FCSTD DOCUMENT  (FreeCAD 0.20R29177 +426 (Git))
Label: Input Cover
License: All rights reserved
LicenseURL: http://en.wikipedia.org/wiki/All_rights_reserved
objects: Sketcher::SketchObject×5, PartDesign::Body×1
note: 6 computed .brp shape members not serialized (recipe doc carries the construction recipe); baked Part::Feature solids carry a one-line shape summary decoded from their .brp

FEATURE [Sketcher::SketchObject] Sketch009  label="Sketch_FrameMain"
  AttachmentOffset = pos=(0,0,12.53) rot=(0,0,1;0rad)
  FullyConstrained = true
  MapMode = 5
  Placement = pos=(0,0,12.53) rot=(0,0,1;0rad)
  Support = -> [XY_Plane]
  expr: .AttachmentOffset.Base.z = 15.88 - 3.35
  sketch-geometry (262):
    g0: LineSegment StartX=0 StartY=0 StartZ=0 EndX=296.63 EndY=0 EndZ=0
    g1: LineSegment StartX=296.63 StartY=0 StartZ=0 EndX=296.63 EndY=221.98 EndZ=0
    g2: LineSegment StartX=289.63 StartY=228.98 StartZ=0 EndX=278.38 EndY=228.98 EndZ=0
    g3: LineSegment StartX=0 StartY=221.98 StartZ=0 EndX=0 EndY=0 EndZ=0
    g4: GeomPoint X=296.63 Y=228.98 Z=0
    g5: ArcOfCircle CenterX=289.63 CenterY=221.98 CenterZ=0 NormalX=0 NormalY=0 NormalZ=1 AngleXU=0 Radius=7 StartAngle=-9e-16 EndAngle=1.5708
    g6: GeomPoint X=296.63 Y=228.98 Z=0
    g7: ArcOfCircle CenterX=7 CenterY=221.98 CenterZ=0 NormalX=0 NormalY=0 NormalZ=1 AngleXU=0 Radius=7 StartAngle=1.5708 EndAngle=3.14159
    g8: GeomPoint X=0 Y=228.98 Z=0
    g9: LineSegment StartX=278.38 StartY=228.98 StartZ=0 EndX=278.38 EndY=216.23 EndZ=0
    g10: LineSegment StartX=18.25 StartY=228.98 StartZ=0 EndX=18.25 EndY=216.23 EndZ=0
    g11: LineSegment StartX=18.25 StartY=216.23 StartZ=0 EndX=278.38 EndY=216.23 EndZ=0
    g12: LineSegment StartX=18.25 StartY=228.98 StartZ=0 EndX=7 EndY=228.98 EndZ=0
    g13: LineSegment StartX=291.63 StartY=201.48 StartZ=0 EndX=291.63 EndY=93 EndZ=0
    g14: LineSegment StartX=0 StartY=114.49 StartZ=0 EndX=148.315 EndY=114.49 EndZ=0
    g15: LineSegment StartX=148.315 StartY=114.49 StartZ=0 EndX=296.63 EndY=114.49 EndZ=0
    g16: LineSegment StartX=18.25 StartY=228.98 StartZ=0 EndX=278.38 EndY=228.98 EndZ=0
    g17: LineSegment StartX=148.315 StartY=114.49 StartZ=0 EndX=148.315 EndY=228.98 EndZ=0
    g18: LineSegment StartX=148.315 StartY=114.49 StartZ=0 EndX=148.315 EndY=0 EndZ=0
    g19: LineSegment StartX=288.63 StartY=204.48 StartZ=0 EndX=8 EndY=204.48 EndZ=0
    g20: LineSegment StartX=288.63 StartY=90 StartZ=0 EndX=8 EndY=90 EndZ=0
    g21: LineSegment StartX=5 StartY=201.48 StartZ=0 EndX=5 EndY=93 EndZ=0
    g22: ArcOfCircle CenterX=8 CenterY=201.48 CenterZ=0 NormalX=0 NormalY=0 NormalZ=1 AngleXU=0 Radius=3 StartAngle=1.5708 EndAngle=3.14159
    g23: GeomPoint X=5 Y=204.48 Z=0
    g24: ArcOfCircle CenterX=8 CenterY=93 CenterZ=0 NormalX=0 NormalY=0 NormalZ=1 AngleXU=0 Radius=3 StartAngle=3.14159 EndAngle=4.71239
    g25: GeomPoint X=5 Y=90 Z=0
    g26: GeomPoint X=9.5 Y=94.5 Z=0
    g27: ArcOfCircle CenterX=288.63 CenterY=93 CenterZ=0 NormalX=0 NormalY=0 NormalZ=1 AngleXU=0 Radius=3 StartAngle=4.71239 EndAngle=6.28319
    g28: GeomPoint X=291.63 Y=90 Z=0
    g29: GeomPoint X=9.5 Y=199.98 Z=0
    g30: ArcOfCircle CenterX=288.63 CenterY=201.48 CenterZ=0 NormalX=0 NormalY=0 NormalZ=1 AngleXU=0 Radius=3 StartAngle=0 EndAngle=1.5708
    g31: GeomPoint X=291.63 Y=204.48 Z=0
    g32: GeomPoint X=287.13 Y=199.98 Z=0
    g33: ArcOfCircle CenterX=285.88 CenterY=198.73 CenterZ=0 NormalX=0 NormalY=0 NormalZ=1 AngleXU=0 Radius=1.25 StartAngle=2.5e-15 EndAngle=1.5708
    g34: LineSegment StartX=287.13 StartY=198.73 StartZ=0 EndX=287.13 EndY=191.543 EndZ=0
    g35: ArcOfCircle CenterX=285.88 CenterY=191.543 CenterZ=0 NormalX=0 NormalY=0 NormalZ=1 AngleXU=0 Radius=1.25 StartAngle=4.71239 EndAngle=6.28319
    g36: LineSegment StartX=285.88 StartY=190.293 StartZ=0 EndX=265.88 EndY=190.293 EndZ=0
    g37: ArcOfCircle CenterX=265.88 CenterY=191.543 CenterZ=0 NormalX=0 NormalY=0 NormalZ=1 AngleXU=0 Radius=1.25 StartAngle=3.14159 EndAngle=4.71239
    g38: LineSegment StartX=264.63 StartY=191.543 StartZ=0 EndX=264.63 EndY=198.73 EndZ=0
    g39: ArcOfCircle CenterX=265.88 CenterY=198.73 CenterZ=0 NormalX=0 NormalY=0 NormalZ=1 AngleXU=0 Radius=1.25 StartAngle=1.5708 EndAngle=3.14159
    g40: LineSegment StartX=265.88 StartY=199.98 StartZ=0 EndX=285.88 EndY=199.98 EndZ=0
    g41: GeomPoint X=287.13 Y=199.98 Z=0
    g42: GeomPoint X=264.63 Y=190.293 Z=0
    g43: ArcOfCircle CenterX=259.793 CenterY=198.73 CenterZ=0 NormalX=0 NormalY=0 NormalZ=1 AngleXU=0 Radius=1.25 StartAngle=-3.6e-15 EndAngle=1.5708
    g44: LineSegment StartX=261.043 StartY=198.73 StartZ=0 EndX=261.043 EndY=191.543 EndZ=0
    g45: ArcOfCircle CenterX=259.793 CenterY=191.543 CenterZ=0 NormalX=0 NormalY=0 NormalZ=1 AngleXU=0 Radius=1.25 StartAngle=4.71239 EndAngle=6.28319
    g46: LineSegment StartX=259.793 StartY=190.293 StartZ=0 EndX=246.793 EndY=190.293 EndZ=0
    g47: ArcOfCircle CenterX=246.793 CenterY=191.543 CenterZ=0 NormalX=0 NormalY=0 NormalZ=1 AngleXU=0 Radius=1.25 StartAngle=3.14159 EndAngle=4.71239
    g48: LineSegment StartX=245.543 StartY=191.543 StartZ=0 EndX=245.543 EndY=198.73 EndZ=0
    g49: ArcOfCircle CenterX=246.793 CenterY=198.73 CenterZ=0 NormalX=0 NormalY=0 NormalZ=1 AngleXU=0 Radius=1.25 StartAngle=1.5708 EndAngle=3.14159
    g50: LineSegment StartX=246.793 StartY=199.98 StartZ=0 EndX=259.793 EndY=199.98 EndZ=0
    g51: GeomPoint X=261.043 Y=199.98 Z=0
    g52: GeomPoint X=245.543 Y=190.293 Z=0
    g53: ArcOfCircle CenterX=240.706 CenterY=198.73 CenterZ=0 NormalX=0 NormalY=0 NormalZ=1 AngleXU=0 Radius=1.25 StartAngle=0 EndAngle=1.5708
    g54: LineSegment StartX=241.956 StartY=198.73 StartZ=0 EndX=241.956 EndY=191.543 EndZ=0
    g55: ArcOfCircle CenterX=240.706 CenterY=191.543 CenterZ=0 NormalX=0 NormalY=0 NormalZ=1 AngleXU=0 Radius=1.25 StartAngle=4.71239 EndAngle=6.28319
    g56: LineSegment StartX=240.706 StartY=190.293 StartZ=0 EndX=227.706 EndY=190.293 EndZ=0
    g57: ArcOfCircle CenterX=227.706 CenterY=191.543 CenterZ=0 NormalX=0 NormalY=0 NormalZ=1 AngleXU=0 Radius=1.25 StartAngle=3.14159 EndAngle=4.71239
    g58: LineSegment StartX=226.456 StartY=191.543 StartZ=0 EndX=226.456 EndY=198.73 EndZ=0
    g59: ArcOfCircle CenterX=227.706 CenterY=198.73 CenterZ=0 NormalX=0 NormalY=0 NormalZ=1 AngleXU=0 Radius=1.25 StartAngle=1.5708 EndAngle=3.14159
    g60: LineSegment StartX=227.706 StartY=199.98 StartZ=0 EndX=240.706 EndY=199.98 EndZ=0
    g61: GeomPoint X=241.956 Y=199.98 Z=0
    g62: GeomPoint X=226.456 Y=190.293 Z=0
    g63: ArcOfCircle CenterX=221.619 CenterY=198.73 CenterZ=0 NormalX=0 NormalY=0 NormalZ=1 AngleXU=0 Radius=1.25 StartAngle=8.5e-15 EndAngle=1.5708
    g64: LineSegment StartX=222.869 StartY=198.73 StartZ=0 EndX=222.869 EndY=191.543 EndZ=0
    g65: ArcOfCircle CenterX=221.619 CenterY=191.543 CenterZ=0 NormalX=0 NormalY=0 NormalZ=1 AngleXU=0 Radius=1.25 StartAngle=4.71239 EndAngle=6.28319
    g66: LineSegment StartX=221.619 StartY=190.293 StartZ=0 EndX=208.619 EndY=190.293 EndZ=0
    g67: ArcOfCircle CenterX=208.619 CenterY=191.543 CenterZ=0 NormalX=0 NormalY=0 NormalZ=1 AngleXU=0 Radius=1.25 StartAngle=3.14159 EndAngle=4.71239
    g68: LineSegment StartX=207.369 StartY=191.543 StartZ=0 EndX=207.369 EndY=198.73 EndZ=0
    g69: ArcOfCircle CenterX=208.619 CenterY=198.73 CenterZ=0 NormalX=0 NormalY=0 NormalZ=1 AngleXU=0 Radius=1.25 StartAngle=1.5708 EndAngle=3.14159
    g70: LineSegment StartX=208.619 StartY=199.98 StartZ=0 EndX=221.619 EndY=199.98 EndZ=0
    g71: GeomPoint X=222.869 Y=199.98 Z=0
    g72: GeomPoint X=207.369 Y=190.293 Z=0
    g73: ArcOfCircle CenterX=202.532 CenterY=198.73 CenterZ=0 NormalX=0 NormalY=0 NormalZ=1 AngleXU=0 Radius=1.25 StartAngle=2e-15 EndAngle=1.5708
    g74: LineSegment StartX=203.782 StartY=198.73 StartZ=0 EndX=203.782 EndY=191.543 EndZ=0
    g75: ArcOfCircle CenterX=202.532 CenterY=191.543 CenterZ=0 NormalX=0 NormalY=0 NormalZ=1 AngleXU=0 Radius=1.25 StartAngle=4.71239 EndAngle=6.28319
    g76: LineSegment StartX=202.532 StartY=190.293 StartZ=0 EndX=189.532 EndY=190.293 EndZ=0
    g77: ArcOfCircle CenterX=189.532 CenterY=191.543 CenterZ=0 NormalX=0 NormalY=0 NormalZ=1 AngleXU=0 Radius=1.25 StartAngle=3.14159 EndAngle=4.71239
    g78: LineSegment StartX=188.282 StartY=191.543 StartZ=0 EndX=188.282 EndY=198.73 EndZ=0
    g79: ArcOfCircle CenterX=189.532 CenterY=198.73 CenterZ=0 NormalX=0 NormalY=0 NormalZ=1 AngleXU=0 Radius=1.25 StartAngle=1.5708 EndAngle=3.14159
    g80: LineSegment StartX=189.532 StartY=199.98 StartZ=0 EndX=202.532 EndY=199.98 EndZ=0
    g81: GeomPoint X=203.782 Y=199.98 Z=0
    g82: GeomPoint X=188.282 Y=190.293 Z=0
    g83: ArcOfCircle CenterX=183.445 CenterY=198.73 CenterZ=0 NormalX=0 NormalY=0 NormalZ=1 AngleXU=0 Radius=1.25 StartAngle=-1.8e-15 EndAngle=1.5708
    g84: LineSegment StartX=184.695 StartY=198.73 StartZ=0 EndX=184.695 EndY=191.543 EndZ=0
    g85: ArcOfCircle CenterX=183.445 CenterY=191.543 CenterZ=0 NormalX=0 NormalY=0 NormalZ=1 AngleXU=0 Radius=1.25 StartAngle=4.71239 EndAngle=6.28319
    g86: LineSegment StartX=183.445 StartY=190.293 StartZ=0 EndX=170.445 EndY=190.293 EndZ=0
    g87: ArcOfCircle CenterX=170.445 CenterY=191.543 CenterZ=0 NormalX=0 NormalY=0 NormalZ=1 AngleXU=0 Radius=1.25 StartAngle=3.14159 EndAngle=4.71239
    g88: LineSegment StartX=169.195 StartY=191.543 StartZ=0 EndX=169.195 EndY=198.73 EndZ=0
    g89: ArcOfCircle CenterX=170.445 CenterY=198.73 CenterZ=0 NormalX=0 NormalY=0 NormalZ=1 AngleXU=0 Radius=1.25 StartAngle=1.5708 EndAngle=3.14159
    g90: LineSegment StartX=170.445 StartY=199.98 StartZ=0 EndX=183.445 EndY=199.98 EndZ=0
    g91: GeomPoint X=184.695 Y=199.98 Z=0
    g92: GeomPoint X=169.195 Y=190.293 Z=0
    g93: ArcOfCircle CenterX=164.358 CenterY=198.73 CenterZ=0 NormalX=0 NormalY=0 NormalZ=1 AngleXU=0 Radius=1.25 StartAngle=-5.3e-15 EndAngle=1.5708
    g94: LineSegment StartX=165.608 StartY=198.73 StartZ=0 EndX=165.608 EndY=191.543 EndZ=0
    g95: ArcOfCircle CenterX=164.358 CenterY=191.543 CenterZ=0 NormalX=0 NormalY=0 NormalZ=1 AngleXU=0 Radius=1.25 StartAngle=4.71239 EndAngle=6.28319
    g96: LineSegment StartX=164.358 StartY=190.293 StartZ=0 EndX=151.358 EndY=190.293 EndZ=0
    g97: ArcOfCircle CenterX=151.358 CenterY=191.543 CenterZ=0 NormalX=0 NormalY=0 NormalZ=1 AngleXU=0 Radius=1.25 StartAngle=3.14159 EndAngle=4.71239
    g98: LineSegment StartX=150.108 StartY=191.543 StartZ=0 EndX=150.108 EndY=198.73 EndZ=0
    g99: ArcOfCircle CenterX=151.358 CenterY=198.73 CenterZ=0 NormalX=0 NormalY=0 NormalZ=1 AngleXU=0 Radius=1.25 StartAngle=1.5708 EndAngle=3.14159
    g100: LineSegment StartX=151.358 StartY=199.98 StartZ=0 EndX=164.358 EndY=199.98 EndZ=0
    g101: GeomPoint X=165.608 Y=199.98 Z=0
    g102: GeomPoint X=150.108 Y=190.293 Z=0
    g103: ArcOfCircle CenterX=145.272 CenterY=198.73 CenterZ=0 NormalX=0 NormalY=0 NormalZ=1 AngleXU=0 Radius=1.25 StartAngle=2e-15 EndAngle=1.5708
    g104: LineSegment StartX=146.522 StartY=198.73 StartZ=0 EndX=146.522 EndY=191.543 EndZ=0
    g105: ArcOfCircle CenterX=145.272 CenterY=191.543 CenterZ=0 NormalX=0 NormalY=0 NormalZ=1 AngleXU=0 Radius=1.25 StartAngle=4.71239 EndAngle=6.28319
    g106: LineSegment StartX=145.272 StartY=190.293 StartZ=0 EndX=132.272 EndY=190.293 EndZ=0
    g107: ArcOfCircle CenterX=132.272 CenterY=191.543 CenterZ=0 NormalX=0 NormalY=0 NormalZ=1 AngleXU=0 Radius=1.25 StartAngle=3.14159 EndAngle=4.71239
    g108: LineSegment StartX=131.022 StartY=191.543 StartZ=0 EndX=131.022 EndY=198.73 EndZ=0
    g109: ArcOfCircle CenterX=132.272 CenterY=198.73 CenterZ=0 NormalX=0 NormalY=0 NormalZ=1 AngleXU=0 Radius=1.25 StartAngle=1.5708 EndAngle=3.14159
    g110: LineSegment StartX=132.272 StartY=199.98 StartZ=0 EndX=145.272 EndY=199.98 EndZ=0
    g111: GeomPoint X=146.522 Y=199.98 Z=0
    g112: GeomPoint X=131.022 Y=190.293 Z=0
    g113: ArcOfCircle CenterX=126.185 CenterY=198.73 CenterZ=0 NormalX=0 NormalY=0 NormalZ=1 AngleXU=0 Radius=1.25 StartAngle=8.6e-15 EndAngle=1.5708
    g114: LineSegment StartX=127.435 StartY=198.73 StartZ=0 EndX=127.435 EndY=191.543 EndZ=0
    g115: ArcOfCircle CenterX=126.185 CenterY=191.543 CenterZ=0 NormalX=0 NormalY=0 NormalZ=1 AngleXU=0 Radius=1.25 StartAngle=4.71239 EndAngle=6.28319
    g116: LineSegment StartX=126.185 StartY=190.293 StartZ=0 EndX=113.185 EndY=190.293 EndZ=0
    g117: ArcOfCircle CenterX=113.185 CenterY=191.543 CenterZ=0 NormalX=0 NormalY=0 NormalZ=1 AngleXU=0 Radius=1.25 StartAngle=3.14159 EndAngle=4.71239
    g118: LineSegment StartX=111.935 StartY=191.543 StartZ=0 EndX=111.935 EndY=198.73 EndZ=0
    g119: ArcOfCircle CenterX=113.185 CenterY=198.73 CenterZ=0 NormalX=0 NormalY=0 NormalZ=1 AngleXU=0 Radius=1.25 StartAngle=1.5708 EndAngle=3.14159
    g120: LineSegment StartX=113.185 StartY=199.98 StartZ=0 EndX=126.185 EndY=199.98 EndZ=0
    g121: GeomPoint X=127.435 Y=199.98 Z=0
    g122: GeomPoint X=111.935 Y=190.293 Z=0
    g123: LineSegment StartX=127.435 StartY=198.73 StartZ=0 EndX=131.022 EndY=198.73 EndZ=0
    g124: LineSegment StartX=146.522 StartY=198.73 StartZ=0 EndX=150.108 EndY=198.73 EndZ=0
    g125: LineSegment StartX=165.608 StartY=198.73 StartZ=0 EndX=169.195 EndY=198.73 EndZ=0
    g126: LineSegment StartX=184.695 StartY=198.73 StartZ=0 EndX=188.282 EndY=198.73 EndZ=0
    g127: LineSegment StartX=203.782 StartY=198.73 StartZ=0 EndX=207.369 EndY=198.73 EndZ=0
    g128: LineSegment StartX=222.869 StartY=198.73 StartZ=0 EndX=226.456 EndY=198.73 EndZ=0
    g129: LineSegment StartX=241.956 StartY=198.73 StartZ=0 EndX=245.543 EndY=198.73 EndZ=0
    g130: LineSegment StartX=261.043 StartY=198.73 StartZ=0 EndX=264.63 EndY=198.73 EndZ=0
    g131: ArcOfCircle CenterX=107.098 CenterY=198.73 CenterZ=0 NormalX=0 NormalY=0 NormalZ=1 AngleXU=0 Radius=1.25 StartAngle=8.7e-15 EndAngle=1.5708
    g132: LineSegment StartX=108.348 StartY=198.73 StartZ=0 EndX=108.348 EndY=191.543 EndZ=0
    g133: ArcOfCircle CenterX=107.098 CenterY=191.543 CenterZ=0 NormalX=0 NormalY=0 NormalZ=1 AngleXU=0 Radius=1.25 StartAngle=4.71239 EndAngle=6.28319
    g134: LineSegment StartX=107.098 StartY=190.293 StartZ=0 EndX=94.0977 EndY=190.293 EndZ=0
    g135: ArcOfCircle CenterX=94.0977 CenterY=191.543 CenterZ=0 NormalX=0 NormalY=0 NormalZ=1 AngleXU=0 Radius=1.25 StartAngle=3.14159 EndAngle=4.71239
    g136: LineSegment StartX=92.8477 StartY=191.543 StartZ=0 EndX=92.8477 EndY=198.73 EndZ=0
    g137: ArcOfCircle CenterX=94.0977 CenterY=198.73 CenterZ=0 NormalX=0 NormalY=0 NormalZ=1 AngleXU=0 Radius=1.25 StartAngle=1.5708 EndAngle=3.14159
    g138: LineSegment StartX=94.0977 StartY=199.98 StartZ=0 EndX=107.098 EndY=199.98 EndZ=0
    g139: GeomPoint X=108.348 Y=199.98 Z=0
    g140: GeomPoint X=92.8477 Y=190.293 Z=0
    g141: ArcOfCircle CenterX=88.0108 CenterY=198.73 CenterZ=0 NormalX=0 NormalY=0 NormalZ=1 AngleXU=0 Radius=1.25 StartAngle=1e-15 EndAngle=1.5708
    g142: LineSegment StartX=89.2608 StartY=198.73 StartZ=0 EndX=89.2608 EndY=191.543 EndZ=0
    g143: ArcOfCircle CenterX=88.0108 CenterY=191.543 CenterZ=0 NormalX=0 NormalY=0 NormalZ=1 AngleXU=0 Radius=1.25 StartAngle=4.71239 EndAngle=6.28319
    g144: LineSegment StartX=88.0108 StartY=190.293 StartZ=0 EndX=75.0108 EndY=190.293 EndZ=0
    g145: ArcOfCircle CenterX=75.0108 CenterY=191.543 CenterZ=0 NormalX=0 NormalY=0 NormalZ=1 AngleXU=0 Radius=1.25 StartAngle=3.14159 EndAngle=4.71239
    g146: LineSegment StartX=73.7608 StartY=191.543 StartZ=0 EndX=73.7608 EndY=198.73 EndZ=0
    g147: ArcOfCircle CenterX=75.0108 CenterY=198.73 CenterZ=0 NormalX=0 NormalY=0 NormalZ=1 AngleXU=0 Radius=1.25 StartAngle=1.5708 EndAngle=3.14159
    g148: LineSegment StartX=75.0108 StartY=199.98 StartZ=0 EndX=88.0108 EndY=199.98 EndZ=0
    g149: GeomPoint X=89.2608 Y=199.98 Z=0
    g150: GeomPoint X=73.7608 Y=190.293 Z=0
    g151: ArcOfCircle CenterX=68.9238 CenterY=198.73 CenterZ=0 NormalX=0 NormalY=0 NormalZ=1 AngleXU=0 Radius=1.25 StartAngle=-5.3e-15 EndAngle=1.5708
    g152: LineSegment StartX=70.1738 StartY=198.73 StartZ=0 EndX=70.1738 EndY=191.543 EndZ=0
    g153: ArcOfCircle CenterX=68.9238 CenterY=191.543 CenterZ=0 NormalX=0 NormalY=0 NormalZ=1 AngleXU=0 Radius=1.25 StartAngle=4.71239 EndAngle=6.28319
    g154: LineSegment StartX=68.9238 StartY=190.293 StartZ=0 EndX=55.9238 EndY=190.293 EndZ=0
    g155: ArcOfCircle CenterX=55.9238 CenterY=191.543 CenterZ=0 NormalX=0 NormalY=0 NormalZ=1 AngleXU=0 Radius=1.25 StartAngle=3.14159 EndAngle=4.71239
    g156: LineSegment StartX=54.6738 StartY=191.543 StartZ=0 EndX=54.6738 EndY=198.73 EndZ=0
    g157: ArcOfCircle CenterX=55.9238 CenterY=198.73 CenterZ=0 NormalX=0 NormalY=0 NormalZ=1 AngleXU=0 Radius=1.25 StartAngle=1.5708 EndAngle=3.14159
    g158: LineSegment StartX=55.9238 StartY=199.98 StartZ=0 EndX=68.9238 EndY=199.98 EndZ=0
    g159: GeomPoint X=70.1738 Y=199.98 Z=0
    g160: LineSegment StartX=70.1738 StartY=198.73 StartZ=0 EndX=73.7608 EndY=198.73 EndZ=0
    g161: LineSegment StartX=89.2608 StartY=198.73 StartZ=0 EndX=92.8477 EndY=198.73 EndZ=0
    g162: ArcOfCircle CenterX=10.75 CenterY=198.73 CenterZ=0 NormalX=0 NormalY=0 NormalZ=1 AngleXU=0 Radius=1.25 StartAngle=1.5708 EndAngle=3.14159
    g163: LineSegment StartX=10.75 StartY=199.98 StartZ=0 EndX=30.75 EndY=199.98 EndZ=0
    g164: ArcOfCircle CenterX=30.75 CenterY=198.73 CenterZ=0 NormalX=0 NormalY=0 NormalZ=1 AngleXU=0 Radius=1.25 StartAngle=5.9e-15 EndAngle=1.5708
    g165: LineSegment StartX=32 StartY=198.73 StartZ=0 EndX=32 EndY=191.543 EndZ=0
    g166: ArcOfCircle CenterX=30.75 CenterY=191.543 CenterZ=0 NormalX=0 NormalY=0 NormalZ=1 AngleXU=0 Radius=1.25 StartAngle=4.71239 EndAngle=6.28319
    g167: LineSegment StartX=30.75 StartY=190.293 StartZ=0 EndX=10.75 EndY=190.293 EndZ=0
    g168: ArcOfCircle CenterX=10.75 CenterY=191.543 CenterZ=0 NormalX=0 NormalY=0 NormalZ=1 AngleXU=0 Radius=1.25 StartAngle=3.14159 EndAngle=4.71239
    g169: LineSegment StartX=9.5 StartY=191.543 StartZ=0 EndX=9.5 EndY=198.73 EndZ=0
    g170: GeomPoint X=9.5 Y=199.98 Z=0
    g171: GeomPoint X=32 Y=190.293 Z=0
    g172: ArcOfCircle CenterX=36.8369 CenterY=198.73 CenterZ=0 NormalX=0 NormalY=0 NormalZ=1 AngleXU=0 Radius=1.25 StartAngle=1.5708 EndAngle=3.14159
    g173: LineSegment StartX=36.8369 StartY=199.98 StartZ=0 EndX=49.8369 EndY=199.98 EndZ=0
    g174: ArcOfCircle CenterX=49.8369 CenterY=198.73 CenterZ=0 NormalX=0 NormalY=0 NormalZ=1 AngleXU=0 Radius=1.25 StartAngle=-5.3e-15 EndAngle=1.5708
    g175: LineSegment StartX=51.0869 StartY=198.73 StartZ=0 EndX=51.0869 EndY=191.543 EndZ=0
    g176: ArcOfCircle CenterX=49.8369 CenterY=191.543 CenterZ=0 NormalX=0 NormalY=0 NormalZ=1 AngleXU=0 Radius=1.25 StartAngle=4.71239 EndAngle=6.28319
    g177: LineSegment StartX=49.8369 StartY=190.293 StartZ=0 EndX=36.8369 EndY=190.293 EndZ=0
    g178: ArcOfCircle CenterX=36.8369 CenterY=191.543 CenterZ=0 NormalX=0 NormalY=0 NormalZ=1 AngleXU=0 Radius=1.25 StartAngle=3.14159 EndAngle=4.71239
    g179: LineSegment StartX=35.5869 StartY=191.543 StartZ=0 EndX=35.5869 EndY=198.73 EndZ=0
    g180: GeomPoint X=35.5869 Y=199.98 Z=0
    g181: GeomPoint X=51.0869 Y=190.293 Z=0
    g182: LineSegment StartX=32 StartY=198.73 StartZ=0 EndX=35.5869 EndY=198.73 EndZ=0
    g183: LineSegment StartX=51.0869 StartY=198.73 StartZ=0 EndX=54.6738 EndY=198.73 EndZ=0
    g184: ArcOfCircle CenterX=285.88 CenterY=185.384 CenterZ=0 NormalX=0 NormalY=0 NormalZ=1 AngleXU=0 Radius=1.25 StartAngle=4e-15 EndAngle=1.5708
    g185: LineSegment StartX=287.13 StartY=185.384 StartZ=0 EndX=287.13 EndY=172.384 EndZ=0
    g186: ArcOfCircle CenterX=285.88 CenterY=172.384 CenterZ=0 NormalX=0 NormalY=0 NormalZ=1 AngleXU=0 Radius=1.25 StartAngle=4.71239 EndAngle=6.28319
    g187: LineSegment StartX=285.88 StartY=171.134 StartZ=0 EndX=258.88 EndY=171.134 EndZ=0
    g188: ArcOfCircle CenterX=258.88 CenterY=172.384 CenterZ=0 NormalX=0 NormalY=0 NormalZ=1 AngleXU=0 Radius=1.25 StartAngle=3.14159 EndAngle=4.71239
    g189: LineSegment StartX=257.63 StartY=172.384 StartZ=0 EndX=257.63 EndY=185.384 EndZ=0
    g190: ArcOfCircle CenterX=258.88 CenterY=185.384 CenterZ=0 NormalX=0 NormalY=0 NormalZ=1 AngleXU=0 Radius=1.25 StartAngle=1.5708 EndAngle=3.14159
    g191: LineSegment StartX=258.88 StartY=186.634 StartZ=0 EndX=285.88 EndY=186.634 EndZ=0
    g192: GeomPoint X=287.13 Y=186.634 Z=0
    g193: GeomPoint X=257.63 Y=171.134 Z=0
    g194: LineSegment StartX=285.88 StartY=190.293 StartZ=0 EndX=285.88 EndY=186.634 EndZ=0
    g195: ArcOfCircle CenterX=285.88 CenterY=166.226 CenterZ=0 NormalX=0 NormalY=0 NormalZ=1 AngleXU=0 Radius=1.25 StartAngle=-8e-15 EndAngle=1.5708
    g196: LineSegment StartX=287.13 StartY=166.226 StartZ=0 EndX=287.13 EndY=153.226 EndZ=0
    g197: ArcOfCircle CenterX=285.88 CenterY=153.226 CenterZ=0 NormalX=0 NormalY=0 NormalZ=1 AngleXU=0 Radius=1.25 StartAngle=4.71239 EndAngle=6.28319
    g198: LineSegment StartX=285.88 StartY=151.976 StartZ=0 EndX=267.88 EndY=151.976 EndZ=0
    g199: ArcOfCircle CenterX=267.88 CenterY=153.226 CenterZ=0 NormalX=0 NormalY=0 NormalZ=1 AngleXU=0 Radius=1.25 StartAngle=3.14159 EndAngle=4.71239
    g200: LineSegment StartX=266.63 StartY=153.226 StartZ=0 EndX=266.63 EndY=166.226 EndZ=0
    g201: ArcOfCircle CenterX=267.88 CenterY=166.226 CenterZ=0 NormalX=0 NormalY=0 NormalZ=1 AngleXU=0 Radius=1.25 StartAngle=1.5708 EndAngle=3.14159
    g202: LineSegment StartX=267.88 StartY=167.476 StartZ=0 EndX=285.88 EndY=167.476 EndZ=0
    g203: GeomPoint X=287.13 Y=167.476 Z=0
    g204: GeomPoint X=266.63 Y=151.976 Z=0
    g205: ArcOfCircle CenterX=285.88 CenterY=147.067 CenterZ=0 NormalX=0 NormalY=0 NormalZ=1 AngleXU=0 Radius=1.25 StartAngle=8.4e-15 EndAngle=1.5708
    g206: LineSegment StartX=287.13 StartY=147.067 StartZ=0 EndX=287.13 EndY=134.067 EndZ=0
    g207: ArcOfCircle CenterX=285.88 CenterY=134.067 CenterZ=0 NormalX=0 NormalY=0 NormalZ=1 AngleXU=0 Radius=1.25 StartAngle=4.71239 EndAngle=6.28319
    g208: LineSegment StartX=285.88 StartY=132.817 StartZ=0 EndX=253.505 EndY=132.817 EndZ=0
    g209: ArcOfCircle CenterX=253.505 CenterY=134.067 CenterZ=0 NormalX=0 NormalY=0 NormalZ=1 AngleXU=0 Radius=1.25 StartAngle=3.14159 EndAngle=4.71239
    g210: LineSegment StartX=252.255 StartY=134.067 StartZ=0 EndX=252.255 EndY=147.067 EndZ=0
    g211: ArcOfCircle CenterX=253.505 CenterY=147.067 CenterZ=0 NormalX=0 NormalY=0 NormalZ=1 AngleXU=0 Radius=1.25 StartAngle=1.5708 EndAngle=3.14159
    g212: LineSegment StartX=253.505 StartY=148.317 StartZ=0 EndX=285.88 EndY=148.317 EndZ=0
    g213: GeomPoint X=287.13 Y=148.317 Z=0
    g214: GeomPoint X=252.255 Y=132.817 Z=0
    g215: ArcOfCircle CenterX=285.88 CenterY=127.909 CenterZ=0 NormalX=0 NormalY=0 NormalZ=1 AngleXU=0 Radius=1.25 StartAngle=2.9e-15 EndAngle=1.5708
    g216: LineSegment StartX=287.13 StartY=127.909 StartZ=0 EndX=287.13 EndY=114.909 EndZ=0
    g217: ArcOfCircle CenterX=285.88 CenterY=114.909 CenterZ=0 NormalX=0 NormalY=0 NormalZ=1 AngleXU=0 Radius=1.25 StartAngle=4.71239 EndAngle=6.28319
    g218: LineSegment StartX=285.88 StartY=113.659 StartZ=0 EndX=244.592 EndY=113.659 EndZ=0
    g219: ArcOfCircle CenterX=244.592 CenterY=114.909 CenterZ=0 NormalX=0 NormalY=0 NormalZ=1 AngleXU=0 Radius=1.25 StartAngle=3.14159 EndAngle=4.71239
    g220: LineSegment StartX=243.342 StartY=114.909 StartZ=0 EndX=243.342 EndY=127.909 EndZ=0
    g221: ArcOfCircle CenterX=244.592 CenterY=127.909 CenterZ=0 NormalX=0 NormalY=0 NormalZ=1 AngleXU=0 Radius=1.25 StartAngle=1.5708 EndAngle=3.14159
    g222: LineSegment StartX=244.592 StartY=129.159 StartZ=0 EndX=285.88 EndY=129.159 EndZ=0
    g223: GeomPoint X=287.13 Y=129.159 Z=0
    g224: GeomPoint X=243.343 Y=113.659 Z=0
    g225: LineSegment StartX=285.88 StartY=171.134 StartZ=0 EndX=285.88 EndY=167.476 EndZ=0
    g226: LineSegment StartX=285.88 StartY=151.976 StartZ=0 EndX=285.88 EndY=148.317 EndZ=0
    g227: LineSegment StartX=285.88 StartY=132.817 StartZ=0 EndX=285.88 EndY=129.159 EndZ=0
    g228: ArcOfCircle CenterX=285.88 CenterY=198.73 CenterZ=0 NormalX=0 NormalY=0 NormalZ=1 AngleXU=0 Radius=1.25 StartAngle=-5.3e-15 EndAngle=1.5708
    g229: LineSegment StartX=287.13 StartY=198.73 StartZ=0 EndX=287.13 EndY=95.75 EndZ=0
    g230: ArcOfCircle CenterX=285.88 CenterY=95.75 CenterZ=0 NormalX=0 NormalY=0 NormalZ=1 AngleXU=0 Radius=1.25 StartAngle=4.71239 EndAngle=6.28319
    g231: LineSegment StartX=285.88 StartY=94.5 StartZ=0 EndX=10.75 EndY=94.5 EndZ=0
    g232: ArcOfCircle CenterX=10.75 CenterY=95.75 CenterZ=0 NormalX=0 NormalY=0 NormalZ=1 AngleXU=0 Radius=1.25 StartAngle=3.14159 EndAngle=4.71239
    g233: LineSegment StartX=9.5 StartY=95.75 StartZ=0 EndX=9.5 EndY=198.73 EndZ=0
    g234: ArcOfCircle CenterX=10.75 CenterY=198.73 CenterZ=0 NormalX=0 NormalY=0 NormalZ=1 AngleXU=0 Radius=1.25 StartAngle=1.5708 EndAngle=3.14159
    g235: LineSegment StartX=10.75 StartY=199.98 StartZ=0 EndX=285.88 EndY=199.98 EndZ=0
    g236: GeomPoint X=287.13 Y=199.98 Z=0
    g237: GeomPoint X=9.5 Y=94.5 Z=0
    g238: LineSegment StartX=287.13 StartY=198.73 StartZ=0 EndX=291.63 EndY=198.73 EndZ=0
    g239: LineSegment StartX=285.88 StartY=199.98 StartZ=0 EndX=285.88 EndY=204.48 EndZ=0
    g240: LineSegment StartX=111.935 StartY=198.73 StartZ=0 EndX=108.348 EndY=198.73 EndZ=0
    g241: LineSegment StartX=285.88 StartY=94.5 StartZ=0 EndX=285.88 EndY=90 EndZ=0
    g242: ArcOfCircle CenterX=285.88 CenterY=108.75 CenterZ=0 NormalX=0 NormalY=0 NormalZ=1 AngleXU=0 Radius=1.25 StartAngle=2.8e-15 EndAngle=1.5708
    g243: LineSegment StartX=287.13 StartY=108.75 StartZ=0 EndX=287.13 EndY=95.75 EndZ=0
    g244: ArcOfCircle CenterX=285.88 CenterY=95.75 CenterZ=0 NormalX=0 NormalY=0 NormalZ=1 AngleXU=0 Radius=1.25 StartAngle=4.71239 EndAngle=6.28319
    g245: LineSegment StartX=285.88 StartY=94.5 StartZ=0 EndX=269.88 EndY=94.5 EndZ=0
    g246: ArcOfCircle CenterX=269.88 CenterY=95.75 CenterZ=0 NormalX=0 NormalY=0 NormalZ=1 AngleXU=0 Radius=1.25 StartAngle=3.14159 EndAngle=4.71239
    g247: LineSegment StartX=268.63 StartY=95.75 StartZ=0 EndX=268.63 EndY=108.75 EndZ=0
    g248: ArcOfCircle CenterX=269.88 CenterY=108.75 CenterZ=0 NormalX=0 NormalY=0 NormalZ=1 AngleXU=0 Radius=1.25 StartAngle=1.5708 EndAngle=3.14159
    g249: LineSegment StartX=269.88 StartY=110 StartZ=0 EndX=285.88 EndY=110 EndZ=0
    g250: GeomPoint X=287.13 Y=110 Z=0
    g251: GeomPoint X=268.63 Y=94.5 Z=0
    g252: LineSegment StartX=285.88 StartY=113.659 StartZ=0 EndX=285.88 EndY=110 EndZ=0
    g253: LineSegment StartX=285.88 StartY=110 StartZ=0 EndX=9.5 EndY=110 EndZ=0
    g254: LineSegment StartX=285.88 StartY=113.659 StartZ=0 EndX=9.5 EndY=113.659 EndZ=0
    g255: LineSegment StartX=285.88 StartY=129.159 StartZ=0 EndX=9.5 EndY=129.159 EndZ=0
    g256: LineSegment StartX=285.88 StartY=132.817 StartZ=0 EndX=9.5 EndY=132.817 EndZ=0
    g257: LineSegment StartX=285.88 StartY=148.317 StartZ=0 EndX=9.5 EndY=148.317 EndZ=0
    g258: LineSegment StartX=285.88 StartY=151.976 StartZ=0 EndX=9.5 EndY=151.976 EndZ=0
    g259: LineSegment StartX=285.88 StartY=167.476 StartZ=0 EndX=9.5 EndY=167.476 EndZ=0
    g260: LineSegment StartX=285.88 StartY=171.134 StartZ=0 EndX=9.5 EndY=171.134 EndZ=0
    g261: LineSegment StartX=285.88 StartY=186.634 StartZ=0 EndX=9.5 EndY=186.634 EndZ=0
  constraints (626):
    c: Coincident(g0,g1)
    c: Coincident(g3,g0)
    c: Horizontal(g0)
    c: Horizontal(g2)
    c: Vertical(g1)
    c: Vertical(g3)
    c: Coincident(g0,g-1)
    c: DistanceX(g0,g0) = 296.63
    c: DistanceY(g1,g6) = 228.98
    c: Coincident(g4,g6)
    c: PointOnObject(g6,g1)
    c: PointOnObject(g6,g2)
    c: Tangent(g1,g5) = -1.5708
    c: Tangent(g2,g5) = -1.5708
    c: PointOnObject(g8,g3)
    c: PointOnObject(g8,g2)
    c: Tangent(g3,g7) = -1.5708
    c: Coincident(g12,g7) = -1.5708
    c: Radius(g7) = 7
    c: Radius(g5) = 7
    c: Vertical(g9)
    c: Vertical(g10)
    c: DistanceX(g8,g10) = 18.25
    c: DistanceX(g9,g4) = 18.25
    c: Distance(g9) = 12.75
    c: Coincident(g11,g10)
    c: Coincident(g11,g9)
    c: Coincident(g2,g9)
    c: Coincident(g12,g10)
    c: Horizontal(g12)
    c: Equal(g3,g1)
    c: Equal(g10,g9)
    c: Equal(g12,g2)
    c: Vertical(g13)
    c: DistanceX(g28,g0) = 5
    c: DistanceY(g0,g28) = 90
    c: DistanceY(g31,g9) = 11.75
    c: PointOnObject(g14,g3)
    c: Horizontal(g14)
    c: Coincident(g14,g15)
    c: PointOnObject(g15,g1)
    c: Horizontal(g15)
    c: Equal(g14,g15)
    c: Coincident(g16,g10)
    c: Coincident(g16,g2)
    c: Coincident(g17,g14)
    c: PointOnObject(g17,g16)
    c: Vertical(g17)
    c: Coincident(g18,g14)
    c: PointOnObject(g18,g0)
    c: Vertical(g18)
    c: Equal(g17,g18)
    c: Horizontal(g20)
    c: Symmetric(g23,g31,g17)
    c: Symmetric(g29,g32,g17)
    c: PointOnObject(g23,g21)
    c: PointOnObject(g23,g19)
    c: Tangent(g21,g22) = -1.5708
    c: Tangent(g19,g22) = -1.5708
    c: PointOnObject(g25,g21)
    c: PointOnObject(g25,g20)
    c: Tangent(g21,g24) = -1.5708
    c: Tangent(g20,g24) = 1.5708
    c: PointOnObject(g28,g20)
    c: PointOnObject(g28,g13)
    c: Tangent(g20,g27) = 1.5708
    c: Tangent(g13,g27) = 1.5708
    c: PointOnObject(g31,g19)
    c: PointOnObject(g31,g13)
    c: Tangent(g19,g30) = -1.5708
    c: Tangent(g13,g30) = 1.5708
    c: Radius(g30) = 3
    c: Radius(g22) = 3
    c: Radius(g24) = 3
    c: Radius(g27) = 3
    c: Vertical(g21)
    c: Tangent(g33,g34) = 1.5708
    c: Tangent(g34,g35) = 1.5708
    c: Tangent(g35,g36) = 1.5708
    c: Tangent(g36,g37) = 1.5708
    c: Tangent(g37,g38) = 1.5708
    c: Tangent(g38,g39) = 1.5708
    c: Tangent(g39,g40) = 1.5708
    c: Tangent(g40,g33) = 1.5708
    c: Horizontal(g36)
    c: Horizontal(g40)
    c: Vertical(g34)
    c: Vertical(g38)
    c: Equal(g33,g35)
    c: Equal(g35,g37)
    c: Equal(g37,g39)
    c: PointOnObject(g41,g34)
    c: PointOnObject(g41,g40)
    c: PointOnObject(g42,g36)
    c: PointOnObject(g42,g38)
    c: Coincident(g41,g32)
    c: DistanceY(g36,g39) = 9.6875
    c: DistanceX(g38,g33) = 22.5
    c: Radius(g33) = 1.25
    c: Tangent(g43,g44) = 1.5708
    c: Tangent(g44,g45) = 1.5708
    c: Tangent(g45,g46) = 1.5708
    c: Tangent(g46,g47) = 1.5708
    c: Tangent(g47,g48) = 1.5708
    c: Tangent(g48,g49) = 1.5708
    c: Tangent(g49,g50) = 1.5708
    c: Tangent(g50,g43) = 1.5708
    c: Horizontal(g46)
    c: Horizontal(g50)
    c: Vertical(g44)
    c: Vertical(g48)
    c: Equal(g43,g45)
    c: Equal(g45,g47)
    c: Equal(g47,g49)
    c: PointOnObject(g51,g44)
    c: PointOnObject(g51,g50)
    c: PointOnObject(g52,g46)
    c: PointOnObject(g52,g48)
    c: Equal(g43,g39)
    c: Equal(g44,g38)
    c: Tangent(g53,g54) = 1.5708
    c: Tangent(g54,g55) = 1.5708
    c: Tangent(g55,g56) = 1.5708
    c: Tangent(g56,g57) = 1.5708
    c: Tangent(g57,g58) = 1.5708
    c: Tangent(g58,g59) = 1.5708
    c: Tangent(g59,g60) = 1.5708
    c: Tangent(g60,g53) = 1.5708
    c: Horizontal(g56)
    c: Horizontal(g60)
    c: Vertical(g54)
    c: Vertical(g58)
    c: Equal(g53,g55)
    c: Equal(g55,g57)
    c: Equal(g57,g59)
    c: PointOnObject(g61,g54)
    c: PointOnObject(g61,g60)
    c: PointOnObject(g62,g56)
    c: PointOnObject(g62,g58)
    c: Tangent(g63,g64) = 1.5708
    c: Tangent(g64,g65) = 1.5708
    c: Tangent(g65,g66) = 1.5708
    c: Tangent(g66,g67) = 1.5708
    c: Tangent(g67,g68) = 1.5708
    c: Tangent(g68,g69) = 1.5708
    c: Tangent(g69,g70) = 1.5708
    c: Tangent(g70,g63) = 1.5708
    c: Horizontal(g66)
    c: Horizontal(g70)
    c: Vertical(g64)
    c: Vertical(g68)
    c: Equal(g63,g65)
    c: Equal(g65,g67)
    c: Equal(g67,g69)
    c: PointOnObject(g71,g64)
    c: PointOnObject(g71,g70)
    c: PointOnObject(g72,g66)
    c: PointOnObject(g72,g68)
    c: Tangent(g73,g74) = 1.5708
    c: Tangent(g74,g75) = 1.5708
    c: Tangent(g75,g76) = 1.5708
    c: Tangent(g76,g77) = 1.5708
    c: Tangent(g77,g78) = 1.5708
    c: Tangent(g78,g79) = 1.5708
    c: Tangent(g79,g80) = 1.5708
    c: Tangent(g80,g73) = 1.5708
    c: Horizontal(g76)
    c: Horizontal(g80)
    c: Vertical(g74)
    c: Vertical(g78)
    c: Equal(g73,g75)
    c: Equal(g75,g77)
    c: Equal(g77,g79)
    c: PointOnObject(g81,g74)
    c: PointOnObject(g81,g80)
    c: PointOnObject(g82,g76)
    c: PointOnObject(g82,g78)
    c: Tangent(g83,g84) = 1.5708
    c: Tangent(g84,g85) = 1.5708
    c: Tangent(g85,g86) = 1.5708
    c: Tangent(g86,g87) = 1.5708
    c: Tangent(g87,g88) = 1.5708
    c: Tangent(g88,g89) = 1.5708
    c: Tangent(g89,g90) = 1.5708
    c: Tangent(g90,g83) = 1.5708
    c: Horizontal(g86)
    c: Horizontal(g90)
    c: Vertical(g84)
    c: Vertical(g88)
    c: Equal(g83,g85)
    c: Equal(g85,g87)
    c: Equal(g87,g89)
    c: PointOnObject(g91,g84)
    c: PointOnObject(g91,g90)
    c: PointOnObject(g92,g86)
    c: PointOnObject(g92,g88)
    c: Tangent(g93,g94) = 1.5708
    c: Tangent(g94,g95) = 1.5708
    c: Tangent(g95,g96) = 1.5708
    c: Tangent(g96,g97) = 1.5708
    c: Tangent(g97,g98) = 1.5708
    c: Tangent(g98,g99) = 1.5708
    c: Tangent(g99,g100) = 1.5708
    c: Tangent(g100,g93) = 1.5708
    c: Horizontal(g96)
    c: Horizontal(g100)
    c: Vertical(g94)
    c: Vertical(g98)
    c: Equal(g93,g95)
    c: Equal(g95,g97)
    c: Equal(g97,g99)
    c: PointOnObject(g101,g94)
    c: PointOnObject(g101,g100)
    c: PointOnObject(g102,g96)
    c: PointOnObject(g102,g98)
    c: Tangent(g103,g104) = 1.5708
    c: Tangent(g104,g105) = 1.5708
    c: Tangent(g105,g106) = 1.5708
    c: Tangent(g106,g107) = 1.5708
    c: Tangent(g107,g108) = 1.5708
    c: Tangent(g108,g109) = 1.5708
    c: Tangent(g109,g110) = 1.5708
    c: Tangent(g110,g103) = 1.5708
    c: Horizontal(g106)
    c: Horizontal(g110)
    c: Vertical(g104)
    c: Vertical(g108)
    c: Equal(g103,g105)
    c: Equal(g105,g107)
    c: Equal(g107,g109)
    c: PointOnObject(g111,g104)
    c: PointOnObject(g111,g110)
    c: PointOnObject(g112,g106)
    c: PointOnObject(g112,g108)
    c: Tangent(g113,g114) = 1.5708
    c: Tangent(g114,g115) = 1.5708
    c: Tangent(g115,g116) = 1.5708
    c: Tangent(g116,g117) = 1.5708
    c: Tangent(g117,g118) = 1.5708
    c: Tangent(g118,g119) = 1.5708
    c: Tangent(g119,g120) = 1.5708
    c: Tangent(g120,g113) = 1.5708
    c: Horizontal(g116)
    c: Horizontal(g120)
    c: Vertical(g114)
    c: Vertical(g118)
    c: Equal(g113,g115)
    c: Equal(g115,g117)
    c: Equal(g117,g119)
    c: PointOnObject(g121,g114)
    c: PointOnObject(g121,g120)
    c: PointOnObject(g122,g116)
    c: PointOnObject(g122,g118)
    c: Equal(g53,g49)
    c: Equal(g54,g48)
    c: Equal(g46,g56)
    c: Equal(g63,g59)
    c: Equal(g58,g64)
    c: Equal(g70,g60)
    c: Equal(g80,g70)
    c: Equal(g73,g69)
    c: Equal(g74,g68)
    c: Equal(g78,g84)
    c: Equal(g83,g79)
    c: Equal(g90,g80)
    c: Equal(g93,g89)
    c: Equal(g99,g103)
    c: Equal(g104,g98)
    c: Equal(g94,g88)
    c: Equal(g110,g100)
    c: Equal(g100,g90)
    c: Equal(g113,g109)
    c: Coincident(g123,g113)
    c: Coincident(g123,g108)
    c: Coincident(g124,g103)
    c: Coincident(g124,g98)
    c: Coincident(g125,g93)
    c: Coincident(g125,g88)
    c: Coincident(g126,g83)
    c: Coincident(g126,g78)
    c: Coincident(g127,g73)
    c: Coincident(g127,g68)
    c: Coincident(g128,g63)
    c: Coincident(g128,g58)
    c: Coincident(g129,g53)
    c: Coincident(g129,g48)
    c: Equal(g129,g128)
    c: Equal(g127,g128)
    c: Equal(g126,g127)
    c: Equal(g125,g126)
    c: Equal(g124,g125)
    c: Equal(g123,g124)
    c: Equal(g114,g108)
    c: Equal(g110,g120)
    c: Coincident(g130,g43)
    c: Coincident(g130,g38)
    c: Tangent(g131,g132) = 1.5708
    c: Tangent(g132,g133) = 1.5708
    c: Tangent(g133,g134) = 1.5708
    c: Tangent(g134,g135) = 1.5708
    c: Tangent(g135,g136) = 1.5708
    c: Tangent(g136,g137) = 1.5708
    c: Tangent(g137,g138) = 1.5708
    c: Tangent(g138,g131) = 1.5708
    c: Horizontal(g134)
    c: Horizontal(g138)
    c: Vertical(g132)
    c: Vertical(g136)
    c: Equal(g131,g133)
    c: Equal(g133,g135)
    c: Equal(g135,g137)
    c: PointOnObject(g139,g132)
    c: PointOnObject(g139,g138)
    c: PointOnObject(g140,g134)
    c: PointOnObject(g140,g136)
    c: Tangent(g141,g142) = 1.5708
    c: Tangent(g142,g143) = 1.5708
    c: Tangent(g143,g144) = 1.5708
    c: Tangent(g144,g145) = 1.5708
    c: Tangent(g145,g146) = 1.5708
    c: Tangent(g146,g147) = 1.5708
    c: Tangent(g147,g148) = 1.5708
    c: Tangent(g148,g141) = 1.5708
    c: Horizontal(g144)
    c: Horizontal(g148)
    c: Vertical(g142)
    c: Vertical(g146)
    c: Equal(g141,g143)
    c: Equal(g143,g145)
    c: Equal(g145,g147)
    c: PointOnObject(g149,g142)
    c: PointOnObject(g149,g148)
    c: PointOnObject(g150,g144)
    c: PointOnObject(g150,g146)
    c: Tangent(g151,g152) = 1.5708
    c: Tangent(g152,g153) = 1.5708
    c: Tangent(g153,g154) = 1.5708
    c: Tangent(g154,g155) = 1.5708
    c: Tangent(g155,g156) = 1.5708
    c: Tangent(g156,g157) = 1.5708
    c: Tangent(g157,g158) = 1.5708
    c: Tangent(g158,g151) = 1.5708
    c: Horizontal(g154)
    c: Horizontal(g158)
    c: Vertical(g152)
    c: Vertical(g156)
    c: Equal(g151,g153)
    c: Equal(g153,g155)
    c: Equal(g155,g157)
    c: PointOnObject(g159,g152)
    c: PointOnObject(g159,g158)
    c: Equal(g152,g146)
    c: Equal(g151,g147)
    c: Equal(g141,g137)
    c: Equal(g136,g142)
    c: Equal(g148,g138)
    c: Equal(g132,g118)
    c: Equal(g119,g131)
    c: Equal(g138,g120)
    c: Coincident(g160,g151)
    c: Coincident(g160,g146)
    c: Coincident(g161,g141)
    c: Coincident(g161,g136)
    c: DistanceX(g48,g43) = 15.5
    c: Equal(g158,g148)
    c: Tangent(g162,g163) = 1.5708
    c: Tangent(g163,g164) = 1.5708
    c: Tangent(g164,g165) = 1.5708
    c: Tangent(g165,g166) = 1.5708
    c: Tangent(g166,g167) = 1.5708
    c: Tangent(g167,g168) = 1.5708
    c: Tangent(g168,g169) = 1.5708
    c: Tangent(g169,g162) = 1.5708
    c: Horizontal(g163)
    c: Horizontal(g167)
    c: Vertical(g165)
    c: Vertical(g169)
    c: Equal(g162,g164)
    c: Equal(g164,g166)
    c: Equal(g166,g168)
    c: PointOnObject(g170,g163)
    c: PointOnObject(g170,g169)
    c: PointOnObject(g171,g165)
    c: PointOnObject(g171,g167)
    c: Coincident(g170,g29)
    c: Tangent(g172,g173) = 1.5708
    c: Tangent(g173,g174) = 1.5708
    c: Tangent(g174,g175) = 1.5708
    c: Tangent(g175,g176) = 1.5708
    c: Tangent(g176,g177) = 1.5708
    c: Tangent(g177,g178) = 1.5708
    c: Tangent(g178,g179) = 1.5708
    c: Tangent(g179,g172) = 1.5708
    c: Horizontal(g173)
    c: Horizontal(g177)
    c: Vertical(g175)
    c: Vertical(g179)
    c: Equal(g172,g174)
    c: Equal(g174,g176)
    c: Equal(g176,g178)
    c: PointOnObject(g180,g173)
    c: PointOnObject(g180,g179)
    c: PointOnObject(g181,g175)
    c: PointOnObject(g181,g177)
    c: Equal(g164,g172)
    c: Equal(g165,g179)
    c: Equal(g175,g156)
    c: Equal(g174,g157)
    c: Coincident(g182,g164)
    c: Coincident(g182,g172)
    c: Coincident(g183,g174)
    c: Coincident(g183,g156)
    c: Equal(g173,g158)
    c: Equal(g163,g40)
    c: Equal(g130,g129)
    c: Tangent(g184,g185) = 1.5708
    c: Tangent(g185,g186) = 1.5708
    c: Tangent(g186,g187) = 1.5708
    c: Tangent(g187,g188) = 1.5708
    c: Tangent(g188,g189) = 1.5708
    c: Tangent(g189,g190) = 1.5708
    c: Tangent(g190,g191) = 1.5708
    c: Tangent(g191,g184) = 1.5708
    c: Horizontal(g187)
    c: Horizontal(g191)
    c: Vertical(g185)
    c: Vertical(g189)
    c: Equal(g184,g186)
    c: Equal(g186,g188)
    c: Equal(g188,g190)
    c: PointOnObject(g192,g185)
    c: PointOnObject(g192,g191)
    c: PointOnObject(g193,g187)
    c: PointOnObject(g193,g189)
    c: Equal(g35,g184)
    c: Coincident(g194,g35)
    c: Coincident(g194,g184)
    c: Vertical(g194)
    c: Equal(g46,g185)
    c: DistanceX(g189,g184) = 29.5
    c: Tangent(g195,g196) = 1.5708
    c: Tangent(g196,g197) = 1.5708
    c: Tangent(g197,g198) = 1.5708
    c: Tangent(g198,g199) = 1.5708
    c: Tangent(g199,g200) = 1.5708
    c: Tangent(g200,g201) = 1.5708
    c: Tangent(g201,g202) = 1.5708
    c: Tangent(g202,g195) = 1.5708
    c: Horizontal(g198)
    c: Horizontal(g202)
    c: Vertical(g196)
    c: Vertical(g200)
    c: Equal(g195,g197)
    c: Equal(g197,g199)
    c: Equal(g199,g201)
    c: PointOnObject(g203,g196)
    c: PointOnObject(g203,g202)
    c: PointOnObject(g204,g198)
    c: PointOnObject(g204,g200)
    c: Tangent(g205,g206) = 1.5708
    c: Tangent(g206,g207) = 1.5708
    c: Tangent(g207,g208) = 1.5708
    c: Tangent(g208,g209) = 1.5708
    c: Tangent(g209,g210) = 1.5708
    c: Tangent(g210,g211) = 1.5708
    c: Tangent(g211,g212) = 1.5708
    c: Tangent(g212,g205) = 1.5708
    c: Horizontal(g208)
    c: Horizontal(g212)
    c: Vertical(g206)
    c: Vertical(g210)
    c: Equal(g205,g207)
    c: Equal(g207,g209)
    c: Equal(g209,g211)
    c: PointOnObject(g213,g206)
    c: PointOnObject(g213,g212)
    c: PointOnObject(g214,g208)
    c: PointOnObject(g214,g210)
    c: Tangent(g215,g216) = 1.5708
    c: Tangent(g216,g217) = 1.5708
    c: Tangent(g217,g218) = 1.5708
    c: Tangent(g218,g219) = 1.5708
    c: Tangent(g219,g220) = 1.5708
    c: Tangent(g220,g221) = 1.5708
    c: Tangent(g221,g222) = 1.5708
    c: Tangent(g222,g215) = 1.5708
    c: Horizontal(g218)
    c: Horizontal(g222)
    c: Vertical(g216)
    c: Vertical(g220)
    c: Equal(g215,g217)
    c: Equal(g217,g219)
    c: Equal(g219,g221)
    c: PointOnObject(g223,g216)
    c: PointOnObject(g223,g222)
    c: PointOnObject(g224,g218)
    c: PointOnObject(g224,g220)
    c: Equal(g215,g207)
    c: Equal(g205,g197)
    c: Equal(g195,g186)
    c: Coincident(g225,g186)
    c: Coincident(g225,g195)
    c: Coincident(g226,g197)
    c: Coincident(g226,g205)
    c: Coincident(g227,g207)
    c: Coincident(g227,g215)
    c: Equal(g227,g226)
    c: Equal(g226,g225)
    c: Equal(g194,g225)
    c: Equal(g196,g206)
    c: Equal(g206,g216)
    c: Equal(g185,g196)
    c: DistanceX(g200,g195) = 20.5
    c: DistanceX(g210,g205) = 34.875
    c: DistanceX(g220,g215) = 43.7875
    c: Tangent(g228,g229) = 1.5708
    c: Tangent(g229,g230) = 1.5708
    c: Tangent(g230,g231) = 1.5708
    c: Tangent(g231,g232) = 1.5708
    c: Tangent(g232,g233) = 1.5708
    c: Tangent(g233,g234) = 1.5708
    c: Tangent(g234,g235) = 1.5708
    c: Tangent(g235,g228) = 1.5708
    c: Horizontal(g231)
    c: Horizontal(g235)
    c: Vertical(g229)
    c: Vertical(g233)
    c: Equal(g228,g230)
    c: Equal(g230,g232)
    c: Equal(g232,g234)
    c: PointOnObject(g236,g229)
    c: PointOnObject(g236,g235)
    c: PointOnObject(g237,g231)
    c: PointOnObject(g237,g233)
    c: Coincident(g236,g32)
    c: Coincident(g237,g26)
    c: Radius(g228) = 1.25
    c: PointOnObject(g43,g235)
    c: PointOnObject(g53,g235)
    c: PointOnObject(g63,g235)
    c: PointOnObject(g73,g235)
    c: PointOnObject(g83,g235)
    c: PointOnObject(g93,g235)
    c: PointOnObject(g103,g235)
    c: PointOnObject(g113,g235)
    c: PointOnObject(g131,g235)
    c: PointOnObject(g141,g235)
    c: PointOnObject(g151,g235)
    c: PointOnObject(g173,g235)
    c: PointOnObject(g168,g233)
    c: Coincident(g238,g33)
    c: PointOnObject(g238,g13)
    c: Horizontal(g238)
    c: Coincident(g239,g33)
    c: PointOnObject(g239,g19)
    c: Vertical(g239)
    c: Equal(g239,g238)
    c: DistanceX(g238,g238) = 4.5
    c: Equal(g182,g183)
    c: Coincident(g240,g118)
    c: Coincident(g240,g131)
    c: Equal(g183,g160)
    c: Equal(g160,g161)
    c: Equal(g161,g240)
    c: Equal(g240,g123)
    c: PointOnObject(g195,g229)
    c: PointOnObject(g205,g229)
    c: PointOnObject(g215,g229)
    c: Coincident(g241,g230)
    c: PointOnObject(g241,g20)
    c: Vertical(g241)
    c: Equal(g241,g238)
    c: Tangent(g242,g243) = 1.5708
    c: Tangent(g243,g244) = 1.5708
    c: Tangent(g244,g245) = 1.5708
    c: Tangent(g245,g246) = 1.5708
    c: Tangent(g246,g247) = 1.5708
    c: Tangent(g247,g248) = 1.5708
    c: Tangent(g248,g249) = 1.5708
    c: Tangent(g249,g242) = 1.5708
    c: Horizontal(g245)
    c: Horizontal(g249)
    c: Vertical(g243)
    c: Vertical(g247)
    c: Equal(g242,g244)
    c: Equal(g244,g246)
    c: Equal(g246,g248)
    c: PointOnObject(g250,g243)
    c: PointOnObject(g250,g249)
    c: PointOnObject(g251,g245)
    c: PointOnObject(g251,g247)
    c: PointOnObject(g250,g229)
    c: PointOnObject(g251,g231)
    c: Equal(g217,g242)
    c: Equal(g216,g243)
    c: Coincident(g252,g217)
    c: Coincident(g252,g242)
    c: Equal(g227,g252)
    c: Coincident(g253,g242)
    c: PointOnObject(g253,g233)
    c: Horizontal(g253)
    c: Coincident(g254,g217)
    c: PointOnObject(g254,g233)
    c: Horizontal(g254)
    c: Coincident(g255,g215)
    c: PointOnObject(g255,g233)
    c: Horizontal(g255)
    c: Coincident(g256,g207)
    c: PointOnObject(g256,g233)
    c: Horizontal(g256)
    c: Coincident(g257,g205)
    c: PointOnObject(g257,g233)
    c: Horizontal(g257)
    c: Coincident(g258,g197)
    c: PointOnObject(g258,g233)
    c: Horizontal(g258)
    c: Coincident(g259,g195)
    c: PointOnObject(g259,g233)
    c: Horizontal(g259)
    c: Coincident(g260,g186)
    c: PointOnObject(g260,g233)
    c: Horizontal(g260)
    c: Coincident(g261,g184)
    c: PointOnObject(g261,g233)
    c: Horizontal(g261)
    c: DistanceX(g246,g243) = 18.5
FEATURE [Sketcher::SketchObject] Sketch
  ExternalGeometry = -> [Sketch009]
  FullyConstrained = true
  MapMode = 2
  Placement = pos=(0,0,12.53) rot=(0,0,1;0rad)
  Support = -> [Sketch009]
  sketch-geometry (291):
    g0: ArcOfCircle CenterX=10.75 CenterY=198.73 CenterZ=0 NormalX=0 NormalY=0 NormalZ=1 AngleXU=0 Radius=1.25 StartAngle=1.5708 EndAngle=3.14159
    g1: LineSegment StartX=10.75 StartY=199.98 StartZ=0 EndX=285.88 EndY=199.98 EndZ=0
    g2: ArcOfCircle CenterX=285.88 CenterY=198.73 CenterZ=0 NormalX=0 NormalY=0 NormalZ=1 AngleXU=0 Radius=1.25 StartAngle=-2.7e-15 EndAngle=1.5708
    g3: LineSegment StartX=287.13 StartY=198.73 StartZ=0 EndX=287.13 EndY=95.75 EndZ=0
    g4: ArcOfCircle CenterX=285.88 CenterY=95.75 CenterZ=0 NormalX=0 NormalY=0 NormalZ=1 AngleXU=0 Radius=1.25 StartAngle=4.71239 EndAngle=6.28319
    g5: LineSegment StartX=285.88 StartY=94.5 StartZ=0 EndX=10.75 EndY=94.5 EndZ=0
    g6: ArcOfCircle CenterX=10.75 CenterY=95.75 CenterZ=0 NormalX=0 NormalY=0 NormalZ=1 AngleXU=0 Radius=1.25 StartAngle=3.14159 EndAngle=4.71239
    g7: LineSegment StartX=9.5 StartY=95.75 StartZ=0 EndX=9.5 EndY=198.73 EndZ=0
    g8: GeomPoint X=9.5 Y=199.98 Z=0
    g9: GeomPoint X=287.13 Y=94.5 Z=0
    g10: LineSegment StartX=258.88 StartY=186.634 StartZ=0 EndX=9.5 EndY=186.634 EndZ=0
    g11: LineSegment StartX=258.88 StartY=171.134 StartZ=0 EndX=9.5 EndY=171.134 EndZ=0
    g12: LineSegment StartX=269.88 StartY=110 StartZ=0 EndX=9.5 EndY=110 EndZ=0
    g13: ArcOfCircle CenterX=252.793 CenterY=185.384 CenterZ=0 NormalX=0 NormalY=0 NormalZ=1 AngleXU=0 Radius=1.25 StartAngle=-8.9e-15 EndAngle=1.5708
    g14: LineSegment StartX=254.043 StartY=185.384 StartZ=0 EndX=254.043 EndY=172.384 EndZ=0
    g15: ArcOfCircle CenterX=252.793 CenterY=172.384 CenterZ=0 NormalX=0 NormalY=0 NormalZ=1 AngleXU=0 Radius=1.25 StartAngle=4.71239 EndAngle=6.28319
    g16: LineSegment StartX=252.793 StartY=171.134 StartZ=0 EndX=239.793 EndY=171.134 EndZ=0
    g17: ArcOfCircle CenterX=239.793 CenterY=172.384 CenterZ=0 NormalX=0 NormalY=0 NormalZ=1 AngleXU=0 Radius=1.25 StartAngle=3.14159 EndAngle=4.71239
    g18: LineSegment StartX=238.543 StartY=172.384 StartZ=0 EndX=238.543 EndY=185.384 EndZ=0
    g19: ArcOfCircle CenterX=239.793 CenterY=185.384 CenterZ=0 NormalX=0 NormalY=0 NormalZ=1 AngleXU=0 Radius=1.25 StartAngle=1.5708 EndAngle=3.14159
    g20: LineSegment StartX=239.793 StartY=186.634 StartZ=0 EndX=252.793 EndY=186.634 EndZ=0
    g21: GeomPoint X=254.043 Y=186.634 Z=0
    g22: GeomPoint X=238.543 Y=171.134 Z=0
    g23: ArcOfCircle CenterX=233.706 CenterY=185.384 CenterZ=0 NormalX=0 NormalY=0 NormalZ=1 AngleXU=0 Radius=1.25 StartAngle=-1.8e-15 EndAngle=1.5708
    g24: LineSegment StartX=234.956 StartY=185.384 StartZ=0 EndX=234.956 EndY=172.384 EndZ=0
    g25: ArcOfCircle CenterX=233.706 CenterY=172.384 CenterZ=0 NormalX=0 NormalY=0 NormalZ=1 AngleXU=0 Radius=1.25 StartAngle=4.71239 EndAngle=6.28319
    g26: LineSegment StartX=233.706 StartY=171.134 StartZ=0 EndX=220.706 EndY=171.134 EndZ=0
    g27: ArcOfCircle CenterX=220.706 CenterY=172.384 CenterZ=0 NormalX=0 NormalY=0 NormalZ=1 AngleXU=0 Radius=1.25 StartAngle=3.14159 EndAngle=4.71239
    g28: LineSegment StartX=219.456 StartY=172.384 StartZ=0 EndX=219.456 EndY=185.384 EndZ=0
    g29: ArcOfCircle CenterX=220.706 CenterY=185.384 CenterZ=0 NormalX=0 NormalY=0 NormalZ=1 AngleXU=0 Radius=1.25 StartAngle=1.5708 EndAngle=3.14159
    g30: LineSegment StartX=220.706 StartY=186.634 StartZ=0 EndX=233.706 EndY=186.634 EndZ=0
    g31: GeomPoint X=234.956 Y=186.634 Z=0
    g32: GeomPoint X=219.456 Y=171.134 Z=0
    g33: ArcOfCircle CenterX=214.619 CenterY=185.384 CenterZ=0 NormalX=0 NormalY=0 NormalZ=1 AngleXU=0 Radius=1.25 StartAngle=-4.4e-15 EndAngle=1.5708
    g34: LineSegment StartX=215.869 StartY=185.384 StartZ=0 EndX=215.869 EndY=172.384 EndZ=0
    g35: ArcOfCircle CenterX=214.619 CenterY=172.384 CenterZ=0 NormalX=0 NormalY=0 NormalZ=1 AngleXU=0 Radius=1.25 StartAngle=4.71239 EndAngle=6.28319
    g36: LineSegment StartX=214.619 StartY=171.134 StartZ=0 EndX=201.619 EndY=171.134 EndZ=0
    g37: ArcOfCircle CenterX=201.619 CenterY=172.384 CenterZ=0 NormalX=0 NormalY=0 NormalZ=1 AngleXU=0 Radius=1.25 StartAngle=3.14159 EndAngle=4.71239
    g38: LineSegment StartX=200.369 StartY=172.384 StartZ=0 EndX=200.369 EndY=185.384 EndZ=0
    g39: ArcOfCircle CenterX=201.619 CenterY=185.384 CenterZ=0 NormalX=0 NormalY=0 NormalZ=1 AngleXU=0 Radius=1.25 StartAngle=1.5708 EndAngle=3.14159
    g40: LineSegment StartX=201.619 StartY=186.634 StartZ=0 EndX=214.619 EndY=186.634 EndZ=0
    g41: GeomPoint X=215.869 Y=186.634 Z=0
    g42: GeomPoint X=200.369 Y=171.134 Z=0
    g43: ArcOfCircle CenterX=195.532 CenterY=185.384 CenterZ=0 NormalX=0 NormalY=0 NormalZ=1 AngleXU=0 Radius=1.25 StartAngle=-8e-15 EndAngle=1.5708
    g44: LineSegment StartX=196.782 StartY=185.384 StartZ=0 EndX=196.782 EndY=172.384 EndZ=0
    g45: ArcOfCircle CenterX=195.532 CenterY=172.384 CenterZ=0 NormalX=0 NormalY=0 NormalZ=1 AngleXU=0 Radius=1.25 StartAngle=4.71239 EndAngle=6.28319
    g46: LineSegment StartX=195.532 StartY=171.134 StartZ=0 EndX=182.532 EndY=171.134 EndZ=0
    g47: ArcOfCircle CenterX=182.532 CenterY=172.384 CenterZ=0 NormalX=0 NormalY=0 NormalZ=1 AngleXU=0 Radius=1.25 StartAngle=3.14159 EndAngle=4.71239
    g48: LineSegment StartX=181.282 StartY=172.384 StartZ=0 EndX=181.282 EndY=185.384 EndZ=0
    g49: ArcOfCircle CenterX=182.532 CenterY=185.384 CenterZ=0 NormalX=0 NormalY=0 NormalZ=1 AngleXU=0 Radius=1.25 StartAngle=1.5708 EndAngle=3.14159
    g50: LineSegment StartX=182.532 StartY=186.634 StartZ=0 EndX=195.532 EndY=186.634 EndZ=0
    g51: GeomPoint X=196.782 Y=186.634 Z=0
    g52: GeomPoint X=181.282 Y=171.134 Z=0
    g53: ArcOfCircle CenterX=176.445 CenterY=185.384 CenterZ=0 NormalX=0 NormalY=0 NormalZ=1 AngleXU=0 Radius=1.25 StartAngle=1.12e-14 EndAngle=1.5708
    g54: LineSegment StartX=177.695 StartY=185.384 StartZ=0 EndX=177.695 EndY=172.384 EndZ=0
    g55: ArcOfCircle CenterX=176.445 CenterY=172.384 CenterZ=0 NormalX=0 NormalY=0 NormalZ=1 AngleXU=0 Radius=1.25 StartAngle=4.71239 EndAngle=6.28319
    g56: LineSegment StartX=176.445 StartY=171.134 StartZ=0 EndX=163.445 EndY=171.134 EndZ=0
    g57: ArcOfCircle CenterX=163.445 CenterY=172.384 CenterZ=0 NormalX=0 NormalY=0 NormalZ=1 AngleXU=0 Radius=1.25 StartAngle=3.14159 EndAngle=4.71239
    g58: LineSegment StartX=162.195 StartY=172.384 StartZ=0 EndX=162.195 EndY=185.384 EndZ=0
    g59: ArcOfCircle CenterX=163.445 CenterY=185.384 CenterZ=0 NormalX=0 NormalY=0 NormalZ=1 AngleXU=0 Radius=1.25 StartAngle=1.5708 EndAngle=3.14159
    g60: LineSegment StartX=163.445 StartY=186.634 StartZ=0 EndX=176.445 EndY=186.634 EndZ=0
    g61: GeomPoint X=177.695 Y=186.634 Z=0
    g62: GeomPoint X=162.195 Y=171.134 Z=0
    g63: ArcOfCircle CenterX=157.358 CenterY=185.384 CenterZ=0 NormalX=0 NormalY=0 NormalZ=1 AngleXU=0 Radius=1.25 StartAngle=4.4e-15 EndAngle=1.5708
    g64: LineSegment StartX=158.608 StartY=185.384 StartZ=0 EndX=158.608 EndY=172.384 EndZ=0
    g65: ArcOfCircle CenterX=157.358 CenterY=172.384 CenterZ=0 NormalX=0 NormalY=0 NormalZ=1 AngleXU=0 Radius=1.25 StartAngle=4.71239 EndAngle=6.28319
    g66: LineSegment StartX=157.358 StartY=171.134 StartZ=0 EndX=144.358 EndY=171.134 EndZ=0
    g67: ArcOfCircle CenterX=144.358 CenterY=172.384 CenterZ=0 NormalX=0 NormalY=0 NormalZ=1 AngleXU=0 Radius=1.25 StartAngle=3.14159 EndAngle=4.71239
    g68: LineSegment StartX=143.108 StartY=172.384 StartZ=0 EndX=143.108 EndY=185.384 EndZ=0
    g69: ArcOfCircle CenterX=144.358 CenterY=185.384 CenterZ=0 NormalX=0 NormalY=0 NormalZ=1 AngleXU=0 Radius=1.25 StartAngle=1.5708 EndAngle=3.14159
    g70: LineSegment StartX=144.358 StartY=186.634 StartZ=0 EndX=157.358 EndY=186.634 EndZ=0
    g71: GeomPoint X=158.608 Y=186.634 Z=0
    g72: GeomPoint X=143.108 Y=171.134 Z=0
    g73: ArcOfCircle CenterX=138.272 CenterY=185.384 CenterZ=0 NormalX=0 NormalY=0 NormalZ=1 AngleXU=0 Radius=1.25 StartAngle=9e-16 EndAngle=1.5708
    g74: LineSegment StartX=139.522 StartY=185.384 StartZ=0 EndX=139.522 EndY=172.384 EndZ=0
    g75: ArcOfCircle CenterX=138.272 CenterY=172.384 CenterZ=0 NormalX=0 NormalY=0 NormalZ=1 AngleXU=0 Radius=1.25 StartAngle=4.71239 EndAngle=6.28319
    g76: LineSegment StartX=138.272 StartY=171.134 StartZ=0 EndX=125.272 EndY=171.134 EndZ=0
    g77: ArcOfCircle CenterX=125.272 CenterY=172.384 CenterZ=0 NormalX=0 NormalY=0 NormalZ=1 AngleXU=0 Radius=1.25 StartAngle=3.14159 EndAngle=4.71239
    g78: LineSegment StartX=124.022 StartY=172.384 StartZ=0 EndX=124.022 EndY=185.384 EndZ=0
    g79: ArcOfCircle CenterX=125.272 CenterY=185.384 CenterZ=0 NormalX=0 NormalY=0 NormalZ=1 AngleXU=0 Radius=1.25 StartAngle=1.5708 EndAngle=3.14159
    g80: LineSegment StartX=125.272 StartY=186.634 StartZ=0 EndX=138.272 EndY=186.634 EndZ=0
    g81: GeomPoint X=139.522 Y=186.634 Z=0
    g82: GeomPoint X=124.022 Y=171.134 Z=0
    g83: ArcOfCircle CenterX=119.185 CenterY=185.384 CenterZ=0 NormalX=0 NormalY=0 NormalZ=1 AngleXU=0 Radius=1.25 StartAngle=1.05e-14 EndAngle=1.5708
    g84: LineSegment StartX=120.435 StartY=185.384 StartZ=0 EndX=120.435 EndY=172.384 EndZ=0
    g85: ArcOfCircle CenterX=119.185 CenterY=172.384 CenterZ=0 NormalX=0 NormalY=0 NormalZ=1 AngleXU=0 Radius=1.25 StartAngle=4.71239 EndAngle=6.28319
    g86: LineSegment StartX=119.185 StartY=171.134 StartZ=0 EndX=106.185 EndY=171.134 EndZ=0
    g87: ArcOfCircle CenterX=106.185 CenterY=172.384 CenterZ=0 NormalX=0 NormalY=0 NormalZ=1 AngleXU=0 Radius=1.25 StartAngle=3.14159 EndAngle=4.71239
    g88: LineSegment StartX=104.935 StartY=172.384 StartZ=0 EndX=104.935 EndY=185.384 EndZ=0
    g89: ArcOfCircle CenterX=106.185 CenterY=185.384 CenterZ=0 NormalX=0 NormalY=0 NormalZ=1 AngleXU=0 Radius=1.25 StartAngle=1.5708 EndAngle=3.14159
    g90: LineSegment StartX=106.185 StartY=186.634 StartZ=0 EndX=119.185 EndY=186.634 EndZ=0
    g91: GeomPoint X=120.435 Y=186.634 Z=0
    g92: GeomPoint X=104.935 Y=171.134 Z=0
    g93: ArcOfCircle CenterX=100.098 CenterY=185.384 CenterZ=0 NormalX=0 NormalY=0 NormalZ=1 AngleXU=0 Radius=1.25 StartAngle=-1.8e-15 EndAngle=1.5708
    g94: LineSegment StartX=101.348 StartY=185.384 StartZ=0 EndX=101.348 EndY=172.384 EndZ=0
    g95: ArcOfCircle CenterX=100.098 CenterY=172.384 CenterZ=0 NormalX=0 NormalY=0 NormalZ=1 AngleXU=0 Radius=1.25 StartAngle=4.71239 EndAngle=6.28319
    g96: LineSegment StartX=100.098 StartY=171.134 StartZ=0 EndX=87.0977 EndY=171.134 EndZ=0
    g97: ArcOfCircle CenterX=87.0977 CenterY=172.384 CenterZ=0 NormalX=0 NormalY=0 NormalZ=1 AngleXU=0 Radius=1.25 StartAngle=3.14159 EndAngle=4.71239
    g98: LineSegment StartX=85.8477 StartY=172.384 StartZ=0 EndX=85.8477 EndY=185.384 EndZ=0
    g99: ArcOfCircle CenterX=87.0977 CenterY=185.384 CenterZ=0 NormalX=0 NormalY=0 NormalZ=1 AngleXU=0 Radius=1.25 StartAngle=1.5708 EndAngle=3.14159
    g100: LineSegment StartX=87.0977 StartY=186.634 StartZ=0 EndX=100.098 EndY=186.634 EndZ=0
    g101: GeomPoint X=101.348 Y=186.634 Z=0
    g102: GeomPoint X=85.8477 Y=171.134 Z=0
    g103: ArcOfCircle CenterX=81.0108 CenterY=185.384 CenterZ=0 NormalX=0 NormalY=0 NormalZ=1 AngleXU=0 Radius=1.25 StartAngle=1.4e-15 EndAngle=1.5708
    g104: LineSegment StartX=82.2608 StartY=185.384 StartZ=0 EndX=82.2608 EndY=172.384 EndZ=0
    g105: ArcOfCircle CenterX=81.0108 CenterY=172.384 CenterZ=0 NormalX=0 NormalY=0 NormalZ=1 AngleXU=0 Radius=1.25 StartAngle=4.71239 EndAngle=6.28319
    g106: LineSegment StartX=81.0108 StartY=171.134 StartZ=0 EndX=68.0108 EndY=171.134 EndZ=0
    g107: ArcOfCircle CenterX=68.0108 CenterY=172.384 CenterZ=0 NormalX=0 NormalY=0 NormalZ=1 AngleXU=0 Radius=1.25 StartAngle=3.14159 EndAngle=4.71239
    g108: LineSegment StartX=66.7608 StartY=172.384 StartZ=0 EndX=66.7608 EndY=185.384 EndZ=0
    g109: ArcOfCircle CenterX=68.0108 CenterY=185.384 CenterZ=0 NormalX=0 NormalY=0 NormalZ=1 AngleXU=0 Radius=1.25 StartAngle=1.5708 EndAngle=3.14159
    g110: LineSegment StartX=68.0108 StartY=186.634 StartZ=0 EndX=81.0108 EndY=186.634 EndZ=0
    g111: GeomPoint X=82.2608 Y=186.634 Z=0
    g112: GeomPoint X=66.7608 Y=171.134 Z=0
    g113: ArcOfCircle CenterX=61.9238 CenterY=185.384 CenterZ=0 NormalX=0 NormalY=0 NormalZ=1 AngleXU=0 Radius=1.25 StartAngle=-4.4e-15 EndAngle=1.5708
    g114: LineSegment StartX=63.1738 StartY=185.384 StartZ=0 EndX=63.1738 EndY=172.384 EndZ=0
    g115: ArcOfCircle CenterX=61.9238 CenterY=172.384 CenterZ=0 NormalX=0 NormalY=0 NormalZ=1 AngleXU=0 Radius=1.25 StartAngle=4.71239 EndAngle=6.28319
    g116: LineSegment StartX=61.9238 StartY=171.134 StartZ=0 EndX=48.9238 EndY=171.134 EndZ=0
    g117: ArcOfCircle CenterX=48.9238 CenterY=172.384 CenterZ=0 NormalX=0 NormalY=0 NormalZ=1 AngleXU=0 Radius=1.25 StartAngle=3.14159 EndAngle=4.71239
    g118: LineSegment StartX=47.6738 StartY=172.384 StartZ=0 EndX=47.6738 EndY=185.384 EndZ=0
    g119: ArcOfCircle CenterX=48.9238 CenterY=185.384 CenterZ=0 NormalX=0 NormalY=0 NormalZ=1 AngleXU=0 Radius=1.25 StartAngle=1.5708 EndAngle=3.14159
    g120: LineSegment StartX=48.9238 StartY=186.634 StartZ=0 EndX=61.9238 EndY=186.634 EndZ=0
    g121: GeomPoint X=63.1738 Y=186.634 Z=0
    g122: GeomPoint X=47.6738 Y=171.134 Z=0
    g123: ArcOfCircle CenterX=42.8369 CenterY=185.384 CenterZ=0 NormalX=0 NormalY=0 NormalZ=1 AngleXU=0 Radius=1.25 StartAngle=2.5e-15 EndAngle=1.5708
    g124: LineSegment StartX=44.0869 StartY=185.384 StartZ=0 EndX=44.0869 EndY=172.384 EndZ=0
    g125: ArcOfCircle CenterX=42.8369 CenterY=172.384 CenterZ=0 NormalX=0 NormalY=0 NormalZ=1 AngleXU=0 Radius=1.25 StartAngle=4.71239 EndAngle=6.28319
    g126: LineSegment StartX=42.8369 StartY=171.134 StartZ=0 EndX=29.8369 EndY=171.134 EndZ=0
    g127: ArcOfCircle CenterX=29.8369 CenterY=172.384 CenterZ=0 NormalX=0 NormalY=0 NormalZ=1 AngleXU=0 Radius=1.25 StartAngle=3.14159 EndAngle=4.71239
    g128: LineSegment StartX=28.5869 StartY=172.384 StartZ=0 EndX=28.5869 EndY=185.384 EndZ=0
    g129: ArcOfCircle CenterX=29.8369 CenterY=185.384 CenterZ=0 NormalX=0 NormalY=0 NormalZ=1 AngleXU=0 Radius=1.25 StartAngle=1.5708 EndAngle=3.14159
    g130: LineSegment StartX=29.8369 StartY=186.634 StartZ=0 EndX=42.8369 EndY=186.634 EndZ=0
    g131: GeomPoint X=44.0869 Y=186.634 Z=0
    g132: GeomPoint X=28.5869 Y=171.134 Z=0
    g133: ArcOfCircle CenterX=23.75 CenterY=185.384 CenterZ=0 NormalX=0 NormalY=0 NormalZ=1 AngleXU=0 Radius=1.25 StartAngle=9e-15 EndAngle=1.5708
    g134: LineSegment StartX=25 StartY=185.384 StartZ=0 EndX=25 EndY=172.384 EndZ=0
    g135: ArcOfCircle CenterX=23.75 CenterY=172.384 CenterZ=0 NormalX=0 NormalY=0 NormalZ=1 AngleXU=0 Radius=1.25 StartAngle=4.71239 EndAngle=6.28319
    g136: LineSegment StartX=23.75 StartY=171.134 StartZ=0 EndX=10.75 EndY=171.134 EndZ=0
    g137: ArcOfCircle CenterX=10.75 CenterY=172.384 CenterZ=0 NormalX=0 NormalY=0 NormalZ=1 AngleXU=0 Radius=1.25 StartAngle=3.14159 EndAngle=4.71239
    g138: LineSegment StartX=9.5 StartY=172.384 StartZ=0 EndX=9.5 EndY=185.384 EndZ=0
    g139: ArcOfCircle CenterX=10.75 CenterY=185.384 CenterZ=0 NormalX=0 NormalY=0 NormalZ=1 AngleXU=0 Radius=1.25 StartAngle=1.5708 EndAngle=3.14159
    g140: LineSegment StartX=10.75 StartY=186.634 StartZ=0 EndX=23.75 EndY=186.634 EndZ=0
    g141: GeomPoint X=25 Y=186.634 Z=0
    g142: GeomPoint X=9.5 Y=171.134 Z=0
    g143: LineSegment StartX=257.63 StartY=185.384 StartZ=0 EndX=254.043 EndY=185.384 EndZ=0
    g144: LineSegment StartX=238.543 StartY=185.384 StartZ=0 EndX=234.956 EndY=185.384 EndZ=0
    g145: LineSegment StartX=219.456 StartY=185.384 StartZ=0 EndX=215.869 EndY=185.384 EndZ=0
    g146: LineSegment StartX=200.369 StartY=185.384 StartZ=0 EndX=196.782 EndY=185.384 EndZ=0
    g147: LineSegment StartX=181.282 StartY=185.384 StartZ=0 EndX=177.695 EndY=185.384 EndZ=0
    g148: LineSegment StartX=162.195 StartY=185.384 StartZ=0 EndX=158.608 EndY=185.384 EndZ=0
    g149: LineSegment StartX=143.108 StartY=185.384 StartZ=0 EndX=139.522 EndY=185.384 EndZ=0
    g150: LineSegment StartX=124.022 StartY=185.384 StartZ=0 EndX=120.435 EndY=185.384 EndZ=0
    g151: LineSegment StartX=104.935 StartY=185.384 StartZ=0 EndX=101.348 EndY=185.384 EndZ=0
    g152: LineSegment StartX=85.8477 StartY=185.384 StartZ=0 EndX=82.2608 EndY=185.384 EndZ=0
    g153: LineSegment StartX=66.7608 StartY=185.384 StartZ=0 EndX=63.1738 EndY=185.384 EndZ=0
    g154: LineSegment StartX=47.6738 StartY=185.384 StartZ=0 EndX=44.0869 EndY=185.384 EndZ=0
    g155: LineSegment StartX=28.5869 StartY=185.384 StartZ=0 EndX=25 EndY=185.384 EndZ=0
    g156: ArcOfCircle CenterX=10.75 CenterY=153.226 CenterZ=0 NormalX=0 NormalY=0 NormalZ=1 AngleXU=0 Radius=1.25 StartAngle=3.14159 EndAngle=4.71239
    g157: LineSegment StartX=9.5 StartY=153.226 StartZ=0 EndX=9.5 EndY=166.226 EndZ=0
    g158: ArcOfCircle CenterX=10.75 CenterY=166.226 CenterZ=0 NormalX=0 NormalY=0 NormalZ=1 AngleXU=0 Radius=1.25 StartAngle=1.5708 EndAngle=3.14159
    g159: LineSegment StartX=10.75 StartY=167.476 StartZ=0 EndX=32.75 EndY=167.476 EndZ=0
    g160: ArcOfCircle CenterX=32.75 CenterY=166.226 CenterZ=0 NormalX=0 NormalY=0 NormalZ=1 AngleXU=0 Radius=1.25 StartAngle=1.11e-14 EndAngle=1.5708
    g161: LineSegment StartX=34 StartY=166.226 StartZ=0 EndX=34 EndY=153.226 EndZ=0
    g162: ArcOfCircle CenterX=32.75 CenterY=153.226 CenterZ=0 NormalX=0 NormalY=0 NormalZ=1 AngleXU=0 Radius=1.25 StartAngle=4.71239 EndAngle=6.28319
    g163: LineSegment StartX=32.75 StartY=151.976 StartZ=0 EndX=10.75 EndY=151.976 EndZ=0
    g164: GeomPoint X=9.5 Y=151.976 Z=0
    g165: GeomPoint X=34 Y=167.476 Z=0
    g166: ArcOfCircle CenterX=10.75 CenterY=134.067 CenterZ=0 NormalX=0 NormalY=0 NormalZ=1 AngleXU=0 Radius=1.25 StartAngle=3.14159 EndAngle=4.71239
    g167: LineSegment StartX=9.5 StartY=134.067 StartZ=0 EndX=9.5 EndY=147.067 EndZ=0
    g168: ArcOfCircle CenterX=10.75 CenterY=147.067 CenterZ=0 NormalX=0 NormalY=0 NormalZ=1 AngleXU=0 Radius=1.25 StartAngle=1.5708 EndAngle=3.14159
    g169: LineSegment StartX=10.75 StartY=148.317 StartZ=0 EndX=37.75 EndY=148.317 EndZ=0
    g170: ArcOfCircle CenterX=37.75 CenterY=147.067 CenterZ=0 NormalX=0 NormalY=0 NormalZ=1 AngleXU=0 Radius=1.25 StartAngle=1.6e-15 EndAngle=1.5708
    g171: LineSegment StartX=39 StartY=147.067 StartZ=0 EndX=39 EndY=134.067 EndZ=0
    g172: ArcOfCircle CenterX=37.75 CenterY=134.067 CenterZ=0 NormalX=0 NormalY=0 NormalZ=1 AngleXU=0 Radius=1.25 StartAngle=4.71239 EndAngle=6.28319
    g173: LineSegment StartX=37.75 StartY=132.817 StartZ=0 EndX=10.75 EndY=132.817 EndZ=0
    g174: GeomPoint X=9.5 Y=132.817 Z=0
    g175: GeomPoint X=39 Y=148.317 Z=0
    g176: ArcOfCircle CenterX=10.75 CenterY=114.909 CenterZ=0 NormalX=0 NormalY=0 NormalZ=1 AngleXU=0 Radius=1.25 StartAngle=3.14159 EndAngle=4.71239
    g177: LineSegment StartX=9.5 StartY=114.909 StartZ=0 EndX=9.5 EndY=127.909 EndZ=0
    g178: ArcOfCircle CenterX=10.75 CenterY=127.909 CenterZ=0 NormalX=0 NormalY=0 NormalZ=1 AngleXU=0 Radius=1.25 StartAngle=1.5708 EndAngle=3.14159
    g179: LineSegment StartX=10.75 StartY=129.159 StartZ=0 EndX=47.75 EndY=129.159 EndZ=0
    g180: ArcOfCircle CenterX=47.75 CenterY=127.909 CenterZ=0 NormalX=0 NormalY=0 NormalZ=1 AngleXU=0 Radius=1.25 StartAngle=-2.7e-15 EndAngle=1.5708
    g181: LineSegment StartX=49 StartY=127.909 StartZ=0 EndX=49 EndY=114.909 EndZ=0
    g182: ArcOfCircle CenterX=47.75 CenterY=114.909 CenterZ=0 NormalX=0 NormalY=0 NormalZ=1 AngleXU=0 Radius=1.25 StartAngle=4.71239 EndAngle=6.28319
    g183: LineSegment StartX=47.75 StartY=113.659 StartZ=0 EndX=10.75 EndY=113.659 EndZ=0
    g184: GeomPoint X=9.5 Y=113.659 Z=0
    g185: GeomPoint X=49 Y=129.159 Z=0
    g186: ArcOfCircle CenterX=10.75 CenterY=108.75 CenterZ=0 NormalX=0 NormalY=0 NormalZ=1 AngleXU=0 Radius=1.25 StartAngle=1.5708 EndAngle=3.14159
    g187: LineSegment StartX=10.75 StartY=110 StartZ=0 EndX=28.75 EndY=110 EndZ=0
    g188: ArcOfCircle CenterX=28.75 CenterY=108.75 CenterZ=0 NormalX=0 NormalY=0 NormalZ=1 AngleXU=0 Radius=1.25 StartAngle=4.4e-15 EndAngle=1.5708
    g189: LineSegment StartX=30 StartY=108.75 StartZ=0 EndX=30 EndY=95.75 EndZ=0
    g190: ArcOfCircle CenterX=28.75 CenterY=95.75 CenterZ=0 NormalX=0 NormalY=0 NormalZ=1 AngleXU=0 Radius=1.25 StartAngle=4.71239 EndAngle=6.28319
    g191: LineSegment StartX=28.75 StartY=94.5 StartZ=0 EndX=10.75 EndY=94.5 EndZ=0
    g192: ArcOfCircle CenterX=10.75 CenterY=95.75 CenterZ=0 NormalX=0 NormalY=0 NormalZ=1 AngleXU=0 Radius=1.25 StartAngle=3.14159 EndAngle=4.71239
    g193: LineSegment StartX=9.5 StartY=95.75 StartZ=0 EndX=9.5 EndY=108.75 EndZ=0
    g194: GeomPoint X=9.5 Y=110 Z=0
    g195: GeomPoint X=30 Y=94.5 Z=0
    g196: ArcOfCircle CenterX=34.8369 CenterY=95.75 CenterZ=0 NormalX=0 NormalY=0 NormalZ=1 AngleXU=0 Radius=1.25 StartAngle=3.14159 EndAngle=4.71239
    g197: LineSegment StartX=33.5869 StartY=95.75 StartZ=0 EndX=33.5869 EndY=108.75 EndZ=0
    g198: ArcOfCircle CenterX=34.8369 CenterY=108.75 CenterZ=0 NormalX=0 NormalY=0 NormalZ=1 AngleXU=0 Radius=1.25 StartAngle=1.5708 EndAngle=3.14159
    g199: LineSegment StartX=34.8369 StartY=110 StartZ=0 EndX=47.8369 EndY=110 EndZ=0
    g200: ArcOfCircle CenterX=47.8369 CenterY=108.75 CenterZ=0 NormalX=0 NormalY=0 NormalZ=1 AngleXU=0 Radius=1.25 StartAngle=-4.4e-15 EndAngle=1.5708
    g201: LineSegment StartX=49.0869 StartY=108.75 StartZ=0 EndX=49.0869 EndY=95.75 EndZ=0
    g202: ArcOfCircle CenterX=47.8369 CenterY=95.75 CenterZ=0 NormalX=0 NormalY=0 NormalZ=1 AngleXU=0 Radius=1.25 StartAngle=4.71239 EndAngle=6.28319
    g203: LineSegment StartX=47.8369 StartY=94.5 StartZ=0 EndX=34.8369 EndY=94.5 EndZ=0
    g204: GeomPoint X=33.5869 Y=94.5 Z=0
    g205: GeomPoint X=49.0869 Y=110 Z=0
    g206: ArcOfCircle CenterX=53.9238 CenterY=95.75 CenterZ=0 NormalX=0 NormalY=0 NormalZ=1 AngleXU=0 Radius=1.25 StartAngle=3.14159 EndAngle=4.71239
    g207: LineSegment StartX=52.6738 StartY=95.75 StartZ=0 EndX=52.6738 EndY=108.75 EndZ=0
    g208: ArcOfCircle CenterX=53.9238 CenterY=108.75 CenterZ=0 NormalX=0 NormalY=0 NormalZ=1 AngleXU=0 Radius=1.25 StartAngle=1.5708 EndAngle=3.14159
    g209: LineSegment StartX=53.9238 StartY=110 StartZ=0 EndX=66.9238 EndY=110 EndZ=0
    g210: ArcOfCircle CenterX=66.9238 CenterY=108.75 CenterZ=0 NormalX=0 NormalY=0 NormalZ=1 AngleXU=0 Radius=1.25 StartAngle=-5.3e-15 EndAngle=1.5708
    g211: LineSegment StartX=68.1738 StartY=108.75 StartZ=0 EndX=68.1738 EndY=95.75 EndZ=0
    g212: ArcOfCircle CenterX=66.9238 CenterY=95.75 CenterZ=0 NormalX=0 NormalY=0 NormalZ=1 AngleXU=0 Radius=1.25 StartAngle=4.71239 EndAngle=6.28319
    g213: LineSegment StartX=66.9238 StartY=94.5 StartZ=0 EndX=53.9238 EndY=94.5 EndZ=0
    g214: GeomPoint X=52.6738 Y=94.5 Z=0
    g215: GeomPoint X=68.1738 Y=110 Z=0
    g216: ArcOfCircle CenterX=73.0108 CenterY=95.75 CenterZ=0 NormalX=0 NormalY=0 NormalZ=1 AngleXU=0 Radius=1.25 StartAngle=3.14159 EndAngle=4.71239
    g217: LineSegment StartX=71.7608 StartY=95.75 StartZ=0 EndX=71.7608 EndY=108.75 EndZ=0
    g218: ArcOfCircle CenterX=73.0108 CenterY=108.75 CenterZ=0 NormalX=0 NormalY=0 NormalZ=1 AngleXU=0 Radius=1.25 StartAngle=1.5708 EndAngle=3.14159
    g219: LineSegment StartX=73.0108 StartY=110 StartZ=0 EndX=86.0108 EndY=110 EndZ=0
    g220: ArcOfCircle CenterX=86.0108 CenterY=108.75 CenterZ=0 NormalX=0 NormalY=0 NormalZ=1 AngleXU=0 Radius=1.25 StartAngle=-4.4e-15 EndAngle=1.5708
    g221: LineSegment StartX=87.2608 StartY=108.75 StartZ=0 EndX=87.2608 EndY=95.75 EndZ=0
    g222: ArcOfCircle CenterX=86.0108 CenterY=95.75 CenterZ=0 NormalX=0 NormalY=0 NormalZ=1 AngleXU=0 Radius=1.25 StartAngle=4.71239 EndAngle=6.28319
    g223: LineSegment StartX=86.0108 StartY=94.5 StartZ=0 EndX=73.0108 EndY=94.5 EndZ=0
    g224: GeomPoint X=71.7608 Y=94.5 Z=0
    g225: GeomPoint X=87.2608 Y=110 Z=0
    g226: ArcOfCircle CenterX=92.0977 CenterY=95.75 CenterZ=0 NormalX=0 NormalY=0 NormalZ=1 AngleXU=0 Radius=1.25 StartAngle=3.14159 EndAngle=4.71239
    g227: LineSegment StartX=90.8477 StartY=95.75 StartZ=0 EndX=90.8477 EndY=108.75 EndZ=0
    g228: ArcOfCircle CenterX=92.0977 CenterY=108.75 CenterZ=0 NormalX=0 NormalY=0 NormalZ=1 AngleXU=0 Radius=1.25 StartAngle=1.5708 EndAngle=3.14159
    g229: LineSegment StartX=92.0977 StartY=110 StartZ=0 EndX=181.445 EndY=110 EndZ=0
    g230: ArcOfCircle CenterX=181.445 CenterY=108.75 CenterZ=0 NormalX=0 NormalY=0 NormalZ=1 AngleXU=0 Radius=1.25 StartAngle=3e-16 EndAngle=1.5708
    g231: LineSegment StartX=182.695 StartY=108.75 StartZ=0 EndX=182.695 EndY=95.75 EndZ=0
    g232: ArcOfCircle CenterX=181.445 CenterY=95.75 CenterZ=0 NormalX=0 NormalY=0 NormalZ=1 AngleXU=0 Radius=1.25 StartAngle=4.71239 EndAngle=6.28319
    g233: LineSegment StartX=181.445 StartY=94.5 StartZ=0 EndX=92.0977 EndY=94.5 EndZ=0
    g234: GeomPoint X=90.8477 Y=94.5 Z=0
    g235: GeomPoint X=182.695 Y=110 Z=0
    g236: ArcOfCircle CenterX=187.532 CenterY=95.75 CenterZ=0 NormalX=0 NormalY=0 NormalZ=1 AngleXU=0 Radius=1.25 StartAngle=3.14159 EndAngle=4.71239
    g237: LineSegment StartX=186.282 StartY=95.75 StartZ=0 EndX=186.282 EndY=108.75 EndZ=0
    g238: ArcOfCircle CenterX=187.532 CenterY=108.75 CenterZ=0 NormalX=0 NormalY=0 NormalZ=1 AngleXU=0 Radius=1.25 StartAngle=1.5708 EndAngle=3.14159
    g239: LineSegment StartX=187.532 StartY=110 StartZ=0 EndX=200.532 EndY=110 EndZ=0
    g240: ArcOfCircle CenterX=200.532 CenterY=108.75 CenterZ=0 NormalX=0 NormalY=0 NormalZ=1 AngleXU=0 Radius=1.25 StartAngle=-9e-16 EndAngle=1.5708
    g241: LineSegment StartX=201.782 StartY=108.75 StartZ=0 EndX=201.782 EndY=95.75 EndZ=0
    g242: ArcOfCircle CenterX=200.532 CenterY=95.75 CenterZ=0 NormalX=0 NormalY=0 NormalZ=1 AngleXU=0 Radius=1.25 StartAngle=4.71239 EndAngle=6.28319
    g243: LineSegment StartX=200.532 StartY=94.5 StartZ=0 EndX=187.532 EndY=94.5 EndZ=0
    g244: GeomPoint X=186.282 Y=94.5 Z=0
    g245: GeomPoint X=201.782 Y=110 Z=0
    g246: ArcOfCircle CenterX=206.619 CenterY=95.75 CenterZ=0 NormalX=0 NormalY=0 NormalZ=1 AngleXU=0 Radius=1.25 StartAngle=3.14159 EndAngle=4.71239
    g247: LineSegment StartX=205.369 StartY=95.75 StartZ=0 EndX=205.369 EndY=108.75 EndZ=0
    g248: ArcOfCircle CenterX=206.619 CenterY=108.75 CenterZ=0 NormalX=0 NormalY=0 NormalZ=1 AngleXU=0 Radius=1.25 StartAngle=1.5708 EndAngle=3.14159
    g249: LineSegment StartX=206.619 StartY=110 StartZ=0 EndX=219.619 EndY=110 EndZ=0
    g250: ArcOfCircle CenterX=219.619 CenterY=108.75 CenterZ=0 NormalX=0 NormalY=0 NormalZ=1 AngleXU=0 Radius=1.25 StartAngle=-5.187e-13 EndAngle=1.5708
    g251: LineSegment StartX=220.869 StartY=108.75 StartZ=0 EndX=220.869 EndY=95.75 EndZ=0
    g252: ArcOfCircle CenterX=219.619 CenterY=95.75 CenterZ=0 NormalX=0 NormalY=0 NormalZ=1 AngleXU=0 Radius=1.25 StartAngle=4.71239 EndAngle=6.28319
    g253: LineSegment StartX=219.619 StartY=94.5 StartZ=0 EndX=206.619 EndY=94.5 EndZ=0
    g254: GeomPoint X=205.369 Y=94.5 Z=0
    g255: GeomPoint X=220.869 Y=110 Z=0
    g256: ArcOfCircle CenterX=225.706 CenterY=108.75 CenterZ=0 NormalX=0 NormalY=0 NormalZ=1 AngleXU=0 Radius=1.25 StartAngle=1.5708 EndAngle=3.14159
    g257: LineSegment StartX=225.706 StartY=110 StartZ=0 EndX=241.706 EndY=110 EndZ=0
    g258: ArcOfCircle CenterX=241.706 CenterY=108.75 CenterZ=0 NormalX=0 NormalY=0 NormalZ=1 AngleXU=0 Radius=1.25 StartAngle=0 EndAngle=1.5708
    g259: LineSegment StartX=242.956 StartY=108.75 StartZ=0 EndX=242.956 EndY=95.75 EndZ=0
    g260: ArcOfCircle CenterX=241.706 CenterY=95.75 CenterZ=0 NormalX=0 NormalY=0 NormalZ=1 AngleXU=0 Radius=1.25 StartAngle=4.71239 EndAngle=6.28319
    g261: LineSegment StartX=241.706 StartY=94.5 StartZ=0 EndX=225.706 EndY=94.5 EndZ=0
    g262: ArcOfCircle CenterX=225.706 CenterY=95.75 CenterZ=0 NormalX=0 NormalY=0 NormalZ=1 AngleXU=0 Radius=1.25 StartAngle=3.14159 EndAngle=4.71239
    g263: LineSegment StartX=224.456 StartY=95.75 StartZ=0 EndX=224.456 EndY=108.75 EndZ=0
    g264: GeomPoint X=224.456 Y=110 Z=0
    g265: GeomPoint X=242.956 Y=94.5 Z=0
    g266: ArcOfCircle CenterX=247.793 CenterY=108.75 CenterZ=0 NormalX=0 NormalY=0 NormalZ=1 AngleXU=0 Radius=1.25 StartAngle=1.5708 EndAngle=3.14159
    g267: LineSegment StartX=247.793 StartY=110 StartZ=0 EndX=263.793 EndY=110 EndZ=0
    g268: ArcOfCircle CenterX=263.793 CenterY=108.75 CenterZ=0 NormalX=0 NormalY=0 NormalZ=1 AngleXU=0 Radius=1.25 StartAngle=-1.8e-15 EndAngle=1.5708
    g269: LineSegment StartX=265.043 StartY=108.75 StartZ=0 EndX=265.043 EndY=95.75 EndZ=0
    g270: ArcOfCircle CenterX=263.793 CenterY=95.75 CenterZ=0 NormalX=0 NormalY=0 NormalZ=1 AngleXU=0 Radius=1.25 StartAngle=4.71239 EndAngle=6.28319
    g271: LineSegment StartX=263.793 StartY=94.5 StartZ=0 EndX=247.793 EndY=94.5 EndZ=0
    g272: ArcOfCircle CenterX=247.793 CenterY=95.75 CenterZ=0 NormalX=0 NormalY=0 NormalZ=1 AngleXU=0 Radius=1.25 StartAngle=3.14159 EndAngle=4.71239
    g273: LineSegment StartX=246.543 StartY=95.75 StartZ=0 EndX=246.543 EndY=108.75 EndZ=0
    g274: GeomPoint X=246.543 Y=110 Z=0
    g275: GeomPoint X=265.043 Y=94.5 Z=0
    g276: LineSegment StartX=30 StartY=108.75 StartZ=0 EndX=33.5869 EndY=108.75 EndZ=0
    g277: LineSegment StartX=49.0869 StartY=108.75 StartZ=0 EndX=52.6738 EndY=108.75 EndZ=0
    g278: LineSegment StartX=71.7608 StartY=108.75 StartZ=0 EndX=68.1738 EndY=108.75 EndZ=0
    g279: LineSegment StartX=87.2608 StartY=108.75 StartZ=0 EndX=90.8477 EndY=108.75 EndZ=0
    g280: LineSegment StartX=268.63 StartY=108.75 StartZ=0 EndX=265.043 EndY=108.75 EndZ=0
    g281: LineSegment StartX=246.543 StartY=108.75 StartZ=0 EndX=242.956 EndY=108.75 EndZ=0
    g282: LineSegment StartX=224.456 StartY=108.75 StartZ=0 EndX=220.869 EndY=108.75 EndZ=0
    g283: LineSegment StartX=205.369 StartY=108.75 StartZ=0 EndX=201.782 EndY=108.75 EndZ=0
    g284: LineSegment StartX=186.282 StartY=108.75 StartZ=0 EndX=182.695 EndY=108.75 EndZ=0
    g285: LineSegment StartX=32.75 StartY=167.476 StartZ=0 EndX=267.88 EndY=167.476 EndZ=0
    g286: LineSegment StartX=267.88 StartY=151.976 StartZ=0 EndX=32.75 EndY=151.976 EndZ=0
    g287: LineSegment StartX=37.75 StartY=148.317 StartZ=0 EndX=253.505 EndY=148.317 EndZ=0
    g288: LineSegment StartX=253.505 StartY=132.817 StartZ=0 EndX=37.75 EndY=132.817 EndZ=0
    g289: LineSegment StartX=47.75 StartY=129.159 StartZ=0 EndX=244.592 EndY=129.159 EndZ=0
    g290: LineSegment StartX=244.592 StartY=113.659 StartZ=0 EndX=47.75 EndY=113.659 EndZ=0
  constraints (685):
    c: Tangent(g0,g1) = 1.5708
    c: Tangent(g1,g2) = 1.5708
    c: Tangent(g2,g3) = 1.5708
    c: Tangent(g3,g4) = 1.5708
    c: Tangent(g4,g5) = 1.5708
    c: Tangent(g5,g6) = 1.5708
    c: Tangent(g6,g7) = 1.5708
    c: Tangent(g7,g0) = 1.5708
    c: Horizontal(g1)
    c: Horizontal(g5)
    c: Vertical(g3)
    c: Vertical(g7)
    c: Equal(g0,g2)
    c: Equal(g2,g4)
    c: Equal(g4,g6)
    c: PointOnObject(g8,g1)
    c: PointOnObject(g8,g7)
    c: PointOnObject(g9,g3)
    c: PointOnObject(g9,g5)
    c: Equal(g4,g-7)
    c: Coincident(g3,g-8)
    c: Coincident(g-3,g0)
    c: Coincident(g10,g-31)
    c: Coincident(g11,g-33)
    c: PointOnObject(g11,g7)
    c: Horizontal(g11)
    c: PointOnObject(g174,g7)
    c: Coincident(g12,g-37)
    c: PointOnObject(g12,g7)
    c: Horizontal(g12)
    c: Tangent(g13,g14) = 1.5708
    c: Tangent(g14,g15) = 1.5708
    c: Tangent(g15,g16) = 1.5708
    c: Tangent(g16,g17) = 1.5708
    c: Tangent(g17,g18) = 1.5708
    c: Tangent(g18,g19) = 1.5708
    c: Tangent(g19,g20) = 1.5708
    c: Tangent(g20,g13) = 1.5708
    c: Horizontal(g16)
    c: Horizontal(g20)
    c: Vertical(g14)
    c: Vertical(g18)
    c: Equal(g13,g15)
    c: Equal(g15,g17)
    c: Equal(g17,g19)
    c: PointOnObject(g21,g14)
    c: PointOnObject(g21,g20)
    c: PointOnObject(g22,g16)
    c: PointOnObject(g22,g18)
    c: PointOnObject(g21,g10)
    c: PointOnObject(g22,g11)
    c: Tangent(g23,g24) = 1.5708
    c: Tangent(g24,g25) = 1.5708
    c: Tangent(g25,g26) = 1.5708
    c: Tangent(g26,g27) = 1.5708
    c: Tangent(g27,g28) = 1.5708
    c: Tangent(g28,g29) = 1.5708
    c: Tangent(g29,g30) = 1.5708
    c: Tangent(g30,g23) = 1.5708
    c: Horizontal(g26)
    c: Horizontal(g30)
    c: Vertical(g24)
    c: Vertical(g28)
    c: Equal(g23,g25)
    c: Equal(g25,g27)
    c: Equal(g27,g29)
    c: PointOnObject(g31,g24)
    c: PointOnObject(g31,g30)
    c: PointOnObject(g32,g26)
    c: PointOnObject(g32,g28)
    c: PointOnObject(g31,g10)
    c: PointOnObject(g32,g11)
    c: Tangent(g33,g34) = 1.5708
    c: Tangent(g34,g35) = 1.5708
    c: Tangent(g35,g36) = 1.5708
    c: Tangent(g36,g37) = 1.5708
    c: Tangent(g37,g38) = 1.5708
    c: Tangent(g38,g39) = 1.5708
    c: Tangent(g39,g40) = 1.5708
    c: Tangent(g40,g33) = 1.5708
    c: Horizontal(g36)
    c: Horizontal(g40)
    c: Vertical(g34)
    c: Vertical(g38)
    c: Equal(g33,g35)
    c: Equal(g35,g37)
    c: Equal(g37,g39)
    c: PointOnObject(g41,g34)
    c: PointOnObject(g41,g40)
    c: PointOnObject(g42,g36)
    c: PointOnObject(g42,g38)
    c: PointOnObject(g41,g10)
    c: PointOnObject(g42,g11)
    c: Tangent(g43,g44) = 1.5708
    c: Tangent(g44,g45) = 1.5708
    c: Tangent(g45,g46) = 1.5708
    c: Tangent(g46,g47) = 1.5708
    c: Tangent(g47,g48) = 1.5708
    c: Tangent(g48,g49) = 1.5708
    c: Tangent(g49,g50) = 1.5708
    c: Tangent(g50,g43) = 1.5708
    c: Horizontal(g46)
    c: Horizontal(g50)
    c: Vertical(g44)
    c: Vertical(g48)
    c: Equal(g43,g45)
    c: Equal(g45,g47)
    c: Equal(g47,g49)
    c: PointOnObject(g51,g44)
    c: PointOnObject(g51,g50)
    c: PointOnObject(g52,g46)
    c: PointOnObject(g52,g48)
    c: PointOnObject(g51,g10)
    c: PointOnObject(g52,g11)
    c: Tangent(g53,g54) = 1.5708
    c: Tangent(g54,g55) = 1.5708
    c: Tangent(g55,g56) = 1.5708
    c: Tangent(g56,g57) = 1.5708
    c: Tangent(g57,g58) = 1.5708
    c: Tangent(g58,g59) = 1.5708
    c: Tangent(g59,g60) = 1.5708
    c: Tangent(g60,g53) = 1.5708
    c: Horizontal(g56)
    c: Horizontal(g60)
    c: Vertical(g54)
    c: Vertical(g58)
    c: Equal(g53,g55)
    c: Equal(g55,g57)
    c: Equal(g57,g59)
    c: PointOnObject(g61,g54)
    c: PointOnObject(g61,g60)
    c: PointOnObject(g62,g56)
    c: PointOnObject(g62,g58)
    c: PointOnObject(g61,g10)
    c: PointOnObject(g62,g11)
    c: Tangent(g63,g64) = 1.5708
    c: Tangent(g64,g65) = 1.5708
    c: Tangent(g65,g66) = 1.5708
    c: Tangent(g66,g67) = 1.5708
    c: Tangent(g67,g68) = 1.5708
    c: Tangent(g68,g69) = 1.5708
    c: Tangent(g69,g70) = 1.5708
    c: Tangent(g70,g63) = 1.5708
    c: Horizontal(g66)
    c: Horizontal(g70)
    c: Vertical(g64)
    c: Vertical(g68)
    c: Equal(g63,g65)
    c: Equal(g65,g67)
    c: Equal(g67,g69)
    c: PointOnObject(g71,g64)
    c: PointOnObject(g71,g70)
    c: PointOnObject(g72,g66)
    c: PointOnObject(g72,g68)
    c: PointOnObject(g71,g10)
    c: PointOnObject(g72,g11)
    c: Tangent(g73,g74) = 1.5708
    c: Tangent(g74,g75) = 1.5708
    c: Tangent(g75,g76) = 1.5708
    c: Tangent(g76,g77) = 1.5708
    c: Tangent(g77,g78) = 1.5708
    c: Tangent(g78,g79) = 1.5708
    c: Tangent(g79,g80) = 1.5708
    c: Tangent(g80,g73) = 1.5708
    c: Horizontal(g76)
    c: Horizontal(g80)
    c: Vertical(g74)
    c: Vertical(g78)
    c: Equal(g73,g75)
    c: Equal(g75,g77)
    c: Equal(g77,g79)
    c: PointOnObject(g81,g74)
    c: PointOnObject(g81,g80)
    c: PointOnObject(g82,g76)
    c: PointOnObject(g82,g78)
    c: PointOnObject(g81,g10)
    c: PointOnObject(g82,g11)
    c: Tangent(g83,g84) = 1.5708
    c: Tangent(g84,g85) = 1.5708
    c: Tangent(g85,g86) = 1.5708
    c: Tangent(g86,g87) = 1.5708
    c: Tangent(g87,g88) = 1.5708
    c: Tangent(g88,g89) = 1.5708
    c: Tangent(g89,g90) = 1.5708
    c: Tangent(g90,g83) = 1.5708
    c: Horizontal(g86)
    c: Horizontal(g90)
    c: Vertical(g84)
    c: Vertical(g88)
    c: Equal(g83,g85)
    c: Equal(g85,g87)
    c: Equal(g87,g89)
    c: PointOnObject(g91,g84)
    c: PointOnObject(g91,g90)
    c: PointOnObject(g92,g86)
    c: PointOnObject(g92,g88)
    c: PointOnObject(g91,g10)
    c: PointOnObject(g92,g11)
    c: Tangent(g93,g94) = 1.5708
    c: Tangent(g94,g95) = 1.5708
    c: Tangent(g95,g96) = 1.5708
    c: Tangent(g96,g97) = 1.5708
    c: Tangent(g97,g98) = 1.5708
    c: Tangent(g98,g99) = 1.5708
    c: Tangent(g99,g100) = 1.5708
    c: Tangent(g100,g93) = 1.5708
    c: Horizontal(g96)
    c: Horizontal(g100)
    c: Vertical(g94)
    c: Vertical(g98)
    c: Equal(g93,g95)
    c: Equal(g95,g97)
    c: Equal(g97,g99)
    c: PointOnObject(g101,g94)
    c: PointOnObject(g101,g100)
    c: PointOnObject(g102,g96)
    c: PointOnObject(g102,g98)
    c: PointOnObject(g101,g10)
    c: PointOnObject(g102,g11)
    c: Tangent(g103,g104) = 1.5708
    c: Tangent(g104,g105) = 1.5708
    c: Tangent(g105,g106) = 1.5708
    c: Tangent(g106,g107) = 1.5708
    c: Tangent(g107,g108) = 1.5708
    c: Tangent(g108,g109) = 1.5708
    c: Tangent(g109,g110) = 1.5708
    c: Tangent(g110,g103) = 1.5708
    c: Horizontal(g106)
    c: Horizontal(g110)
    c: Vertical(g104)
    c: Vertical(g108)
    c: Equal(g103,g105)
    c: Equal(g105,g107)
    c: Equal(g107,g109)
    c: PointOnObject(g111,g104)
    c: PointOnObject(g111,g110)
    c: PointOnObject(g112,g106)
    c: PointOnObject(g112,g108)
    c: PointOnObject(g111,g10)
    c: PointOnObject(g112,g11)
    c: Tangent(g113,g114) = 1.5708
    c: Tangent(g114,g115) = 1.5708
    c: Tangent(g115,g116) = 1.5708
    c: Tangent(g116,g117) = 1.5708
    c: Tangent(g117,g118) = 1.5708
    c: Tangent(g118,g119) = 1.5708
    c: Tangent(g119,g120) = 1.5708
    c: Tangent(g120,g113) = 1.5708
    c: Horizontal(g116)
    c: Horizontal(g120)
    c: Vertical(g114)
    c: Vertical(g118)
    c: Equal(g113,g115)
    c: Equal(g115,g117)
    c: Equal(g117,g119)
    c: PointOnObject(g121,g114)
    c: PointOnObject(g121,g120)
    c: PointOnObject(g122,g116)
    c: PointOnObject(g122,g118)
    c: PointOnObject(g121,g10)
    c: PointOnObject(g122,g11)
    c: Tangent(g123,g124) = 1.5708
    c: Tangent(g124,g125) = 1.5708
    c: Tangent(g125,g126) = 1.5708
    c: Tangent(g126,g127) = 1.5708
    c: Tangent(g127,g128) = 1.5708
    c: Tangent(g128,g129) = 1.5708
    c: Tangent(g129,g130) = 1.5708
    c: Tangent(g130,g123) = 1.5708
    c: Horizontal(g126)
    c: Horizontal(g130)
    c: Vertical(g124)
    c: Vertical(g128)
    c: Equal(g123,g125)
    c: Equal(g125,g127)
    c: Equal(g127,g129)
    c: PointOnObject(g131,g124)
    c: PointOnObject(g131,g130)
    c: PointOnObject(g132,g126)
    c: PointOnObject(g132,g128)
    c: PointOnObject(g131,g10)
    c: PointOnObject(g132,g11)
    c: Tangent(g133,g134) = 1.5708
    c: Tangent(g134,g135) = 1.5708
    c: Tangent(g135,g136) = 1.5708
    c: Tangent(g136,g137) = 1.5708
    c: Tangent(g137,g138) = 1.5708
    c: Tangent(g138,g139) = 1.5708
    c: Tangent(g139,g140) = 1.5708
    c: Tangent(g140,g133) = 1.5708
    c: Horizontal(g136)
    c: Horizontal(g140)
    c: Vertical(g134)
    c: Vertical(g138)
    c: Equal(g133,g135)
    c: Equal(g135,g137)
    c: Equal(g137,g139)
    c: PointOnObject(g141,g134)
    c: PointOnObject(g141,g140)
    c: PointOnObject(g142,g136)
    c: PointOnObject(g142,g138)
    c: PointOnObject(g141,g10)
    c: Coincident(g142,g11)
    c: Equal(g-31,g13)
    c: Equal(g19,g23)
    c: Equal(g29,g33)
    c: Equal(g43,g39)
    c: Equal(g59,g63)
    c: Equal(g69,g73)
    c: Equal(g79,g83)
    c: Equal(g89,g93)
    c: Equal(g99,g103)
    c: Equal(g109,g113)
    c: Equal(g119,g123)
    c: Equal(g129,g133)
    c: Equal(g49,g53)
    c: Coincident(g143,g-32)
    c: Coincident(g143,g13)
    c: Horizontal(g143)
    c: Coincident(g144,g18)
    c: Coincident(g144,g23)
    c: Coincident(g145,g28)
    c: Coincident(g145,g33)
    c: Coincident(g146,g38)
    c: Coincident(g146,g43)
    c: Coincident(g147,g48)
    c: Coincident(g147,g53)
    c: Coincident(g148,g58)
    c: Coincident(g148,g63)
    c: Coincident(g149,g68)
    c: Coincident(g149,g73)
    c: Coincident(g150,g78)
    c: Coincident(g150,g83)
    c: Coincident(g151,g88)
    c: Coincident(g151,g93)
    c: Coincident(g152,g98)
    c: Coincident(g152,g103)
    c: Coincident(g153,g108)
    c: Coincident(g153,g113)
    c: Coincident(g154,g118)
    c: Coincident(g154,g123)
    c: Coincident(g155,g128)
    c: Coincident(g155,g133)
    c: PointOnObject(g10,g7)
    c: PointOnObject(g164,g7)
    c: PointOnObject(g184,g7)
    c: Tangent(g156,g157) = 1.5708
    c: Tangent(g157,g158) = 1.5708
    c: Tangent(g158,g159) = 1.5708
    c: Tangent(g159,g160) = 1.5708
    c: Tangent(g160,g161) = 1.5708
    c: Tangent(g161,g162) = 1.5708
    c: Tangent(g162,g163) = 1.5708
    c: Tangent(g163,g156) = 1.5708
    c: Horizontal(g159)
    c: Horizontal(g163)
    c: Vertical(g157)
    c: Vertical(g161)
    c: Equal(g156,g158)
    c: Equal(g158,g160)
    c: Equal(g160,g162)
    c: PointOnObject(g164,g157)
    c: PointOnObject(g164,g163)
    c: PointOnObject(g165,g159)
    c: PointOnObject(g165,g161)
    c: Tangent(g166,g167) = 1.5708
    c: Tangent(g167,g168) = 1.5708
    c: Tangent(g168,g169) = 1.5708
    c: Tangent(g169,g170) = 1.5708
    c: Tangent(g170,g171) = 1.5708
    c: Tangent(g171,g172) = 1.5708
    c: Tangent(g172,g173) = 1.5708
    c: Tangent(g173,g166) = 1.5708
    c: Horizontal(g169)
    c: Horizontal(g173)
    c: Vertical(g167)
    c: Vertical(g171)
    c: Equal(g166,g168)
    c: Equal(g168,g170)
    c: Equal(g170,g172)
    c: PointOnObject(g174,g167)
    c: PointOnObject(g174,g173)
    c: PointOnObject(g175,g169)
    c: PointOnObject(g175,g171)
    c: DistanceX(g156,g161) = 24.5
    c: Tangent(g176,g177) = 1.5708
    c: Tangent(g177,g178) = 1.5708
    c: Tangent(g178,g179) = 1.5708
    c: Tangent(g179,g180) = 1.5708
    c: Tangent(g180,g181) = 1.5708
    c: Tangent(g181,g182) = 1.5708
    c: Tangent(g182,g183) = 1.5708
    c: Tangent(g183,g176) = 1.5708
    c: Horizontal(g179)
    c: Horizontal(g183)
    c: Vertical(g177)
    c: Vertical(g181)
    c: Equal(g176,g178)
    c: Equal(g178,g180)
    c: Equal(g180,g182)
    c: PointOnObject(g184,g177)
    c: PointOnObject(g184,g183)
    c: PointOnObject(g185,g179)
    c: PointOnObject(g185,g181)
    c: Tangent(g186,g187) = 1.5708
    c: Tangent(g187,g188) = 1.5708
    c: Tangent(g188,g189) = 1.5708
    c: Tangent(g189,g190) = 1.5708
    c: Tangent(g190,g191) = 1.5708
    c: Tangent(g191,g192) = 1.5708
    c: Tangent(g192,g193) = 1.5708
    c: Tangent(g193,g186) = 1.5708
    c: Horizontal(g187)
    c: Horizontal(g191)
    c: Vertical(g189)
    c: Vertical(g193)
    c: Equal(g186,g188)
    c: Equal(g188,g190)
    c: Equal(g190,g192)
    c: PointOnObject(g194,g187)
    c: PointOnObject(g194,g193)
    c: PointOnObject(g195,g189)
    c: PointOnObject(g195,g191)
    c: Coincident(g194,g12)
    c: PointOnObject(g195,g5)
    c: Equal(g135,g160)
    c: Equal(g162,g170)
    c: Equal(g172,g180)
    c: Equal(g182,g188)
    c: Equal(g143,g144)
    c: Equal(g144,g145)
    c: Equal(g145,g146)
    c: Equal(g146,g147)
    c: Equal(g147,g148)
    c: Equal(g148,g149)
    c: Equal(g149,g150)
    c: Equal(g150,g151)
    c: Equal(g151,g152)
    c: Equal(g152,g153)
    c: Equal(g153,g154)
    c: Equal(g154,g155)
    c: Equal(g20,g30)
    c: Equal(g30,g40)
    c: Equal(g40,g50)
    c: Equal(g50,g60)
    c: Equal(g60,g70)
    c: Equal(g70,g80)
    c: Equal(g80,g90)
    c: Equal(g90,g100)
    c: Equal(g100,g110)
    c: Equal(g110,g120)
    c: Equal(g120,g130)
    c: Equal(g130,g140)
    c: Equal(g20,g18)
    c: Equal(g169,g-20)
    c: Equal(g-22,g187)
    c: DistanceX(g176,g181) = 39.5
    c: Tangent(g196,g197) = 1.5708
    c: Tangent(g197,g198) = 1.5708
    c: Tangent(g198,g199) = 1.5708
    c: Tangent(g199,g200) = 1.5708
    c: Tangent(g200,g201) = 1.5708
    c: Tangent(g201,g202) = 1.5708
    c: Tangent(g202,g203) = 1.5708
    c: Tangent(g203,g196) = 1.5708
    c: Horizontal(g199)
    c: Horizontal(g203)
    c: Vertical(g197)
    c: Vertical(g201)
    c: Equal(g196,g198)
    c: Equal(g198,g200)
    c: Equal(g200,g202)
    c: PointOnObject(g204,g197)
    c: PointOnObject(g204,g203)
    c: PointOnObject(g205,g199)
    c: PointOnObject(g205,g201)
    c: PointOnObject(g204,g5)
    c: PointOnObject(g205,g12)
    c: Tangent(g206,g207) = 1.5708
    c: Tangent(g207,g208) = 1.5708
    c: Tangent(g208,g209) = 1.5708
    c: Tangent(g209,g210) = 1.5708
    c: Tangent(g210,g211) = 1.5708
    c: Tangent(g211,g212) = 1.5708
    c: Tangent(g212,g213) = 1.5708
    c: Tangent(g213,g206) = 1.5708
    c: Horizontal(g209)
    c: Horizontal(g213)
    c: Vertical(g207)
    c: Vertical(g211)
    c: Equal(g206,g208)
    c: Equal(g208,g210)
    c: Equal(g210,g212)
    c: PointOnObject(g214,g207)
    c: PointOnObject(g214,g213)
    c: PointOnObject(g215,g209)
    c: PointOnObject(g215,g211)
    c: PointOnObject(g214,g5)
    c: PointOnObject(g215,g12)
    c: Tangent(g216,g217) = 1.5708
    c: Tangent(g217,g218) = 1.5708
    c: Tangent(g218,g219) = 1.5708
    c: Tangent(g219,g220) = 1.5708
    c: Tangent(g220,g221) = 1.5708
    c: Tangent(g221,g222) = 1.5708
    c: Tangent(g222,g223) = 1.5708
    c: Tangent(g223,g216) = 1.5708
    c: Horizontal(g219)
    c: Horizontal(g223)
    c: Vertical(g217)
    c: Vertical(g221)
    c: Equal(g216,g218)
    c: Equal(g218,g220)
    c: Equal(g220,g222)
    c: PointOnObject(g224,g217)
    c: PointOnObject(g224,g223)
    c: PointOnObject(g225,g219)
    c: PointOnObject(g225,g221)
    c: PointOnObject(g224,g5)
    c: PointOnObject(g225,g12)
    c: Tangent(g226,g227) = 1.5708
    c: Tangent(g227,g228) = 1.5708
    c: Tangent(g228,g229) = 1.5708
    c: Tangent(g229,g230) = 1.5708
    c: Tangent(g230,g231) = 1.5708
    c: Tangent(g231,g232) = 1.5708
    c: Tangent(g232,g233) = 1.5708
    c: Tangent(g233,g226) = 1.5708
    c: Horizontal(g229)
    c: Horizontal(g233)
    c: Vertical(g227)
    c: Vertical(g231)
    c: Equal(g226,g228)
    c: Equal(g228,g230)
    c: Equal(g230,g232)
    c: PointOnObject(g234,g227)
    c: PointOnObject(g234,g233)
    c: PointOnObject(g235,g229)
    c: PointOnObject(g235,g231)
    c: PointOnObject(g234,g5)
    c: PointOnObject(g235,g12)
    c: Tangent(g236,g237) = 1.5708
    c: Tangent(g237,g238) = 1.5708
    c: Tangent(g238,g239) = 1.5708
    c: Tangent(g239,g240) = 1.5708
    c: Tangent(g240,g241) = 1.5708
    c: Tangent(g241,g242) = 1.5708
    c: Tangent(g242,g243) = 1.5708
    c: Tangent(g243,g236) = 1.5708
    c: Horizontal(g239)
    c: Horizontal(g243)
    c: Vertical(g237)
    c: Vertical(g241)
    c: Equal(g236,g238)
    c: Equal(g238,g240)
    c: Equal(g240,g242)
    c: PointOnObject(g244,g237)
    c: PointOnObject(g244,g243)
    c: PointOnObject(g245,g239)
    c: PointOnObject(g245,g241)
    c: PointOnObject(g244,g5)
    c: PointOnObject(g245,g12)
    c: Tangent(g246,g247) = 1.5708
    c: Tangent(g247,g248) = 1.5708
    c: Tangent(g248,g249) = 1.5708
    c: Tangent(g249,g250) = 1.5708
    c: Tangent(g250,g251) = 1.5708
    c: Tangent(g251,g252) = 1.5708
    c: Tangent(g252,g253) = 1.5708
    c: Tangent(g253,g246) = 1.5708
    c: Horizontal(g249)
    c: Horizontal(g253)
    c: Vertical(g247)
    c: Vertical(g251)
    c: Equal(g246,g248)
    c: Equal(g248,g250)
    c: Equal(g250,g252)
    c: PointOnObject(g254,g247)
    c: PointOnObject(g254,g253)
    c: PointOnObject(g255,g249)
    c: PointOnObject(g255,g251)
    c: PointOnObject(g254,g5)
    c: PointOnObject(g255,g12)
    c: Tangent(g256,g257) = 1.5708
    c: Tangent(g257,g258) = 1.5708
    c: Tangent(g258,g259) = 1.5708
    c: Tangent(g259,g260) = 1.5708
    c: Tangent(g260,g261) = 1.5708
    c: Tangent(g261,g262) = 1.5708
    c: Tangent(g262,g263) = 1.5708
    c: Tangent(g263,g256) = 1.5708
    c: Horizontal(g257)
    c: Horizontal(g261)
    c: Vertical(g259)
    c: Vertical(g263)
    c: Equal(g256,g258)
    c: Equal(g258,g260)
    c: Equal(g260,g262)
    c: PointOnObject(g264,g257)
    c: PointOnObject(g264,g263)
    c: PointOnObject(g265,g259)
    c: PointOnObject(g265,g261)
    c: PointOnObject(g264,g12)
    c: PointOnObject(g265,g5)
    c: Tangent(g266,g267) = 1.5708
    c: Tangent(g267,g268) = 1.5708
    c: Tangent(g268,g269) = 1.5708
    c: Tangent(g269,g270) = 1.5708
    c: Tangent(g270,g271) = 1.5708
    c: Tangent(g271,g272) = 1.5708
    c: Tangent(g272,g273) = 1.5708
    c: Tangent(g273,g266) = 1.5708
    c: Horizontal(g267)
    c: Horizontal(g271)
    c: Vertical(g269)
    c: Vertical(g273)
    c: Equal(g266,g268)
    c: Equal(g268,g270)
    c: Equal(g270,g272)
    c: PointOnObject(g274,g267)
    c: PointOnObject(g274,g273)
    c: PointOnObject(g275,g269)
    c: PointOnObject(g275,g271)
    c: PointOnObject(g274,g12)
    c: PointOnObject(g275,g5)
    c: Equal(g-36,g268)
    c: Equal(g266,g258)
    c: Equal(g256,g250)
    c: Equal(g248,g240)
    c: Equal(g238,g230)
    c: Equal(g228,g220)
    c: Equal(g218,g210)
    c: Equal(g208,g200)
    c: Coincident(g276,g188)
    c: Coincident(g276,g197)
    c: Equal(g199,g209)
    c: Equal(g209,g219)
    c: Coincident(g277,g200)
    c: Coincident(g277,g207)
    c: Coincident(g278,g217)
    c: Coincident(g278,g210)
    c: Coincident(g279,g220)
    c: Coincident(g279,g227)
    c: Coincident(g280,g-36)
    c: Coincident(g280,g268)
    c: Coincident(g281,g266)
    c: Coincident(g281,g258)
    c: Coincident(g282,g256)
    c: Coincident(g282,g250)
    c: Coincident(g283,g247)
    c: Coincident(g283,g240)
    c: Coincident(g284,g237)
    c: Coincident(g284,g230)
    c: Equal(g239,g249)
    c: Equal(g257,g267)
    c: Equal(g280,g281)
    c: Equal(g281,g282)
    c: Equal(g282,g283)
    c: Equal(g283,g284)
    c: Equal(g279,g278)
    c: Equal(g277,g278)
    c: Equal(g277,g276)
    c: Equal(g219,g239)
    c: Equal(g280,g143)
    c: Equal(g267,g-37)
    c: Equal(g284,g279)
    c: Coincident(g285,g159)
    c: Coincident(g285,g-29)
    c: Horizontal(g285)
    c: Coincident(g286,g-28)
    c: Coincident(g286,g162)
    c: Horizontal(g286)
    c: Coincident(g287,g169)
    c: Coincident(g287,g-27)
    c: Horizontal(g287)
    c: Coincident(g288,g-25)
    c: Coincident(g288,g172)
    c: Horizontal(g288)
    c: Coincident(g289,g179)
    c: Coincident(g289,g-13)
    c: Horizontal(g289)
    c: Coincident(g290,g-10)
    c: Coincident(g290,g182)
    c: Horizontal(g290)
    c: Equal(g249,g251)
FEATURE [Sketcher::SketchObject] Sketch010
  ExternalGeometry = -> [Sketch009,Sketch]
  FullyConstrained = true
  MapMode = 2
  Placement = pos=(0,0,12.53) rot=(0,0,1;0rad)
  Support = -> [Sketch]
  sketch-geometry (113):
    g0: LineSegment StartX=47.75 StartY=129.159 StartZ=0 EndX=244.592 EndY=129.159 EndZ=0
    g1: LineSegment StartX=244.592 StartY=113.659 StartZ=0 EndX=47.75 EndY=113.659 EndZ=0
    g2: ArcOfCircle CenterX=53.8266 CenterY=127.908 CenterZ=0 NormalX=0 NormalY=0 NormalZ=1 AngleXU=0 Radius=1.25 StartAngle=1.5708 EndAngle=3.14159
    g3: LineSegment StartX=53.8266 StartY=129.158 StartZ=0 EndX=66.8266 EndY=129.158 EndZ=0
    g4: ArcOfCircle CenterX=66.8266 CenterY=127.908 CenterZ=0 NormalX=0 NormalY=0 NormalZ=1 AngleXU=0 Radius=1.25 StartAngle=-2.7e-15 EndAngle=1.5708
    g5: LineSegment StartX=68.0766 StartY=127.908 StartZ=0 EndX=68.0766 EndY=114.909 EndZ=0
    g6: ArcOfCircle CenterX=66.8266 CenterY=114.909 CenterZ=0 NormalX=0 NormalY=0 NormalZ=1 AngleXU=0 Radius=1.25 StartAngle=4.71239 EndAngle=6.28319
    g7: LineSegment StartX=66.8266 StartY=113.659 StartZ=0 EndX=53.8266 EndY=113.659 EndZ=0
    g8: ArcOfCircle CenterX=53.8266 CenterY=114.909 CenterZ=0 NormalX=0 NormalY=0 NormalZ=1 AngleXU=0 Radius=1.25 StartAngle=3.14159 EndAngle=4.71239
    g9: LineSegment StartX=52.5766 StartY=114.909 StartZ=0 EndX=52.5766 EndY=127.908 EndZ=0
    g10: GeomPoint X=52.5766 Y=129.158 Z=0
    g11: GeomPoint X=68.0766 Y=113.659 Z=0
    g12: ArcOfCircle CenterX=72.9032 CenterY=127.908 CenterZ=0 NormalX=0 NormalY=0 NormalZ=1 AngleXU=0 Radius=1.25 StartAngle=1.5708 EndAngle=3.14159
    g13: LineSegment StartX=72.9032 StartY=129.158 StartZ=0 EndX=85.9032 EndY=129.158 EndZ=0
    g14: ArcOfCircle CenterX=85.9032 CenterY=127.908 CenterZ=0 NormalX=0 NormalY=0 NormalZ=1 AngleXU=0 Radius=1.25 StartAngle=-5.3e-15 EndAngle=1.5708
    g15: LineSegment StartX=87.1532 StartY=127.908 StartZ=0 EndX=87.1532 EndY=114.909 EndZ=0
    g16: ArcOfCircle CenterX=85.9032 CenterY=114.909 CenterZ=0 NormalX=0 NormalY=0 NormalZ=1 AngleXU=0 Radius=1.25 StartAngle=4.71239 EndAngle=6.28319
    g17: LineSegment StartX=85.9032 StartY=113.659 StartZ=0 EndX=72.9032 EndY=113.659 EndZ=0
    g18: ArcOfCircle CenterX=72.9032 CenterY=114.909 CenterZ=0 NormalX=0 NormalY=0 NormalZ=1 AngleXU=0 Radius=1.25 StartAngle=3.14159 EndAngle=4.71239
    g19: LineSegment StartX=71.6532 StartY=114.909 StartZ=0 EndX=71.6532 EndY=127.908 EndZ=0
    g20: GeomPoint X=71.6532 Y=129.158 Z=0
    g21: GeomPoint X=87.1532 Y=113.659 Z=0
    g22: ArcOfCircle CenterX=91.9798 CenterY=127.908 CenterZ=0 NormalX=0 NormalY=0 NormalZ=1 AngleXU=0 Radius=1.25 StartAngle=1.5708 EndAngle=3.14159
    g23: LineSegment StartX=91.9798 StartY=129.158 StartZ=0 EndX=104.98 EndY=129.158 EndZ=0
    g24: ArcOfCircle CenterX=104.98 CenterY=127.908 CenterZ=0 NormalX=0 NormalY=0 NormalZ=1 AngleXU=0 Radius=1.25 StartAngle=1.2e-15 EndAngle=1.5708
    g25: LineSegment StartX=106.23 StartY=127.908 StartZ=0 EndX=106.23 EndY=114.909 EndZ=0
    g26: ArcOfCircle CenterX=104.98 CenterY=114.909 CenterZ=0 NormalX=0 NormalY=0 NormalZ=1 AngleXU=0 Radius=1.25 StartAngle=4.71239 EndAngle=6.28319
    g27: LineSegment StartX=104.98 StartY=113.659 StartZ=0 EndX=91.9798 EndY=113.659 EndZ=0
    g28: ArcOfCircle CenterX=91.9798 CenterY=114.909 CenterZ=0 NormalX=0 NormalY=0 NormalZ=1 AngleXU=0 Radius=1.25 StartAngle=3.14159 EndAngle=4.71239
    g29: LineSegment StartX=90.7298 StartY=114.909 StartZ=0 EndX=90.7298 EndY=127.908 EndZ=0
    g30: GeomPoint X=90.7298 Y=129.158 Z=0
    g31: GeomPoint X=106.23 Y=113.659 Z=0
    g32: ArcOfCircle CenterX=111.056 CenterY=127.908 CenterZ=0 NormalX=0 NormalY=0 NormalZ=1 AngleXU=0 Radius=1.25 StartAngle=1.5708 EndAngle=3.14159
    g33: LineSegment StartX=111.056 StartY=129.158 StartZ=0 EndX=124.056 EndY=129.158 EndZ=0
    g34: ArcOfCircle CenterX=124.056 CenterY=127.908 CenterZ=0 NormalX=0 NormalY=0 NormalZ=1 AngleXU=0 Radius=1.25 StartAngle=4e-16 EndAngle=1.5708
    g35: LineSegment StartX=125.306 StartY=127.908 StartZ=0 EndX=125.306 EndY=114.909 EndZ=0
    g36: ArcOfCircle CenterX=124.056 CenterY=114.909 CenterZ=0 NormalX=0 NormalY=0 NormalZ=1 AngleXU=0 Radius=1.25 StartAngle=4.71239 EndAngle=6.28319
    g37: LineSegment StartX=124.056 StartY=113.659 StartZ=0 EndX=111.056 EndY=113.659 EndZ=0
    g38: ArcOfCircle CenterX=111.056 CenterY=114.909 CenterZ=0 NormalX=0 NormalY=0 NormalZ=1 AngleXU=0 Radius=1.25 StartAngle=3.14159 EndAngle=4.71239
    g39: LineSegment StartX=109.806 StartY=114.909 StartZ=0 EndX=109.806 EndY=127.908 EndZ=0
    g40: GeomPoint X=109.806 Y=129.158 Z=0
    g41: GeomPoint X=125.306 Y=113.659 Z=0
    g42: ArcOfCircle CenterX=130.133 CenterY=127.908 CenterZ=0 NormalX=0 NormalY=0 NormalZ=1 AngleXU=0 Radius=1.25 StartAngle=1.5708 EndAngle=3.14159
    g43: LineSegment StartX=130.133 StartY=129.158 StartZ=0 EndX=143.133 EndY=129.158 EndZ=0
    g44: ArcOfCircle CenterX=143.133 CenterY=127.908 CenterZ=0 NormalX=0 NormalY=0 NormalZ=1 AngleXU=0 Radius=1.25 StartAngle=-4.4e-15 EndAngle=1.5708
    g45: LineSegment StartX=144.383 StartY=127.908 StartZ=0 EndX=144.383 EndY=114.909 EndZ=0
    g46: ArcOfCircle CenterX=143.133 CenterY=114.909 CenterZ=0 NormalX=0 NormalY=0 NormalZ=1 AngleXU=0 Radius=1.25 StartAngle=4.71239 EndAngle=6.28319
    g47: LineSegment StartX=143.133 StartY=113.659 StartZ=0 EndX=130.133 EndY=113.659 EndZ=0
    g48: ArcOfCircle CenterX=130.133 CenterY=114.909 CenterZ=0 NormalX=0 NormalY=0 NormalZ=1 AngleXU=0 Radius=1.25 StartAngle=3.14159 EndAngle=4.71239
    g49: LineSegment StartX=128.883 StartY=114.909 StartZ=0 EndX=128.883 EndY=127.908 EndZ=0
    g50: GeomPoint X=128.883 Y=129.158 Z=0
    g51: GeomPoint X=144.383 Y=113.659 Z=0
    g52: ArcOfCircle CenterX=149.21 CenterY=127.908 CenterZ=0 NormalX=0 NormalY=0 NormalZ=1 AngleXU=0 Radius=1.25 StartAngle=1.5708 EndAngle=3.14159
    g53: LineSegment StartX=149.21 StartY=129.158 StartZ=0 EndX=162.21 EndY=129.158 EndZ=0
    g54: ArcOfCircle CenterX=162.21 CenterY=127.908 CenterZ=0 NormalX=0 NormalY=0 NormalZ=1 AngleXU=0 Radius=1.25 StartAngle=-3.6e-15 EndAngle=1.5708
    g55: LineSegment StartX=163.46 StartY=127.908 StartZ=0 EndX=163.46 EndY=114.909 EndZ=0
    g56: ArcOfCircle CenterX=162.21 CenterY=114.909 CenterZ=0 NormalX=0 NormalY=0 NormalZ=1 AngleXU=0 Radius=1.25 StartAngle=4.71239 EndAngle=6.28319
    g57: LineSegment StartX=162.21 StartY=113.659 StartZ=0 EndX=149.21 EndY=113.659 EndZ=0
    g58: ArcOfCircle CenterX=149.21 CenterY=114.909 CenterZ=0 NormalX=0 NormalY=0 NormalZ=1 AngleXU=0 Radius=1.25 StartAngle=3.14159 EndAngle=4.71239
    g59: LineSegment StartX=147.96 StartY=114.909 StartZ=0 EndX=147.96 EndY=127.908 EndZ=0
    g60: GeomPoint X=147.96 Y=129.158 Z=0
    g61: GeomPoint X=163.46 Y=113.659 Z=0
    g62: ArcOfCircle CenterX=168.286 CenterY=127.908 CenterZ=0 NormalX=0 NormalY=0 NormalZ=1 AngleXU=0 Radius=1.25 StartAngle=1.5708 EndAngle=3.14159
    g63: LineSegment StartX=168.286 StartY=129.158 StartZ=0 EndX=181.286 EndY=129.158 EndZ=0
    g64: ArcOfCircle CenterX=181.286 CenterY=127.908 CenterZ=0 NormalX=0 NormalY=0 NormalZ=1 AngleXU=0 Radius=1.25 StartAngle=2.5e-15 EndAngle=1.5708
    g65: LineSegment StartX=182.536 StartY=127.908 StartZ=0 EndX=182.536 EndY=114.909 EndZ=0
    g66: ArcOfCircle CenterX=181.286 CenterY=114.909 CenterZ=0 NormalX=0 NormalY=0 NormalZ=1 AngleXU=0 Radius=1.25 StartAngle=4.71239 EndAngle=6.28319
    g67: LineSegment StartX=181.286 StartY=113.659 StartZ=0 EndX=168.286 EndY=113.659 EndZ=0
    g68: ArcOfCircle CenterX=168.286 CenterY=114.909 CenterZ=0 NormalX=0 NormalY=0 NormalZ=1 AngleXU=0 Radius=1.25 StartAngle=3.14159 EndAngle=4.71239
    g69: LineSegment StartX=167.036 StartY=114.909 StartZ=0 EndX=167.036 EndY=127.908 EndZ=0
    g70: GeomPoint X=167.036 Y=129.158 Z=0
    g71: GeomPoint X=182.536 Y=113.659 Z=0
    g72: ArcOfCircle CenterX=187.363 CenterY=127.908 CenterZ=0 NormalX=0 NormalY=0 NormalZ=1 AngleXU=0 Radius=1.25 StartAngle=1.5708 EndAngle=3.14159
    g73: LineSegment StartX=187.363 StartY=129.158 StartZ=0 EndX=200.363 EndY=129.158 EndZ=0
    g74: ArcOfCircle CenterX=200.363 CenterY=127.908 CenterZ=0 NormalX=0 NormalY=0 NormalZ=1 AngleXU=0 Radius=1.25 StartAngle=4.6e-15 EndAngle=1.5708
    g75: LineSegment StartX=201.613 StartY=127.908 StartZ=0 EndX=201.613 EndY=114.909 EndZ=0
    g76: ArcOfCircle CenterX=200.363 CenterY=114.909 CenterZ=0 NormalX=0 NormalY=0 NormalZ=1 AngleXU=0 Radius=1.25 StartAngle=4.71239 EndAngle=6.28319
    g77: LineSegment StartX=200.363 StartY=113.659 StartZ=0 EndX=187.363 EndY=113.659 EndZ=0
    g78: ArcOfCircle CenterX=187.363 CenterY=114.909 CenterZ=0 NormalX=0 NormalY=0 NormalZ=1 AngleXU=0 Radius=1.25 StartAngle=3.14159 EndAngle=4.71239
    g79: LineSegment StartX=186.113 StartY=114.909 StartZ=0 EndX=186.113 EndY=127.908 EndZ=0
    g80: GeomPoint X=186.113 Y=129.158 Z=0
    g81: GeomPoint X=201.613 Y=113.659 Z=0
    g82: ArcOfCircle CenterX=206.439 CenterY=127.908 CenterZ=0 NormalX=0 NormalY=0 NormalZ=1 AngleXU=0 Radius=1.25 StartAngle=1.5708 EndAngle=3.14159
    g83: LineSegment StartX=206.439 StartY=129.158 StartZ=0 EndX=219.439 EndY=129.158 EndZ=0
    g84: ArcOfCircle CenterX=219.439 CenterY=127.908 CenterZ=0 NormalX=0 NormalY=0 NormalZ=1 AngleXU=0 Radius=1.25 StartAngle=2.9e-15 EndAngle=1.5708
    g85: LineSegment StartX=220.689 StartY=127.908 StartZ=0 EndX=220.689 EndY=114.909 EndZ=0
    g86: ArcOfCircle CenterX=219.439 CenterY=114.909 CenterZ=0 NormalX=0 NormalY=0 NormalZ=1 AngleXU=0 Radius=1.25 StartAngle=4.71239 EndAngle=6.28319
    g87: LineSegment StartX=219.439 StartY=113.659 StartZ=0 EndX=206.439 EndY=113.659 EndZ=0
    g88: ArcOfCircle CenterX=206.439 CenterY=114.909 CenterZ=0 NormalX=0 NormalY=0 NormalZ=1 AngleXU=0 Radius=1.25 StartAngle=3.14159 EndAngle=4.71239
    g89: LineSegment StartX=205.189 StartY=114.909 StartZ=0 EndX=205.189 EndY=127.908 EndZ=0
    g90: GeomPoint X=205.189 Y=129.158 Z=0
    g91: GeomPoint X=220.689 Y=113.659 Z=0
    g92: ArcOfCircle CenterX=225.516 CenterY=127.908 CenterZ=0 NormalX=0 NormalY=0 NormalZ=1 AngleXU=0 Radius=1.25 StartAngle=1.5708 EndAngle=3.14159
    g93: LineSegment StartX=225.516 StartY=129.158 StartZ=0 EndX=238.516 EndY=129.158 EndZ=0
    g94: ArcOfCircle CenterX=238.516 CenterY=127.908 CenterZ=0 NormalX=0 NormalY=0 NormalZ=1 AngleXU=0 Radius=1.25 StartAngle=3.7e-15 EndAngle=1.5708
    g95: LineSegment StartX=239.766 StartY=127.908 StartZ=0 EndX=239.766 EndY=114.909 EndZ=0
    g96: ArcOfCircle CenterX=238.516 CenterY=114.909 CenterZ=0 NormalX=0 NormalY=0 NormalZ=1 AngleXU=0 Radius=1.25 StartAngle=4.71239 EndAngle=6.28319
    g97: LineSegment StartX=238.516 StartY=113.659 StartZ=0 EndX=225.516 EndY=113.659 EndZ=0
    g98: ArcOfCircle CenterX=225.516 CenterY=114.909 CenterZ=0 NormalX=0 NormalY=0 NormalZ=1 AngleXU=0 Radius=1.25 StartAngle=3.14159 EndAngle=4.71239
    g99: LineSegment StartX=224.266 StartY=114.909 StartZ=0 EndX=224.266 EndY=127.908 EndZ=0
    g100: GeomPoint X=224.266 Y=129.158 Z=0
    g101: GeomPoint X=239.766 Y=113.659 Z=0
    g102: LineSegment StartX=239.766 StartY=127.908 StartZ=0 EndX=243.342 EndY=127.909 EndZ=0
    g103: LineSegment StartX=224.266 StartY=127.908 StartZ=0 EndX=220.689 EndY=127.908 EndZ=0
    g104: LineSegment StartX=205.189 StartY=127.908 StartZ=0 EndX=201.613 EndY=127.908 EndZ=0
    g105: LineSegment StartX=68.0766 StartY=127.908 StartZ=0 EndX=71.6532 EndY=127.908 EndZ=0
    g106: LineSegment StartX=52.5766 StartY=127.908 StartZ=0 EndX=49 EndY=127.909 EndZ=0
    g107: LineSegment StartX=87.1532 StartY=127.908 StartZ=0 EndX=90.7298 EndY=127.908 EndZ=0
    g108: LineSegment StartX=106.23 StartY=127.908 StartZ=0 EndX=109.806 EndY=127.908 EndZ=0
    g109: LineSegment StartX=125.306 StartY=127.908 StartZ=0 EndX=128.883 EndY=127.908 EndZ=0
    g110: LineSegment StartX=144.383 StartY=127.908 StartZ=0 EndX=147.96 EndY=127.908 EndZ=0
    g111: LineSegment StartX=163.46 StartY=127.908 StartZ=0 EndX=167.036 EndY=127.908 EndZ=0
    g112: LineSegment StartX=182.536 StartY=127.908 StartZ=0 EndX=186.113 EndY=127.908 EndZ=0
  constraints (266):
    c: Coincident(g0,g-6)
    c: Coincident(g0,g-3)
    c: Coincident(g1,g-5)
    c: Coincident(g1,g-8)
    c: Tangent(g2,g3) = 1.5708
    c: Tangent(g3,g4) = 1.5708
    c: Tangent(g4,g5) = 1.5708
    c: Tangent(g5,g6) = 1.5708
    c: Tangent(g6,g7) = 1.5708
    c: Tangent(g7,g8) = 1.5708
    c: Tangent(g8,g9) = 1.5708
    c: Tangent(g9,g2) = 1.5708
    c: Horizontal(g3)
    c: Horizontal(g7)
    c: Vertical(g5)
    c: Vertical(g9)
    c: Equal(g2,g4)
    c: Equal(g4,g6)
    c: Equal(g6,g8)
    c: PointOnObject(g10,g3)
    c: PointOnObject(g10,g9)
    c: PointOnObject(g11,g5)
    c: PointOnObject(g11,g7)
    c: PointOnObject(g10,g0)
    c: PointOnObject(g11,g1)
    c: Tangent(g12,g13) = 1.5708
    c: Tangent(g13,g14) = 1.5708
    c: Tangent(g14,g15) = 1.5708
    c: Tangent(g15,g16) = 1.5708
    c: Tangent(g16,g17) = 1.5708
    c: Tangent(g17,g18) = 1.5708
    c: Tangent(g18,g19) = 1.5708
    c: Tangent(g19,g12) = 1.5708
    c: Horizontal(g13)
    c: Horizontal(g17)
    c: Vertical(g15)
    c: Vertical(g19)
    c: Equal(g12,g14)
    c: Equal(g14,g16)
    c: Equal(g16,g18)
    c: PointOnObject(g20,g13)
    c: PointOnObject(g20,g19)
    c: PointOnObject(g21,g15)
    c: PointOnObject(g21,g17)
    c: PointOnObject(g20,g0)
    c: PointOnObject(g21,g1)
    c: Tangent(g22,g23) = 1.5708
    c: Tangent(g23,g24) = 1.5708
    c: Tangent(g24,g25) = 1.5708
    c: Tangent(g25,g26) = 1.5708
    c: Tangent(g26,g27) = 1.5708
    c: Tangent(g27,g28) = 1.5708
    c: Tangent(g28,g29) = 1.5708
    c: Tangent(g29,g22) = 1.5708
    c: Horizontal(g23)
    c: Horizontal(g27)
    c: Vertical(g25)
    c: Vertical(g29)
    c: Equal(g22,g24)
    c: Equal(g24,g26)
    c: Equal(g26,g28)
    c: PointOnObject(g30,g23)
    c: PointOnObject(g30,g29)
    c: PointOnObject(g31,g25)
    c: PointOnObject(g31,g27)
    c: PointOnObject(g30,g0)
    c: PointOnObject(g31,g1)
    c: Tangent(g32,g33) = 1.5708
    c: Tangent(g33,g34) = 1.5708
    c: Tangent(g34,g35) = 1.5708
    c: Tangent(g35,g36) = 1.5708
    c: Tangent(g36,g37) = 1.5708
    c: Tangent(g37,g38) = 1.5708
    c: Tangent(g38,g39) = 1.5708
    c: Tangent(g39,g32) = 1.5708
    c: Horizontal(g33)
    c: Horizontal(g37)
    c: Vertical(g35)
    c: Vertical(g39)
    c: Equal(g32,g34)
    c: Equal(g34,g36)
    c: Equal(g36,g38)
    c: PointOnObject(g40,g33)
    c: PointOnObject(g40,g39)
    c: PointOnObject(g41,g35)
    c: PointOnObject(g41,g37)
    c: PointOnObject(g40,g0)
    c: PointOnObject(g41,g1)
    c: Tangent(g42,g43) = 1.5708
    c: Tangent(g43,g44) = 1.5708
    c: Tangent(g44,g45) = 1.5708
    c: Tangent(g45,g46) = 1.5708
    c: Tangent(g46,g47) = 1.5708
    c: Tangent(g47,g48) = 1.5708
    c: Tangent(g48,g49) = 1.5708
    c: Tangent(g49,g42) = 1.5708
    c: Horizontal(g43)
    c: Horizontal(g47)
    c: Vertical(g45)
    c: Vertical(g49)
    c: Equal(g42,g44)
    c: Equal(g44,g46)
    c: Equal(g46,g48)
    c: PointOnObject(g50,g43)
    c: PointOnObject(g50,g49)
    c: PointOnObject(g51,g45)
    c: PointOnObject(g51,g47)
    c: PointOnObject(g50,g0)
    c: PointOnObject(g51,g1)
    c: Tangent(g52,g53) = 1.5708
    c: Tangent(g53,g54) = 1.5708
    c: Tangent(g54,g55) = 1.5708
    c: Tangent(g55,g56) = 1.5708
    c: Tangent(g56,g57) = 1.5708
    c: Tangent(g57,g58) = 1.5708
    c: Tangent(g58,g59) = 1.5708
    c: Tangent(g59,g52) = 1.5708
    c: Horizontal(g53)
    c: Horizontal(g57)
    c: Vertical(g55)
    c: Vertical(g59)
    c: Equal(g52,g54)
    c: Equal(g54,g56)
    c: Equal(g56,g58)
    c: PointOnObject(g60,g53)
    c: PointOnObject(g60,g59)
    c: PointOnObject(g61,g55)
    c: PointOnObject(g61,g57)
    c: PointOnObject(g60,g0)
    c: PointOnObject(g61,g1)
    c: Tangent(g62,g63) = 1.5708
    c: Tangent(g63,g64) = 1.5708
    c: Tangent(g64,g65) = 1.5708
    c: Tangent(g65,g66) = 1.5708
    c: Tangent(g66,g67) = 1.5708
    c: Tangent(g67,g68) = 1.5708
    c: Tangent(g68,g69) = 1.5708
    c: Tangent(g69,g62) = 1.5708
    c: Horizontal(g63)
    c: Horizontal(g67)
    c: Vertical(g65)
    c: Vertical(g69)
    c: Equal(g62,g64)
    c: Equal(g64,g66)
    c: Equal(g66,g68)
    c: PointOnObject(g70,g63)
    c: PointOnObject(g70,g69)
    c: PointOnObject(g71,g65)
    c: PointOnObject(g71,g67)
    c: PointOnObject(g70,g0)
    c: PointOnObject(g71,g1)
    c: Tangent(g72,g73) = 1.5708
    c: Tangent(g73,g74) = 1.5708
    c: Tangent(g74,g75) = 1.5708
    c: Tangent(g75,g76) = 1.5708
    c: Tangent(g76,g77) = 1.5708
    c: Tangent(g77,g78) = 1.5708
    c: Tangent(g78,g79) = 1.5708
    c: Tangent(g79,g72) = 1.5708
    c: Horizontal(g73)
    c: Horizontal(g77)
    c: Vertical(g75)
    c: Vertical(g79)
    c: Equal(g72,g74)
    c: Equal(g74,g76)
    c: Equal(g76,g78)
    c: PointOnObject(g80,g73)
    c: PointOnObject(g80,g79)
    c: PointOnObject(g81,g75)
    c: PointOnObject(g81,g77)
    c: PointOnObject(g80,g0)
    c: PointOnObject(g81,g1)
    c: Tangent(g82,g83) = 1.5708
    c: Tangent(g83,g84) = 1.5708
    c: Tangent(g84,g85) = 1.5708
    c: Tangent(g85,g86) = 1.5708
    c: Tangent(g86,g87) = 1.5708
    c: Tangent(g87,g88) = 1.5708
    c: Tangent(g88,g89) = 1.5708
    c: Tangent(g89,g82) = 1.5708
    c: Horizontal(g83)
    c: Horizontal(g87)
    c: Vertical(g85)
    c: Vertical(g89)
    c: Equal(g82,g84)
    c: Equal(g84,g86)
    c: Equal(g86,g88)
    c: PointOnObject(g90,g83)
    c: PointOnObject(g90,g89)
    c: PointOnObject(g91,g85)
    c: PointOnObject(g91,g87)
    c: PointOnObject(g90,g0)
    c: PointOnObject(g91,g1)
    c: Tangent(g92,g93) = 1.5708
    c: Tangent(g93,g94) = 1.5708
    c: Tangent(g94,g95) = 1.5708
    c: Tangent(g95,g96) = 1.5708
    c: Tangent(g96,g97) = 1.5708
    c: Tangent(g97,g98) = 1.5708
    c: Tangent(g98,g99) = 1.5708
    c: Tangent(g99,g92) = 1.5708
    c: Horizontal(g93)
    c: Horizontal(g97)
    c: Vertical(g95)
    c: Vertical(g99)
    c: Equal(g92,g94)
    c: Equal(g94,g96)
    c: Equal(g96,g98)
    c: PointOnObject(g100,g93)
    c: PointOnObject(g100,g99)
    c: PointOnObject(g101,g95)
    c: PointOnObject(g101,g97)
    c: PointOnObject(g100,g0)
    c: PointOnObject(g101,g1)
    c: Equal(g-6,g2)
    c: Equal(g4,g12)
    c: Equal(g3,g13)
    c: Equal(g14,g22)
    c: Equal(g13,g23)
    c: Equal(g24,g32)
    c: Equal(g23,g33)
    c: Equal(g34,g42)
    c: Equal(g33,g43)
    c: Equal(g44,g52)
    c: Equal(g43,g53)
    c: Equal(g54,g62)
    c: Equal(g53,g63)
    c: Equal(g64,g72)
    c: Equal(g63,g73)
    c: Equal(g74,g82)
    c: Equal(g73,g83)
    c: Equal(g84,g92)
    c: Equal(g83,g93)
    c: Coincident(g102,g94)
    c: Coincident(g103,g92)
    c: Coincident(g104,g82)
    c: Coincident(g105,g4)
    c: Coincident(g106,g2)
    c: Coincident(g107,g14)
    c: Coincident(g108,g24)
    c: Coincident(g109,g34)
    c: Coincident(g110,g44)
    c: Coincident(g111,g54)
    c: Coincident(g112,g64)
    c: Equal(g102,g103)
    c: Equal(g103,g104)
    c: Equal(g112,g104)
    c: Equal(g112,g111)
    c: Equal(g111,g110)
    c: Equal(g110,g109)
    c: Equal(g109,g108)
    c: Equal(g108,g107)
    c: Equal(g107,g105)
    c: Equal(g105,g106)
    c: Coincident(g-7,g106)
    c: Coincident(g105,g12)
    c: Coincident(g107,g22)
    c: Coincident(g108,g32)
    c: Coincident(g109,g42)
    c: Coincident(g110,g52)
    c: Coincident(g111,g62)
    c: Coincident(g112,g72)
    c: Coincident(g104,g74)
    c: Coincident(g103,g84)
    c: Coincident(g102,g-4)
    c: Equal(g3,g9)
FEATURE [Sketcher::SketchObject] Sketch011
  ExternalGeometry = -> [Sketch,Sketch009]
  FullyConstrained = true
  MapMode = 2
  Placement = pos=(0,0,12.53) rot=(0,0,1;0rad)
  Support = -> [Sketch010]
  sketch-geometry (259):
    g0: LineSegment StartX=253.505 StartY=132.817 StartZ=0 EndX=37.75 EndY=132.817 EndZ=0
    g1: LineSegment StartX=37.75 StartY=148.317 StartZ=0 EndX=253.505 EndY=148.317 EndZ=0
    g2: ArcOfCircle CenterX=247.442 CenterY=147.067 CenterZ=0 NormalX=0 NormalY=0 NormalZ=1 AngleXU=0 Radius=1.25 StartAngle=2e-15 EndAngle=1.5708
    g3: LineSegment StartX=248.692 StartY=147.067 StartZ=0 EndX=248.692 EndY=134.067 EndZ=0
    g4: ArcOfCircle CenterX=247.442 CenterY=134.067 CenterZ=0 NormalX=0 NormalY=0 NormalZ=1 AngleXU=0 Radius=1.25 StartAngle=4.71239 EndAngle=6.28319
    g5: LineSegment StartX=247.442 StartY=132.817 StartZ=0 EndX=234.442 EndY=132.817 EndZ=0
    g6: ArcOfCircle CenterX=234.442 CenterY=134.067 CenterZ=0 NormalX=0 NormalY=0 NormalZ=1 AngleXU=0 Radius=1.25 StartAngle=3.14159 EndAngle=4.71239
    g7: LineSegment StartX=233.192 StartY=134.067 StartZ=0 EndX=233.192 EndY=147.067 EndZ=0
    g8: ArcOfCircle CenterX=234.442 CenterY=147.067 CenterZ=0 NormalX=0 NormalY=0 NormalZ=1 AngleXU=0 Radius=1.25 StartAngle=1.5708 EndAngle=3.14159
    g9: LineSegment StartX=234.442 StartY=148.317 StartZ=0 EndX=247.442 EndY=148.317 EndZ=0
    g10: GeomPoint X=248.692 Y=148.317 Z=0
    g11: GeomPoint X=233.192 Y=132.817 Z=0
    g12: ArcOfCircle CenterX=228.379 CenterY=134.067 CenterZ=0 NormalX=0 NormalY=0 NormalZ=1 AngleXU=0 Radius=1.25 StartAngle=4.71239 EndAngle=6.28319
    g13: LineSegment StartX=228.379 StartY=132.817 StartZ=0 EndX=215.379 EndY=132.817 EndZ=0
    g14: ArcOfCircle CenterX=215.379 CenterY=134.067 CenterZ=0 NormalX=0 NormalY=0 NormalZ=1 AngleXU=0 Radius=1.25 StartAngle=3.14159 EndAngle=4.71239
    g15: LineSegment StartX=214.129 StartY=134.067 StartZ=0 EndX=214.129 EndY=147.067 EndZ=0
    g16: ArcOfCircle CenterX=215.379 CenterY=147.067 CenterZ=0 NormalX=0 NormalY=0 NormalZ=1 AngleXU=0 Radius=1.25 StartAngle=1.5708 EndAngle=3.14159
    g17: LineSegment StartX=215.379 StartY=148.317 StartZ=0 EndX=228.379 EndY=148.317 EndZ=0
    g18: ArcOfCircle CenterX=228.379 CenterY=147.067 CenterZ=0 NormalX=0 NormalY=0 NormalZ=1 AngleXU=0 Radius=1.25 StartAngle=5.2e-15 EndAngle=1.5708
    g19: LineSegment StartX=229.629 StartY=147.067 StartZ=0 EndX=229.629 EndY=134.067 EndZ=0
    g20: GeomPoint X=229.629 Y=132.817 Z=0
    g21: GeomPoint X=214.129 Y=148.317 Z=0
    g22: ArcOfCircle CenterX=209.316 CenterY=134.067 CenterZ=0 NormalX=0 NormalY=0 NormalZ=1 AngleXU=0 Radius=1.25 StartAngle=4.71239 EndAngle=6.28319
    g23: LineSegment StartX=209.316 StartY=132.817 StartZ=0 EndX=196.316 EndY=132.817 EndZ=0
    g24: ArcOfCircle CenterX=196.316 CenterY=134.067 CenterZ=0 NormalX=0 NormalY=0 NormalZ=1 AngleXU=0 Radius=1.25 StartAngle=3.14159 EndAngle=4.71239
    g25: LineSegment StartX=195.066 StartY=134.067 StartZ=0 EndX=195.066 EndY=147.067 EndZ=0
    g26: ArcOfCircle CenterX=196.316 CenterY=147.067 CenterZ=0 NormalX=0 NormalY=0 NormalZ=1 AngleXU=0 Radius=1.25 StartAngle=1.5708 EndAngle=3.14159
    g27: LineSegment StartX=196.316 StartY=148.317 StartZ=0 EndX=209.316 EndY=148.317 EndZ=0
    g28: ArcOfCircle CenterX=209.316 CenterY=147.067 CenterZ=0 NormalX=0 NormalY=0 NormalZ=1 AngleXU=0 Radius=1.25 StartAngle=8.3e-15 EndAngle=1.5708
    g29: LineSegment StartX=210.566 StartY=147.067 StartZ=0 EndX=210.566 EndY=134.067 EndZ=0
    g30: GeomPoint X=210.566 Y=132.817 Z=0
    g31: GeomPoint X=195.066 Y=148.317 Z=0
    g32: ArcOfCircle CenterX=190.253 CenterY=147.067 CenterZ=0 NormalX=0 NormalY=0 NormalZ=1 AngleXU=0 Radius=1.25 StartAngle=-3.6e-15 EndAngle=1.5708
    g33: LineSegment StartX=191.503 StartY=147.067 StartZ=0 EndX=191.503 EndY=134.067 EndZ=0
    g34: ArcOfCircle CenterX=190.253 CenterY=134.067 CenterZ=0 NormalX=0 NormalY=0 NormalZ=1 AngleXU=0 Radius=1.25 StartAngle=4.71239 EndAngle=6.28319
    g35: LineSegment StartX=190.253 StartY=132.817 StartZ=0 EndX=177.253 EndY=132.817 EndZ=0
    g36: ArcOfCircle CenterX=177.253 CenterY=134.067 CenterZ=0 NormalX=0 NormalY=0 NormalZ=1 AngleXU=0 Radius=1.25 StartAngle=3.14159 EndAngle=4.71239
    g37: LineSegment StartX=176.003 StartY=134.067 StartZ=0 EndX=176.003 EndY=147.067 EndZ=0
    g38: ArcOfCircle CenterX=177.253 CenterY=147.067 CenterZ=0 NormalX=0 NormalY=0 NormalZ=1 AngleXU=0 Radius=1.25 StartAngle=1.5708 EndAngle=3.14159
    g39: LineSegment StartX=177.253 StartY=148.317 StartZ=0 EndX=190.253 EndY=148.317 EndZ=0
    g40: GeomPoint X=191.503 Y=148.317 Z=0
    g41: GeomPoint X=176.003 Y=132.817 Z=0
    g42: ArcOfCircle CenterX=171.19 CenterY=134.067 CenterZ=0 NormalX=0 NormalY=0 NormalZ=1 AngleXU=0 Radius=1.25 StartAngle=4.71239 EndAngle=6.28319
    g43: LineSegment StartX=171.19 StartY=132.817 StartZ=0 EndX=158.19 EndY=132.817 EndZ=0
    g44: ArcOfCircle CenterX=158.19 CenterY=134.067 CenterZ=0 NormalX=0 NormalY=0 NormalZ=1 AngleXU=0 Radius=1.25 StartAngle=3.14159 EndAngle=4.71239
    g45: LineSegment StartX=156.94 StartY=134.067 StartZ=0 EndX=156.94 EndY=147.067 EndZ=0
    g46: ArcOfCircle CenterX=158.19 CenterY=147.067 CenterZ=0 NormalX=0 NormalY=0 NormalZ=1 AngleXU=0 Radius=1.25 StartAngle=1.5708 EndAngle=3.14159
    g47: LineSegment StartX=158.19 StartY=148.317 StartZ=0 EndX=171.19 EndY=148.317 EndZ=0
    g48: ArcOfCircle CenterX=171.19 CenterY=147.067 CenterZ=0 NormalX=0 NormalY=0 NormalZ=1 AngleXU=0 Radius=1.25 StartAngle=5.9e-15 EndAngle=1.5708
    g49: LineSegment StartX=172.44 StartY=147.067 StartZ=0 EndX=172.44 EndY=134.067 EndZ=0
    g50: GeomPoint X=172.44 Y=132.817 Z=0
    g51: GeomPoint X=156.94 Y=148.317 Z=0
    g52: ArcOfCircle CenterX=152.127 CenterY=147.067 CenterZ=0 NormalX=0 NormalY=0 NormalZ=1 AngleXU=0 Radius=1.25 StartAngle=-3.6e-15 EndAngle=1.5708
    g53: LineSegment StartX=153.377 StartY=147.067 StartZ=0 EndX=153.377 EndY=134.067 EndZ=0
    g54: ArcOfCircle CenterX=152.127 CenterY=134.067 CenterZ=0 NormalX=0 NormalY=0 NormalZ=1 AngleXU=0 Radius=1.25 StartAngle=4.71239 EndAngle=6.28319
    g55: LineSegment StartX=152.127 StartY=132.817 StartZ=0 EndX=139.128 EndY=132.817 EndZ=0
    g56: ArcOfCircle CenterX=139.128 CenterY=134.067 CenterZ=0 NormalX=0 NormalY=0 NormalZ=1 AngleXU=0 Radius=1.25 StartAngle=3.14159 EndAngle=4.71239
    g57: LineSegment StartX=137.878 StartY=134.067 StartZ=0 EndX=137.878 EndY=147.067 EndZ=0
    g58: ArcOfCircle CenterX=139.128 CenterY=147.067 CenterZ=0 NormalX=0 NormalY=0 NormalZ=1 AngleXU=0 Radius=1.25 StartAngle=1.5708 EndAngle=3.14159
    g59: LineSegment StartX=139.128 StartY=148.317 StartZ=0 EndX=152.127 EndY=148.317 EndZ=0
    g60: GeomPoint X=153.377 Y=148.317 Z=0
    g61: GeomPoint X=137.878 Y=132.817 Z=0
    g62: ArcOfCircle CenterX=133.065 CenterY=134.067 CenterZ=0 NormalX=0 NormalY=0 NormalZ=1 AngleXU=0 Radius=1.25 StartAngle=4.71239 EndAngle=6.28319
    g63: LineSegment StartX=133.065 StartY=132.817 StartZ=0 EndX=120.065 EndY=132.817 EndZ=0
    g64: ArcOfCircle CenterX=120.065 CenterY=134.067 CenterZ=0 NormalX=0 NormalY=0 NormalZ=1 AngleXU=0 Radius=1.25 StartAngle=3.14159 EndAngle=4.71239
    g65: LineSegment StartX=118.815 StartY=134.067 StartZ=0 EndX=118.815 EndY=147.067 EndZ=0
    g66: ArcOfCircle CenterX=120.065 CenterY=147.067 CenterZ=0 NormalX=0 NormalY=0 NormalZ=1 AngleXU=0 Radius=1.25 StartAngle=1.5708 EndAngle=3.14159
    g67: LineSegment StartX=120.065 StartY=148.317 StartZ=0 EndX=133.065 EndY=148.317 EndZ=0
    g68: ArcOfCircle CenterX=133.065 CenterY=147.067 CenterZ=0 NormalX=0 NormalY=0 NormalZ=1 AngleXU=0 Radius=1.25 StartAngle=7.6e-15 EndAngle=1.5708
    g69: LineSegment StartX=134.315 StartY=147.067 StartZ=0 EndX=134.315 EndY=134.067 EndZ=0
    g70: GeomPoint X=134.315 Y=132.817 Z=0
    g71: GeomPoint X=118.815 Y=148.317 Z=0
    g72: ArcOfCircle CenterX=114.002 CenterY=147.067 CenterZ=0 NormalX=0 NormalY=0 NormalZ=1 AngleXU=0 Radius=1.25 StartAngle=4.9e-15 EndAngle=1.5708
    g73: LineSegment StartX=115.252 StartY=147.067 StartZ=0 EndX=115.252 EndY=134.067 EndZ=0
    g74: ArcOfCircle CenterX=114.002 CenterY=134.067 CenterZ=0 NormalX=0 NormalY=0 NormalZ=1 AngleXU=0 Radius=1.25 StartAngle=4.71239 EndAngle=6.28319
    g75: LineSegment StartX=114.002 StartY=132.817 StartZ=0 EndX=101.002 EndY=132.817 EndZ=0
    g76: ArcOfCircle CenterX=101.002 CenterY=134.067 CenterZ=0 NormalX=0 NormalY=0 NormalZ=1 AngleXU=0 Radius=1.25 StartAngle=3.14159 EndAngle=4.71239
    g77: LineSegment StartX=99.7517 StartY=134.067 StartZ=0 EndX=99.7517 EndY=147.067 EndZ=0
    g78: ArcOfCircle CenterX=101.002 CenterY=147.067 CenterZ=0 NormalX=0 NormalY=0 NormalZ=1 AngleXU=0 Radius=1.25 StartAngle=1.5708 EndAngle=3.14159
    g79: LineSegment StartX=101.002 StartY=148.317 StartZ=0 EndX=114.002 EndY=148.317 EndZ=0
    g80: GeomPoint X=115.252 Y=148.317 Z=0
    g81: GeomPoint X=99.7517 Y=132.817 Z=0
    g82: ArcOfCircle CenterX=94.9387 CenterY=147.067 CenterZ=0 NormalX=0 NormalY=0 NormalZ=1 AngleXU=0 Radius=1.25 StartAngle=5e-16 EndAngle=1.5708
    g83: LineSegment StartX=96.1887 StartY=147.067 StartZ=0 EndX=96.1887 EndY=134.067 EndZ=0
    g84: ArcOfCircle CenterX=94.9387 CenterY=134.067 CenterZ=0 NormalX=0 NormalY=0 NormalZ=1 AngleXU=0 Radius=1.25 StartAngle=4.71239 EndAngle=6.28319
    g85: LineSegment StartX=94.9387 StartY=132.817 StartZ=0 EndX=81.9388 EndY=132.817 EndZ=0
    g86: ArcOfCircle CenterX=81.9388 CenterY=134.067 CenterZ=0 NormalX=0 NormalY=0 NormalZ=1 AngleXU=0 Radius=1.25 StartAngle=3.14159 EndAngle=4.71239
    g87: LineSegment StartX=80.6888 StartY=134.067 StartZ=0 EndX=80.6888 EndY=147.067 EndZ=0
    g88: ArcOfCircle CenterX=81.9388 CenterY=147.067 CenterZ=0 NormalX=0 NormalY=0 NormalZ=1 AngleXU=0 Radius=1.25 StartAngle=1.5708 EndAngle=3.14159
    g89: LineSegment StartX=81.9388 StartY=148.317 StartZ=0 EndX=94.9387 EndY=148.317 EndZ=0
    g90: GeomPoint X=96.1887 Y=148.317 Z=0
    g91: GeomPoint X=80.6888 Y=132.817 Z=0
    g92: ArcOfCircle CenterX=75.8758 CenterY=147.067 CenterZ=0 NormalX=0 NormalY=0 NormalZ=1 AngleXU=0 Radius=1.25 StartAngle=-8e-15 EndAngle=1.5708
    g93: LineSegment StartX=77.1258 StartY=147.067 StartZ=0 EndX=77.1258 EndY=134.067 EndZ=0
    g94: ArcOfCircle CenterX=75.8758 CenterY=134.067 CenterZ=0 NormalX=0 NormalY=0 NormalZ=1 AngleXU=0 Radius=1.25 StartAngle=4.71239 EndAngle=6.28319
    g95: LineSegment StartX=75.8758 StartY=132.817 StartZ=0 EndX=62.8758 EndY=132.817 EndZ=0
    g96: ArcOfCircle CenterX=62.8758 CenterY=134.067 CenterZ=0 NormalX=0 NormalY=0 NormalZ=1 AngleXU=0 Radius=1.25 StartAngle=3.14159 EndAngle=4.71239
    g97: LineSegment StartX=61.6258 StartY=134.067 StartZ=0 EndX=61.6258 EndY=147.067 EndZ=0
    g98: ArcOfCircle CenterX=62.8758 CenterY=147.067 CenterZ=0 NormalX=0 NormalY=0 NormalZ=1 AngleXU=0 Radius=1.25 StartAngle=1.5708 EndAngle=3.14159
    g99: LineSegment StartX=62.8758 StartY=148.317 StartZ=0 EndX=75.8758 EndY=148.317 EndZ=0
    g100: GeomPoint X=77.1258 Y=148.317 Z=0
    g101: GeomPoint X=61.6258 Y=132.817 Z=0
    g102: ArcOfCircle CenterX=56.8129 CenterY=134.067 CenterZ=0 NormalX=0 NormalY=0 NormalZ=1 AngleXU=0 Radius=1.25 StartAngle=4.71239 EndAngle=6.28319
    g103: LineSegment StartX=56.8129 StartY=132.817 StartZ=0 EndX=43.8129 EndY=132.817 EndZ=0
    g104: ArcOfCircle CenterX=43.8129 CenterY=134.067 CenterZ=0 NormalX=0 NormalY=0 NormalZ=1 AngleXU=0 Radius=1.25 StartAngle=3.14159 EndAngle=4.71239
    g105: LineSegment StartX=42.5629 StartY=134.067 StartZ=0 EndX=42.5629 EndY=147.067 EndZ=0
    g106: ArcOfCircle CenterX=43.8129 CenterY=147.067 CenterZ=0 NormalX=0 NormalY=0 NormalZ=1 AngleXU=0 Radius=1.25 StartAngle=1.5708 EndAngle=3.14159
    g107: LineSegment StartX=43.8129 StartY=148.317 StartZ=0 EndX=56.8129 EndY=148.317 EndZ=0
    g108: ArcOfCircle CenterX=56.8129 CenterY=147.067 CenterZ=0 NormalX=0 NormalY=0 NormalZ=1 AngleXU=0 Radius=1.25 StartAngle=2.7e-15 EndAngle=1.5708
    g109: LineSegment StartX=58.0629 StartY=147.067 StartZ=0 EndX=58.0629 EndY=134.067 EndZ=0
    g110: GeomPoint X=58.0629 Y=132.817 Z=0
    g111: GeomPoint X=42.5629 Y=148.317 Z=0
    g112: LineSegment StartX=39 StartY=147.067 StartZ=0 EndX=42.5629 EndY=147.067 EndZ=0
    g113: LineSegment StartX=58.0629 StartY=147.067 StartZ=0 EndX=61.6258 EndY=147.067 EndZ=0
    g114: LineSegment StartX=77.1258 StartY=147.067 StartZ=0 EndX=80.6888 EndY=147.067 EndZ=0
    g115: LineSegment StartX=96.1887 StartY=147.067 StartZ=0 EndX=99.7517 EndY=147.067 EndZ=0
    g116: LineSegment StartX=115.252 StartY=147.067 StartZ=0 EndX=118.815 EndY=147.067 EndZ=0
    g117: LineSegment StartX=134.315 StartY=147.067 StartZ=0 EndX=137.878 EndY=147.067 EndZ=0
    g118: LineSegment StartX=153.377 StartY=147.067 StartZ=0 EndX=156.94 EndY=147.067 EndZ=0
    g119: LineSegment StartX=172.44 StartY=147.067 StartZ=0 EndX=176.003 EndY=147.067 EndZ=0
    g120: LineSegment StartX=191.503 StartY=147.067 StartZ=0 EndX=195.066 EndY=147.067 EndZ=0
    g121: LineSegment StartX=210.566 StartY=147.067 StartZ=0 EndX=214.129 EndY=147.067 EndZ=0
    g122: LineSegment StartX=229.629 StartY=147.067 StartZ=0 EndX=233.192 EndY=147.067 EndZ=0
    g123: LineSegment StartX=248.692 StartY=147.067 StartZ=0 EndX=252.255 EndY=147.067 EndZ=0
    g124: LineSegment StartX=267.88 StartY=167.476 StartZ=0 EndX=32.75 EndY=167.476 EndZ=0
    g125: LineSegment StartX=32.75 StartY=151.976 StartZ=0 EndX=267.88 EndY=151.976 EndZ=0
    g126: ArcOfCircle CenterX=261.793 CenterY=166.226 CenterZ=0 NormalX=0 NormalY=0 NormalZ=1 AngleXU=0 Radius=1.25 StartAngle=7.6e-15 EndAngle=1.5708
    g127: LineSegment StartX=263.043 StartY=166.226 StartZ=0 EndX=263.043 EndY=153.226 EndZ=0
    g128: ArcOfCircle CenterX=261.793 CenterY=153.226 CenterZ=0 NormalX=0 NormalY=0 NormalZ=1 AngleXU=0 Radius=1.25 StartAngle=4.71239 EndAngle=6.28319
    g129: LineSegment StartX=261.793 StartY=151.976 StartZ=0 EndX=248.793 EndY=151.976 EndZ=0
    g130: ArcOfCircle CenterX=248.793 CenterY=153.226 CenterZ=0 NormalX=0 NormalY=0 NormalZ=1 AngleXU=0 Radius=1.25 StartAngle=3.14159 EndAngle=4.71239
    g131: LineSegment StartX=247.543 StartY=153.226 StartZ=0 EndX=247.543 EndY=166.226 EndZ=0
    g132: ArcOfCircle CenterX=248.793 CenterY=166.226 CenterZ=0 NormalX=0 NormalY=0 NormalZ=1 AngleXU=0 Radius=1.25 StartAngle=1.5708 EndAngle=3.14159
    g133: LineSegment StartX=248.793 StartY=167.476 StartZ=0 EndX=261.793 EndY=167.476 EndZ=0
    g134: GeomPoint X=263.043 Y=167.476 Z=0
    g135: GeomPoint X=247.543 Y=151.976 Z=0
    g136: ArcOfCircle CenterX=242.706 CenterY=166.226 CenterZ=0 NormalX=0 NormalY=0 NormalZ=1 AngleXU=0 Radius=1.25 StartAngle=-2.7e-15 EndAngle=1.5708
    g137: LineSegment StartX=243.956 StartY=166.226 StartZ=0 EndX=243.956 EndY=153.226 EndZ=0
    g138: ArcOfCircle CenterX=242.706 CenterY=153.226 CenterZ=0 NormalX=0 NormalY=0 NormalZ=1 AngleXU=0 Radius=1.25 StartAngle=4.71239 EndAngle=6.28319
    g139: LineSegment StartX=242.706 StartY=151.976 StartZ=0 EndX=229.706 EndY=151.976 EndZ=0
    g140: ArcOfCircle CenterX=229.706 CenterY=153.226 CenterZ=0 NormalX=0 NormalY=0 NormalZ=1 AngleXU=0 Radius=1.25 StartAngle=3.14159 EndAngle=4.71239
    g141: LineSegment StartX=228.456 StartY=153.226 StartZ=0 EndX=228.456 EndY=166.226 EndZ=0
    g142: ArcOfCircle CenterX=229.706 CenterY=166.226 CenterZ=0 NormalX=0 NormalY=0 NormalZ=1 AngleXU=0 Radius=1.25 StartAngle=1.5708 EndAngle=3.14159
    g143: LineSegment StartX=229.706 StartY=167.476 StartZ=0 EndX=242.706 EndY=167.476 EndZ=0
    g144: GeomPoint X=243.956 Y=167.476 Z=0
    g145: GeomPoint X=228.456 Y=151.976 Z=0
    g146: ArcOfCircle CenterX=223.619 CenterY=166.226 CenterZ=0 NormalX=0 NormalY=0 NormalZ=1 AngleXU=0 Radius=1.25 StartAngle=-2.7e-15 EndAngle=1.5708
    g147: LineSegment StartX=224.869 StartY=166.226 StartZ=0 EndX=224.869 EndY=153.226 EndZ=0
    g148: ArcOfCircle CenterX=223.619 CenterY=153.226 CenterZ=0 NormalX=0 NormalY=0 NormalZ=1 AngleXU=0 Radius=1.25 StartAngle=4.71239 EndAngle=6.28319
    g149: LineSegment StartX=223.619 StartY=151.976 StartZ=0 EndX=210.619 EndY=151.976 EndZ=0
    g150: ArcOfCircle CenterX=210.619 CenterY=153.226 CenterZ=0 NormalX=0 NormalY=0 NormalZ=1 AngleXU=0 Radius=1.25 StartAngle=3.14159 EndAngle=4.71239
    g151: LineSegment StartX=209.369 StartY=153.226 StartZ=0 EndX=209.369 EndY=166.226 EndZ=0
    g152: ArcOfCircle CenterX=210.619 CenterY=166.226 CenterZ=0 NormalX=0 NormalY=0 NormalZ=1 AngleXU=0 Radius=1.25 StartAngle=1.5708 EndAngle=3.14159
    g153: LineSegment StartX=210.619 StartY=167.476 StartZ=0 EndX=223.619 EndY=167.476 EndZ=0
    g154: GeomPoint X=224.869 Y=167.476 Z=0
    g155: GeomPoint X=209.369 Y=151.976 Z=0
    g156: ArcOfCircle CenterX=204.532 CenterY=166.226 CenterZ=0 NormalX=0 NormalY=0 NormalZ=1 AngleXU=0 Radius=1.25 StartAngle=5.2e-15 EndAngle=1.5708
    g157: LineSegment StartX=205.782 StartY=166.226 StartZ=0 EndX=205.782 EndY=153.226 EndZ=0
    g158: ArcOfCircle CenterX=204.532 CenterY=153.226 CenterZ=0 NormalX=0 NormalY=0 NormalZ=1 AngleXU=0 Radius=1.25 StartAngle=4.71239 EndAngle=6.28319
    g159: LineSegment StartX=204.532 StartY=151.976 StartZ=0 EndX=191.532 EndY=151.976 EndZ=0
    g160: ArcOfCircle CenterX=191.532 CenterY=153.226 CenterZ=0 NormalX=0 NormalY=0 NormalZ=1 AngleXU=0 Radius=1.25 StartAngle=3.14159 EndAngle=4.71239
    g161: LineSegment StartX=190.282 StartY=153.226 StartZ=0 EndX=190.282 EndY=166.226 EndZ=0
    g162: ArcOfCircle CenterX=191.532 CenterY=166.226 CenterZ=0 NormalX=0 NormalY=0 NormalZ=1 AngleXU=0 Radius=1.25 StartAngle=1.5708 EndAngle=3.14159
    g163: LineSegment StartX=191.532 StartY=167.476 StartZ=0 EndX=204.532 EndY=167.476 EndZ=0
    g164: GeomPoint X=205.782 Y=167.476 Z=0
    g165: GeomPoint X=190.282 Y=151.976 Z=0
    g166: ArcOfCircle CenterX=185.445 CenterY=166.226 CenterZ=0 NormalX=0 NormalY=0 NormalZ=1 AngleXU=0 Radius=1.25 StartAngle=5e-15 EndAngle=1.5708
    g167: LineSegment StartX=186.695 StartY=166.226 StartZ=0 EndX=186.695 EndY=153.226 EndZ=0
    g168: ArcOfCircle CenterX=185.445 CenterY=153.226 CenterZ=0 NormalX=0 NormalY=0 NormalZ=1 AngleXU=0 Radius=1.25 StartAngle=4.71239 EndAngle=6.28319
    g169: LineSegment StartX=185.445 StartY=151.976 StartZ=0 EndX=172.445 EndY=151.976 EndZ=0
    g170: ArcOfCircle CenterX=172.445 CenterY=153.226 CenterZ=0 NormalX=0 NormalY=0 NormalZ=1 AngleXU=0 Radius=1.25 StartAngle=3.14159 EndAngle=4.71239
    g171: LineSegment StartX=171.195 StartY=153.226 StartZ=0 EndX=171.195 EndY=166.226 EndZ=0
    g172: ArcOfCircle CenterX=172.445 CenterY=166.226 CenterZ=0 NormalX=0 NormalY=0 NormalZ=1 AngleXU=0 Radius=1.25 StartAngle=1.5708 EndAngle=3.14159
    g173: LineSegment StartX=172.445 StartY=167.476 StartZ=0 EndX=185.445 EndY=167.476 EndZ=0
    g174: GeomPoint X=186.695 Y=167.476 Z=0
    g175: GeomPoint X=171.195 Y=151.976 Z=0
    g176: ArcOfCircle CenterX=166.358 CenterY=166.226 CenterZ=0 NormalX=0 NormalY=0 NormalZ=1 AngleXU=0 Radius=1.25 StartAngle=1.3e-15 EndAngle=1.5708
    g177: LineSegment StartX=167.608 StartY=166.226 StartZ=0 EndX=167.608 EndY=153.226 EndZ=0
    g178: ArcOfCircle CenterX=166.358 CenterY=153.226 CenterZ=0 NormalX=0 NormalY=0 NormalZ=1 AngleXU=0 Radius=1.25 StartAngle=4.71239 EndAngle=6.28319
    g179: LineSegment StartX=166.358 StartY=151.976 StartZ=0 EndX=153.358 EndY=151.976 EndZ=0
    g180: ArcOfCircle CenterX=153.358 CenterY=153.226 CenterZ=0 NormalX=0 NormalY=0 NormalZ=1 AngleXU=0 Radius=1.25 StartAngle=3.14159 EndAngle=4.71239
    g181: LineSegment StartX=152.108 StartY=153.226 StartZ=0 EndX=152.108 EndY=166.226 EndZ=0
    g182: ArcOfCircle CenterX=153.358 CenterY=166.226 CenterZ=0 NormalX=0 NormalY=0 NormalZ=1 AngleXU=0 Radius=1.25 StartAngle=1.5708 EndAngle=3.14159
    g183: LineSegment StartX=153.358 StartY=167.476 StartZ=0 EndX=166.358 EndY=167.476 EndZ=0
    g184: GeomPoint X=167.608 Y=167.476 Z=0
    g185: GeomPoint X=152.108 Y=151.976 Z=0
    g186: ArcOfCircle CenterX=147.272 CenterY=166.226 CenterZ=0 NormalX=0 NormalY=0 NormalZ=1 AngleXU=0 Radius=1.25 StartAngle=-7.1e-15 EndAngle=1.5708
    g187: LineSegment StartX=148.522 StartY=166.226 StartZ=0 EndX=148.522 EndY=153.226 EndZ=0
    g188: ArcOfCircle CenterX=147.272 CenterY=153.226 CenterZ=0 NormalX=0 NormalY=0 NormalZ=1 AngleXU=0 Radius=1.25 StartAngle=4.71239 EndAngle=6.28319
    g189: LineSegment StartX=147.272 StartY=151.976 StartZ=0 EndX=134.272 EndY=151.976 EndZ=0
    g190: ArcOfCircle CenterX=134.272 CenterY=153.226 CenterZ=0 NormalX=0 NormalY=0 NormalZ=1 AngleXU=0 Radius=1.25 StartAngle=3.14159 EndAngle=4.71239
    g191: LineSegment StartX=133.022 StartY=153.226 StartZ=0 EndX=133.022 EndY=166.226 EndZ=0
    g192: ArcOfCircle CenterX=134.272 CenterY=166.226 CenterZ=0 NormalX=0 NormalY=0 NormalZ=1 AngleXU=0 Radius=1.25 StartAngle=1.5708 EndAngle=3.14159
    g193: LineSegment StartX=134.272 StartY=167.476 StartZ=0 EndX=147.272 EndY=167.476 EndZ=0
    g194: GeomPoint X=148.522 Y=167.476 Z=0
    g195: GeomPoint X=133.022 Y=151.976 Z=0
    g196: ArcOfCircle CenterX=128.185 CenterY=166.226 CenterZ=0 NormalX=0 NormalY=0 NormalZ=1 AngleXU=0 Radius=1.25 StartAngle=6.1e-15 EndAngle=1.5708
    g197: LineSegment StartX=129.435 StartY=166.226 StartZ=0 EndX=129.435 EndY=153.226 EndZ=0
    g198: ArcOfCircle CenterX=128.185 CenterY=153.226 CenterZ=0 NormalX=0 NormalY=0 NormalZ=1 AngleXU=0 Radius=1.25 StartAngle=4.71239 EndAngle=6.28319
    g199: LineSegment StartX=128.185 StartY=151.976 StartZ=0 EndX=115.185 EndY=151.976 EndZ=0
    g200: ArcOfCircle CenterX=115.185 CenterY=153.226 CenterZ=0 NormalX=0 NormalY=0 NormalZ=1 AngleXU=0 Radius=1.25 StartAngle=3.14159 EndAngle=4.71239
    g201: LineSegment StartX=113.935 StartY=153.226 StartZ=0 EndX=113.935 EndY=166.226 EndZ=0
    g202: ArcOfCircle CenterX=115.185 CenterY=166.226 CenterZ=0 NormalX=0 NormalY=0 NormalZ=1 AngleXU=0 Radius=1.25 StartAngle=1.5708 EndAngle=3.14159
    g203: LineSegment StartX=115.185 StartY=167.476 StartZ=0 EndX=128.185 EndY=167.476 EndZ=0
    g204: GeomPoint X=129.435 Y=167.476 Z=0
    g205: GeomPoint X=113.935 Y=151.976 Z=0
    g206: ArcOfCircle CenterX=109.098 CenterY=166.226 CenterZ=0 NormalX=0 NormalY=0 NormalZ=1 AngleXU=0 Radius=1.25 StartAngle=-5.3e-15 EndAngle=1.5708
    g207: LineSegment StartX=110.348 StartY=166.226 StartZ=0 EndX=110.348 EndY=153.226 EndZ=0
    g208: ArcOfCircle CenterX=109.098 CenterY=153.226 CenterZ=0 NormalX=0 NormalY=0 NormalZ=1 AngleXU=0 Radius=1.25 StartAngle=4.71239 EndAngle=6.28319
    g209: LineSegment StartX=109.098 StartY=151.976 StartZ=0 EndX=96.0977 EndY=151.976 EndZ=0
    g210: ArcOfCircle CenterX=96.0977 CenterY=153.226 CenterZ=0 NormalX=0 NormalY=0 NormalZ=1 AngleXU=0 Radius=1.25 StartAngle=3.14159 EndAngle=4.71239
    g211: LineSegment StartX=94.8477 StartY=153.226 StartZ=0 EndX=94.8477 EndY=166.226 EndZ=0
    g212: ArcOfCircle CenterX=96.0977 CenterY=166.226 CenterZ=0 NormalX=0 NormalY=0 NormalZ=1 AngleXU=0 Radius=1.25 StartAngle=1.5708 EndAngle=3.14159
    g213: LineSegment StartX=96.0977 StartY=167.476 StartZ=0 EndX=109.098 EndY=167.476 EndZ=0
    g214: GeomPoint X=110.348 Y=167.476 Z=0
    g215: GeomPoint X=94.8477 Y=151.976 Z=0
    g216: ArcOfCircle CenterX=90.0108 CenterY=166.226 CenterZ=0 NormalX=0 NormalY=0 NormalZ=1 AngleXU=0 Radius=1.25 StartAngle=-3.6e-15 EndAngle=1.5708
    g217: LineSegment StartX=91.2608 StartY=166.226 StartZ=0 EndX=91.2608 EndY=153.226 EndZ=0
    g218: ArcOfCircle CenterX=90.0108 CenterY=153.226 CenterZ=0 NormalX=0 NormalY=0 NormalZ=1 AngleXU=0 Radius=1.25 StartAngle=4.71239 EndAngle=6.28319
    g219: LineSegment StartX=90.0108 StartY=151.976 StartZ=0 EndX=77.0108 EndY=151.976 EndZ=0
    g220: ArcOfCircle CenterX=77.0108 CenterY=153.226 CenterZ=0 NormalX=0 NormalY=0 NormalZ=1 AngleXU=0 Radius=1.25 StartAngle=3.14159 EndAngle=4.71239
    g221: LineSegment StartX=75.7608 StartY=153.226 StartZ=0 EndX=75.7608 EndY=166.226 EndZ=0
    g222: ArcOfCircle CenterX=77.0108 CenterY=166.226 CenterZ=0 NormalX=0 NormalY=0 NormalZ=1 AngleXU=0 Radius=1.25 StartAngle=1.5708 EndAngle=3.14159
    g223: LineSegment StartX=77.0108 StartY=167.476 StartZ=0 EndX=90.0108 EndY=167.476 EndZ=0
    g224: GeomPoint X=91.2608 Y=167.476 Z=0
    g225: GeomPoint X=75.7608 Y=151.976 Z=0
    g226: ArcOfCircle CenterX=70.9238 CenterY=166.226 CenterZ=0 NormalX=0 NormalY=0 NormalZ=1 AngleXU=0 Radius=1.25 StartAngle=-1.8e-15 EndAngle=1.5708
    g227: LineSegment StartX=72.1738 StartY=166.226 StartZ=0 EndX=72.1738 EndY=153.226 EndZ=0
    g228: ArcOfCircle CenterX=70.9238 CenterY=153.226 CenterZ=0 NormalX=0 NormalY=0 NormalZ=1 AngleXU=0 Radius=1.25 StartAngle=4.71239 EndAngle=6.28319
    g229: LineSegment StartX=70.9238 StartY=151.976 StartZ=0 EndX=57.9238 EndY=151.976 EndZ=0
    g230: ArcOfCircle CenterX=57.9238 CenterY=153.226 CenterZ=0 NormalX=0 NormalY=0 NormalZ=1 AngleXU=0 Radius=1.25 StartAngle=3.14159 EndAngle=4.71239
    g231: LineSegment StartX=56.6738 StartY=153.226 StartZ=0 EndX=56.6738 EndY=166.226 EndZ=0
    g232: ArcOfCircle CenterX=57.9238 CenterY=166.226 CenterZ=0 NormalX=0 NormalY=0 NormalZ=1 AngleXU=0 Radius=1.25 StartAngle=1.5708 EndAngle=3.14159
    g233: LineSegment StartX=57.9238 StartY=167.476 StartZ=0 EndX=70.9238 EndY=167.476 EndZ=0
    g234: GeomPoint X=72.1738 Y=167.476 Z=0
    g235: GeomPoint X=56.6738 Y=151.976 Z=0
    g236: ArcOfCircle CenterX=51.8369 CenterY=166.226 CenterZ=0 NormalX=0 NormalY=0 NormalZ=1 AngleXU=0 Radius=1.25 StartAngle=-1.07e-14 EndAngle=1.5708
    g237: LineSegment StartX=53.0869 StartY=166.226 StartZ=0 EndX=53.0869 EndY=153.226 EndZ=0
    g238: ArcOfCircle CenterX=51.8369 CenterY=153.226 CenterZ=0 NormalX=0 NormalY=0 NormalZ=1 AngleXU=0 Radius=1.25 StartAngle=4.71239 EndAngle=6.28319
    g239: LineSegment StartX=51.8369 StartY=151.976 StartZ=0 EndX=38.8369 EndY=151.976 EndZ=0
    g240: ArcOfCircle CenterX=38.8369 CenterY=153.226 CenterZ=0 NormalX=0 NormalY=0 NormalZ=1 AngleXU=0 Radius=1.25 StartAngle=3.14159 EndAngle=4.71239
    g241: LineSegment StartX=37.5869 StartY=153.226 StartZ=0 EndX=37.5869 EndY=166.226 EndZ=0
    g242: ArcOfCircle CenterX=38.8369 CenterY=166.226 CenterZ=0 NormalX=0 NormalY=0 NormalZ=1 AngleXU=0 Radius=1.25 StartAngle=1.5708 EndAngle=3.14159
    g243: LineSegment StartX=38.8369 StartY=167.476 StartZ=0 EndX=51.8369 EndY=167.476 EndZ=0
    g244: GeomPoint X=53.0869 Y=167.476 Z=0
    g245: GeomPoint X=37.5869 Y=151.976 Z=0
    g246: LineSegment StartX=34 StartY=166.226 StartZ=0 EndX=37.5869 EndY=166.226 EndZ=0
    g247: LineSegment StartX=53.0869 StartY=166.226 StartZ=0 EndX=56.6738 EndY=166.226 EndZ=0
    g248: LineSegment StartX=72.1738 StartY=166.226 StartZ=0 EndX=75.7608 EndY=166.226 EndZ=0
    g249: LineSegment StartX=91.2608 StartY=166.226 StartZ=0 EndX=94.8477 EndY=166.226 EndZ=0
    g250: LineSegment StartX=110.348 StartY=166.226 StartZ=0 EndX=113.935 EndY=166.226 EndZ=0
    g251: LineSegment StartX=129.435 StartY=166.226 StartZ=0 EndX=133.022 EndY=166.226 EndZ=0
    g252: LineSegment StartX=152.108 StartY=166.226 StartZ=0 EndX=148.522 EndY=166.226 EndZ=0
    g253: LineSegment StartX=167.608 StartY=166.226 StartZ=0 EndX=171.195 EndY=166.226 EndZ=0
    g254: LineSegment StartX=186.695 StartY=166.226 StartZ=0 EndX=190.282 EndY=166.226 EndZ=0
    g255: LineSegment StartX=205.782 StartY=166.226 StartZ=0 EndX=209.369 EndY=166.226 EndZ=0
    g256: LineSegment StartX=224.869 StartY=166.226 StartZ=0 EndX=228.456 EndY=166.226 EndZ=0
    g257: LineSegment StartX=247.543 StartY=166.226 StartZ=0 EndX=243.956 EndY=166.226 EndZ=0
    g258: LineSegment StartX=263.043 StartY=166.226 StartZ=0 EndX=266.63 EndY=166.226 EndZ=0
  constraints (610):
    c: Coincident(g0,g-5)
    c: Coincident(g0,g-4)
    c: Coincident(g1,g-3)
    c: Coincident(g1,g-6)
    c: Tangent(g2,g3) = 1.5708
    c: Tangent(g3,g4) = 1.5708
    c: Tangent(g4,g5) = 1.5708
    c: Tangent(g5,g6) = 1.5708
    c: Tangent(g6,g7) = 1.5708
    c: Tangent(g7,g8) = 1.5708
    c: Tangent(g8,g9) = 1.5708
    c: Tangent(g9,g2) = 1.5708
    c: Horizontal(g5)
    c: Horizontal(g9)
    c: Vertical(g3)
    c: Vertical(g7)
    c: Equal(g2,g4)
    c: Equal(g4,g6)
    c: Equal(g6,g8)
    c: PointOnObject(g10,g3)
    c: PointOnObject(g10,g9)
    c: PointOnObject(g11,g5)
    c: PointOnObject(g11,g7)
    c: PointOnObject(g10,g1)
    c: PointOnObject(g11,g0)
    c: Tangent(g12,g13) = 1.5708
    c: Tangent(g13,g14) = 1.5708
    c: Tangent(g14,g15) = 1.5708
    c: Tangent(g15,g16) = 1.5708
    c: Tangent(g16,g17) = 1.5708
    c: Tangent(g17,g18) = 1.5708
    c: Tangent(g18,g19) = 1.5708
    c: Tangent(g19,g12) = 1.5708
    c: Horizontal(g13)
    c: Horizontal(g17)
    c: Vertical(g15)
    c: Vertical(g19)
    c: Equal(g12,g14)
    c: Equal(g14,g16)
    c: Equal(g16,g18)
    c: PointOnObject(g20,g13)
    c: PointOnObject(g20,g19)
    c: PointOnObject(g21,g15)
    c: PointOnObject(g21,g17)
    c: PointOnObject(g20,g0)
    c: PointOnObject(g21,g1)
    c: Tangent(g22,g23) = 1.5708
    c: Tangent(g23,g24) = 1.5708
    c: Tangent(g24,g25) = 1.5708
    c: Tangent(g25,g26) = 1.5708
    c: Tangent(g26,g27) = 1.5708
    c: Tangent(g27,g28) = 1.5708
    c: Tangent(g28,g29) = 1.5708
    c: Tangent(g29,g22) = 1.5708
    c: Horizontal(g23)
    c: Horizontal(g27)
    c: Vertical(g25)
    c: Vertical(g29)
    c: Equal(g22,g24)
    c: Equal(g24,g26)
    c: Equal(g26,g28)
    c: PointOnObject(g30,g23)
    c: PointOnObject(g30,g29)
    c: PointOnObject(g31,g25)
    c: PointOnObject(g31,g27)
    c: PointOnObject(g30,g0)
    c: PointOnObject(g31,g1)
    c: Tangent(g32,g33) = 1.5708
    c: Tangent(g33,g34) = 1.5708
    c: Tangent(g34,g35) = 1.5708
    c: Tangent(g35,g36) = 1.5708
    c: Tangent(g36,g37) = 1.5708
    c: Tangent(g37,g38) = 1.5708
    c: Tangent(g38,g39) = 1.5708
    c: Tangent(g39,g32) = 1.5708
    c: Horizontal(g35)
    c: Horizontal(g39)
    c: Vertical(g33)
    c: Vertical(g37)
    c: Equal(g32,g34)
    c: Equal(g34,g36)
    c: Equal(g36,g38)
    c: PointOnObject(g40,g33)
    c: PointOnObject(g40,g39)
    c: PointOnObject(g41,g35)
    c: PointOnObject(g41,g37)
    c: PointOnObject(g40,g1)
    c: PointOnObject(g41,g0)
    c: Tangent(g42,g43) = 1.5708
    c: Tangent(g43,g44) = 1.5708
    c: Tangent(g44,g45) = 1.5708
    c: Tangent(g45,g46) = 1.5708
    c: Tangent(g46,g47) = 1.5708
    c: Tangent(g47,g48) = 1.5708
    c: Tangent(g48,g49) = 1.5708
    c: Tangent(g49,g42) = 1.5708
    c: Horizontal(g43)
    c: Horizontal(g47)
    c: Vertical(g45)
    c: Vertical(g49)
    c: Equal(g42,g44)
    c: Equal(g44,g46)
    c: Equal(g46,g48)
    c: PointOnObject(g50,g43)
    c: PointOnObject(g50,g49)
    c: PointOnObject(g51,g45)
    c: PointOnObject(g51,g47)
    c: PointOnObject(g50,g0)
    c: PointOnObject(g51,g1)
    c: Tangent(g52,g53) = 1.5708
    c: Tangent(g53,g54) = 1.5708
    c: Tangent(g54,g55) = 1.5708
    c: Tangent(g55,g56) = 1.5708
    c: Tangent(g56,g57) = 1.5708
    c: Tangent(g57,g58) = 1.5708
    c: Tangent(g58,g59) = 1.5708
    c: Tangent(g59,g52) = 1.5708
    c: Horizontal(g55)
    c: Horizontal(g59)
    c: Vertical(g53)
    c: Vertical(g57)
    c: Equal(g52,g54)
    c: Equal(g54,g56)
    c: Equal(g56,g58)
    c: PointOnObject(g60,g53)
    c: PointOnObject(g60,g59)
    c: PointOnObject(g61,g55)
    c: PointOnObject(g61,g57)
    c: PointOnObject(g60,g1)
    c: PointOnObject(g61,g0)
    c: Tangent(g62,g63) = 1.5708
    c: Tangent(g63,g64) = 1.5708
    c: Tangent(g64,g65) = 1.5708
    c: Tangent(g65,g66) = 1.5708
    c: Tangent(g66,g67) = 1.5708
    c: Tangent(g67,g68) = 1.5708
    c: Tangent(g68,g69) = 1.5708
    c: Tangent(g69,g62) = 1.5708
    c: Horizontal(g63)
    c: Horizontal(g67)
    c: Vertical(g65)
    c: Vertical(g69)
    c: Equal(g62,g64)
    c: Equal(g64,g66)
    c: Equal(g66,g68)
    c: PointOnObject(g70,g63)
    c: PointOnObject(g70,g69)
    c: PointOnObject(g71,g65)
    c: PointOnObject(g71,g67)
    c: PointOnObject(g70,g0)
    c: PointOnObject(g71,g1)
    c: Tangent(g72,g73) = 1.5708
    c: Tangent(g73,g74) = 1.5708
    c: Tangent(g74,g75) = 1.5708
    c: Tangent(g75,g76) = 1.5708
    c: Tangent(g76,g77) = 1.5708
    c: Tangent(g77,g78) = 1.5708
    c: Tangent(g78,g79) = 1.5708
    c: Tangent(g79,g72) = 1.5708
    c: Horizontal(g75)
    c: Horizontal(g79)
    c: Vertical(g73)
    c: Vertical(g77)
    c: Equal(g72,g74)
    c: Equal(g74,g76)
    c: Equal(g76,g78)
    c: PointOnObject(g80,g73)
    c: PointOnObject(g80,g79)
    c: PointOnObject(g81,g75)
    c: PointOnObject(g81,g77)
    c: PointOnObject(g80,g1)
    c: PointOnObject(g81,g0)
    c: Tangent(g82,g83) = 1.5708
    c: Tangent(g83,g84) = 1.5708
    c: Tangent(g84,g85) = 1.5708
    c: Tangent(g85,g86) = 1.5708
    c: Tangent(g86,g87) = 1.5708
    c: Tangent(g87,g88) = 1.5708
    c: Tangent(g88,g89) = 1.5708
    c: Tangent(g89,g82) = 1.5708
    c: Horizontal(g85)
    c: Horizontal(g89)
    c: Vertical(g83)
    c: Vertical(g87)
    c: Equal(g82,g84)
    c: Equal(g84,g86)
    c: Equal(g86,g88)
    c: PointOnObject(g90,g83)
    c: PointOnObject(g90,g89)
    c: PointOnObject(g91,g85)
    c: PointOnObject(g91,g87)
    c: PointOnObject(g90,g1)
    c: PointOnObject(g91,g0)
    c: Tangent(g92,g93) = 1.5708
    c: Tangent(g93,g94) = 1.5708
    c: Tangent(g94,g95) = 1.5708
    c: Tangent(g95,g96) = 1.5708
    c: Tangent(g96,g97) = 1.5708
    c: Tangent(g97,g98) = 1.5708
    c: Tangent(g98,g99) = 1.5708
    c: Tangent(g99,g92) = 1.5708
    c: Horizontal(g95)
    c: Horizontal(g99)
    c: Vertical(g93)
    c: Vertical(g97)
    c: Equal(g92,g94)
    c: Equal(g94,g96)
    c: Equal(g96,g98)
    c: PointOnObject(g100,g93)
    c: PointOnObject(g100,g99)
    c: PointOnObject(g101,g95)
    c: PointOnObject(g101,g97)
    c: PointOnObject(g100,g1)
    c: PointOnObject(g101,g0)
    c: Tangent(g102,g103) = 1.5708
    c: Tangent(g103,g104) = 1.5708
    c: Tangent(g104,g105) = 1.5708
    c: Tangent(g105,g106) = 1.5708
    c: Tangent(g106,g107) = 1.5708
    c: Tangent(g107,g108) = 1.5708
    c: Tangent(g108,g109) = 1.5708
    c: Tangent(g109,g102) = 1.5708
    c: Horizontal(g103)
    c: Horizontal(g107)
    c: Vertical(g105)
    c: Vertical(g109)
    c: Equal(g102,g104)
    c: Equal(g104,g106)
    c: Equal(g106,g108)
    c: PointOnObject(g110,g103)
    c: PointOnObject(g110,g109)
    c: PointOnObject(g111,g105)
    c: PointOnObject(g111,g107)
    c: PointOnObject(g110,g0)
    c: PointOnObject(g111,g1)
    c: Coincident(g112,g-3)
    c: Coincident(g112,g105)
    c: Coincident(g113,g108)
    c: Coincident(g113,g97)
    c: Horizontal(g113)
    c: Coincident(g114,g92)
    c: Coincident(g114,g87)
    c: Horizontal(g114)
    c: Coincident(g115,g82)
    c: Coincident(g115,g77)
    c: Coincident(g116,g72)
    c: Coincident(g116,g65)
    c: Coincident(g117,g68)
    c: Coincident(g117,g57)
    c: Coincident(g118,g52)
    c: Coincident(g118,g45)
    c: Coincident(g119,g48)
    c: Coincident(g119,g37)
    c: Coincident(g120,g32)
    c: Coincident(g120,g25)
    c: Coincident(g121,g28)
    c: Coincident(g121,g15)
    c: Horizontal(g121)
    c: Coincident(g122,g18)
    c: Coincident(g122,g7)
    c: Horizontal(g122)
    c: Coincident(g123,g2)
    c: Coincident(g123,g-6)
    c: Equal(g-6,g2)
    c: Equal(g26,g32)
    c: Equal(g38,g48)
    c: Equal(g52,g46)
    c: Equal(g58,g68)
    c: Equal(g66,g72)
    c: Equal(g78,g82)
    c: Equal(g107,g99)
    c: Equal(g99,g89)
    c: Equal(g89,g79)
    c: Equal(g79,g67)
    c: Equal(g67,g59)
    c: Equal(g59,g47)
    c: Equal(g47,g39)
    c: Equal(g39,g27)
    c: Equal(g27,g17)
    c: Equal(g17,g9)
    c: Equal(g123,g122)
    c: Equal(g122,g121)
    c: Equal(g120,g121)
    c: Equal(g120,g119)
    c: Equal(g119,g118)
    c: Equal(g118,g117)
    c: Equal(g117,g116)
    c: Equal(g116,g115)
    c: Equal(g115,g114)
    c: Equal(g114,g113)
    c: Equal(g112,g113)
    c: Equal(g107,g105)
    c: Coincident(g124,g-9)
    c: Coincident(g124,g-7)
    c: Coincident(g125,g-8)
    c: Coincident(g125,g-10)
    c: Tangent(g126,g127) = 1.5708
    c: Tangent(g127,g128) = 1.5708
    c: Tangent(g128,g129) = 1.5708
    c: Tangent(g129,g130) = 1.5708
    c: Tangent(g130,g131) = 1.5708
    c: Tangent(g131,g132) = 1.5708
    c: Tangent(g132,g133) = 1.5708
    c: Tangent(g133,g126) = 1.5708
    c: Horizontal(g129)
    c: Horizontal(g133)
    c: Vertical(g127)
    c: Vertical(g131)
    c: Equal(g126,g128)
    c: Equal(g128,g130)
    c: Equal(g130,g132)
    c: PointOnObject(g134,g127)
    c: PointOnObject(g134,g133)
    c: PointOnObject(g135,g129)
    c: PointOnObject(g135,g131)
    c: PointOnObject(g134,g124)
    c: PointOnObject(g135,g125)
    c: Tangent(g136,g137) = 1.5708
    c: Tangent(g137,g138) = 1.5708
    c: Tangent(g138,g139) = 1.5708
    c: Tangent(g139,g140) = 1.5708
    c: Tangent(g140,g141) = 1.5708
    c: Tangent(g141,g142) = 1.5708
    c: Tangent(g142,g143) = 1.5708
    c: Tangent(g143,g136) = 1.5708
    c: Horizontal(g139)
    c: Horizontal(g143)
    c: Vertical(g137)
    c: Vertical(g141)
    c: Equal(g136,g138)
    c: Equal(g138,g140)
    c: Equal(g140,g142)
    c: PointOnObject(g144,g137)
    c: PointOnObject(g144,g143)
    c: PointOnObject(g145,g139)
    c: PointOnObject(g145,g141)
    c: PointOnObject(g144,g124)
    c: PointOnObject(g145,g125)
    c: Tangent(g146,g147) = 1.5708
    c: Tangent(g147,g148) = 1.5708
    c: Tangent(g148,g149) = 1.5708
    c: Tangent(g149,g150) = 1.5708
    c: Tangent(g150,g151) = 1.5708
    c: Tangent(g151,g152) = 1.5708
    c: Tangent(g152,g153) = 1.5708
    c: Tangent(g153,g146) = 1.5708
    c: Horizontal(g149)
    c: Horizontal(g153)
    c: Vertical(g147)
    c: Vertical(g151)
    c: Equal(g146,g148)
    c: Equal(g148,g150)
    c: Equal(g150,g152)
    c: PointOnObject(g154,g147)
    c: PointOnObject(g154,g153)
    c: PointOnObject(g155,g149)
    c: PointOnObject(g155,g151)
    c: PointOnObject(g154,g124)
    c: PointOnObject(g155,g125)
    c: Tangent(g156,g157) = 1.5708
    c: Tangent(g157,g158) = 1.5708
    c: Tangent(g158,g159) = 1.5708
    c: Tangent(g159,g160) = 1.5708
    c: Tangent(g160,g161) = 1.5708
    c: Tangent(g161,g162) = 1.5708
    c: Tangent(g162,g163) = 1.5708
    c: Tangent(g163,g156) = 1.5708
    c: Horizontal(g159)
    c: Horizontal(g163)
    c: Vertical(g157)
    c: Vertical(g161)
    c: Equal(g156,g158)
    c: Equal(g158,g160)
    c: Equal(g160,g162)
    c: PointOnObject(g164,g157)
    c: PointOnObject(g164,g163)
    c: PointOnObject(g165,g159)
    c: PointOnObject(g165,g161)
    c: PointOnObject(g164,g124)
    c: PointOnObject(g165,g125)
    c: Tangent(g166,g167) = 1.5708
    c: Tangent(g167,g168) = 1.5708
    c: Tangent(g168,g169) = 1.5708
    c: Tangent(g169,g170) = 1.5708
    c: Tangent(g170,g171) = 1.5708
    c: Tangent(g171,g172) = 1.5708
    c: Tangent(g172,g173) = 1.5708
    c: Tangent(g173,g166) = 1.5708
    c: Horizontal(g169)
    c: Horizontal(g173)
    c: Vertical(g167)
    c: Vertical(g171)
    c: Equal(g166,g168)
    c: Equal(g168,g170)
    c: Equal(g170,g172)
    c: PointOnObject(g174,g167)
    c: PointOnObject(g174,g173)
    c: PointOnObject(g175,g169)
    c: PointOnObject(g175,g171)
    c: PointOnObject(g174,g124)
    c: PointOnObject(g175,g125)
    c: Tangent(g176,g177) = 1.5708
    c: Tangent(g177,g178) = 1.5708
    c: Tangent(g178,g179) = 1.5708
    c: Tangent(g179,g180) = 1.5708
    c: Tangent(g180,g181) = 1.5708
    c: Tangent(g181,g182) = 1.5708
    c: Tangent(g182,g183) = 1.5708
    c: Tangent(g183,g176) = 1.5708
    c: Horizontal(g179)
    c: Horizontal(g183)
    c: Vertical(g177)
    c: Vertical(g181)
    c: Equal(g176,g178)
    c: Equal(g178,g180)
    c: Equal(g180,g182)
    c: PointOnObject(g184,g177)
    c: PointOnObject(g184,g183)
    c: PointOnObject(g185,g179)
    c: PointOnObject(g185,g181)
    c: PointOnObject(g184,g124)
    c: PointOnObject(g185,g125)
    c: Tangent(g186,g187) = 1.5708
    c: Tangent(g187,g188) = 1.5708
    c: Tangent(g188,g189) = 1.5708
    c: Tangent(g189,g190) = 1.5708
    c: Tangent(g190,g191) = 1.5708
    c: Tangent(g191,g192) = 1.5708
    c: Tangent(g192,g193) = 1.5708
    c: Tangent(g193,g186) = 1.5708
    c: Horizontal(g189)
    c: Horizontal(g193)
    c: Vertical(g187)
    c: Vertical(g191)
    c: Equal(g186,g188)
    c: Equal(g188,g190)
    c: Equal(g190,g192)
    c: PointOnObject(g194,g187)
    c: PointOnObject(g194,g193)
    c: PointOnObject(g195,g189)
    c: PointOnObject(g195,g191)
    c: PointOnObject(g194,g124)
    c: PointOnObject(g195,g125)
    c: Tangent(g196,g197) = 1.5708
    c: Tangent(g197,g198) = 1.5708
    c: Tangent(g198,g199) = 1.5708
    c: Tangent(g199,g200) = 1.5708
    c: Tangent(g200,g201) = 1.5708
    c: Tangent(g201,g202) = 1.5708
    c: Tangent(g202,g203) = 1.5708
    c: Tangent(g203,g196) = 1.5708
    c: Horizontal(g199)
    c: Horizontal(g203)
    c: Vertical(g197)
    c: Vertical(g201)
    c: Equal(g196,g198)
    c: Equal(g198,g200)
    c: Equal(g200,g202)
    c: PointOnObject(g204,g197)
    c: PointOnObject(g204,g203)
    c: PointOnObject(g205,g199)
    c: PointOnObject(g205,g201)
    c: PointOnObject(g204,g124)
    c: PointOnObject(g205,g125)
    c: Tangent(g206,g207) = 1.5708
    c: Tangent(g207,g208) = 1.5708
    c: Tangent(g208,g209) = 1.5708
    c: Tangent(g209,g210) = 1.5708
    c: Tangent(g210,g211) = 1.5708
    c: Tangent(g211,g212) = 1.5708
    c: Tangent(g212,g213) = 1.5708
    c: Tangent(g213,g206) = 1.5708
    c: Horizontal(g209)
    c: Horizontal(g213)
    c: Vertical(g207)
    c: Vertical(g211)
    c: Equal(g206,g208)
    c: Equal(g208,g210)
    c: Equal(g210,g212)
    c: PointOnObject(g214,g207)
    c: PointOnObject(g214,g213)
    c: PointOnObject(g215,g209)
    c: PointOnObject(g215,g211)
    c: PointOnObject(g214,g124)
    c: PointOnObject(g215,g125)
    c: Tangent(g216,g217) = 1.5708
    c: Tangent(g217,g218) = 1.5708
    c: Tangent(g218,g219) = 1.5708
    c: Tangent(g219,g220) = 1.5708
    c: Tangent(g220,g221) = 1.5708
    c: Tangent(g221,g222) = 1.5708
    c: Tangent(g222,g223) = 1.5708
    c: Tangent(g223,g216) = 1.5708
    c: Horizontal(g219)
    c: Horizontal(g223)
    c: Vertical(g217)
    c: Vertical(g221)
    c: Equal(g216,g218)
    c: Equal(g218,g220)
    c: Equal(g220,g222)
    c: PointOnObject(g224,g217)
    c: PointOnObject(g224,g223)
    c: PointOnObject(g225,g219)
    c: PointOnObject(g225,g221)
    c: PointOnObject(g224,g124)
    c: PointOnObject(g225,g125)
    c: Tangent(g226,g227) = 1.5708
    c: Tangent(g227,g228) = 1.5708
    c: Tangent(g228,g229) = 1.5708
    c: Tangent(g229,g230) = 1.5708
    c: Tangent(g230,g231) = 1.5708
    c: Tangent(g231,g232) = 1.5708
    c: Tangent(g232,g233) = 1.5708
    c: Tangent(g233,g226) = 1.5708
    c: Horizontal(g229)
    c: Horizontal(g233)
    c: Vertical(g227)
    c: Vertical(g231)
    c: Equal(g226,g228)
    c: Equal(g228,g230)
    c: Equal(g230,g232)
    c: PointOnObject(g234,g227)
    c: PointOnObject(g234,g233)
    c: PointOnObject(g235,g229)
    c: PointOnObject(g235,g231)
    c: PointOnObject(g234,g124)
    c: PointOnObject(g235,g125)
    c: Tangent(g236,g237) = 1.5708
    c: Tangent(g237,g238) = 1.5708
    c: Tangent(g238,g239) = 1.5708
    c: Tangent(g239,g240) = 1.5708
    c: Tangent(g240,g241) = 1.5708
    c: Tangent(g241,g242) = 1.5708
    c: Tangent(g242,g243) = 1.5708
    c: Tangent(g243,g236) = 1.5708
    c: Horizontal(g239)
    c: Horizontal(g243)
    c: Vertical(g237)
    c: Vertical(g241)
    c: Equal(g236,g238)
    c: Equal(g238,g240)
    c: Equal(g240,g242)
    c: PointOnObject(g244,g237)
    c: PointOnObject(g244,g243)
    c: PointOnObject(g245,g239)
    c: PointOnObject(g245,g241)
    c: PointOnObject(g244,g124)
    c: PointOnObject(g245,g125)
    c: Coincident(g246,g-7)
    c: Coincident(g246,g241)
    c: Coincident(g247,g236)
    c: Coincident(g247,g231)
    c: Horizontal(g247)
    c: Coincident(g248,g226)
    c: Coincident(g248,g221)
    c: Horizontal(g248)
    c: Coincident(g249,g216)
    c: Coincident(g249,g211)
    c: Horizontal(g249)
    c: Coincident(g250,g206)
    c: Coincident(g250,g201)
    c: Horizontal(g250)
    c: Coincident(g251,g196)
    c: Coincident(g251,g191)
    c: Horizontal(g251)
    c: Coincident(g252,g181)
    c: Coincident(g252,g186)
    c: Horizontal(g252)
    c: Coincident(g253,g176)
    c: Coincident(g253,g171)
    c: Coincident(g254,g166)
    c: Coincident(g254,g161)
    c: Horizontal(g254)
    c: Coincident(g255,g156)
    c: Coincident(g255,g151)
    c: Horizontal(g255)
    c: Coincident(g256,g146)
    c: Coincident(g256,g141)
    c: Horizontal(g256)
    c: Horizontal(g253)
    c: Coincident(g257,g131)
    c: Coincident(g257,g136)
    c: Coincident(g258,g126)
    c: Coincident(g258,g-9)
    c: Horizontal(g258)
    c: Horizontal(g257)
    c: Equal(g258,g257)
    c: Equal(g257,g256)
    c: Equal(g256,g255)
    c: Equal(g255,g254)
    c: Equal(g254,g253)
    c: Equal(g253,g252)
    c: Equal(g252,g251)
    c: Equal(g251,g250)
    c: Equal(g250,g249)
    c: Equal(g249,g248)
    c: Equal(g248,g247)
    c: Equal(g247,g246)
    c: Equal(g243,g233)
    c: Equal(g233,g223)
    c: Equal(g223,g213)
    c: Equal(g213,g203)
    c: Equal(g193,g203)
    c: Equal(g193,g183)
    c: Equal(g183,g173)
    c: Equal(g173,g163)
    c: Equal(g163,g153)
    c: Equal(g153,g143)
    c: Equal(g143,g133)
    c: Equal(g133,g127)
FEATURE [Sketcher::SketchObject] Sketch012
  FullyConstrained = true
  MapMode = 5
  Support = -> [XY_Plane]
  sketch-geometry (889):
    g0: ArcOfCircle CenterX=7 CenterY=7 CenterZ=0 NormalX=0 NormalY=0 NormalZ=1 AngleXU=0 Radius=7 StartAngle=3.14159 EndAngle=4.71239
    g1: LineSegment StartX=0 StartY=7 StartZ=0 EndX=0 EndY=221.98 EndZ=0
    g2: ArcOfCircle CenterX=7 CenterY=221.98 CenterZ=0 NormalX=0 NormalY=0 NormalZ=1 AngleXU=0 Radius=7 StartAngle=1.5708 EndAngle=3.14159
    g3: LineSegment StartX=7 StartY=228.98 StartZ=0 EndX=18.25 EndY=228.98 EndZ=0
    g4: ArcOfCircle CenterX=289.63 CenterY=221.98 CenterZ=0 NormalX=0 NormalY=0 NormalZ=1 AngleXU=0 Radius=7 StartAngle=4e-16 EndAngle=1.5708
    g5: LineSegment StartX=296.63 StartY=221.98 StartZ=0 EndX=296.63 EndY=7 EndZ=0
    g6: ArcOfCircle CenterX=289.63 CenterY=7 CenterZ=0 NormalX=0 NormalY=0 NormalZ=1 AngleXU=0 Radius=7 StartAngle=4.71239 EndAngle=6.28319
    g7: LineSegment StartX=289.63 StartY=0 StartZ=0 EndX=7 EndY=0 EndZ=0
    g8: GeomPoint X=0 Y=0 Z=0
    g9: GeomPoint X=296.63 Y=228.98 Z=0
    g10: LineSegment StartX=278.38 StartY=216.23 StartZ=0 EndX=18.25 EndY=216.23 EndZ=0
    g11: LineSegment StartX=278.38 StartY=228.98 StartZ=0 EndX=278.38 EndY=216.23 EndZ=0
    g12: LineSegment StartX=18.25 StartY=216.23 StartZ=0 EndX=18.25 EndY=228.98 EndZ=0
    g13: LineSegment StartX=278.38 StartY=228.98 StartZ=0 EndX=289.63 EndY=228.98 EndZ=0
    g14: ArcOfCircle CenterX=202.815 CenterY=83.5 CenterZ=0 NormalX=0 NormalY=0 NormalZ=1 AngleXU=0 Radius=3 StartAngle=-9e-16 EndAngle=1.5708
    g15: LineSegment StartX=205.815 StartY=83.5 StartZ=0 EndX=205.815 EndY=12.5 EndZ=0
    g16: ArcOfCircle CenterX=202.815 CenterY=12.5 CenterZ=0 NormalX=0 NormalY=0 NormalZ=1 AngleXU=0 Radius=3 StartAngle=4.71239 EndAngle=6.28319
    g17: LineSegment StartX=202.815 StartY=9.5 StartZ=0 EndX=93.815 EndY=9.5 EndZ=0
    g18: ArcOfCircle CenterX=93.815 CenterY=12.5 CenterZ=0 NormalX=0 NormalY=0 NormalZ=1 AngleXU=0 Radius=3 StartAngle=3.14159 EndAngle=4.71239
    g19: LineSegment StartX=90.815 StartY=12.5 StartZ=0 EndX=90.815 EndY=83.5 EndZ=0
    g20: ArcOfCircle CenterX=93.815 CenterY=83.5 CenterZ=0 NormalX=0 NormalY=0 NormalZ=1 AngleXU=0 Radius=3 StartAngle=1.5708 EndAngle=3.14159
    g21: LineSegment StartX=93.815 StartY=86.5 StartZ=0 EndX=202.815 EndY=86.5 EndZ=0
    g22: GeomPoint X=205.815 Y=86.5 Z=0
    g23: GeomPoint X=90.815 Y=9.5 Z=0
    g24: LineSegment StartX=205.815 StartY=83.5 StartZ=0 EndX=296.63 EndY=83.5 EndZ=0
    g25: LineSegment StartX=90.815 StartY=83.5 StartZ=0 EndX=0 EndY=83.5 EndZ=0
    g26: LineSegment StartX=9.45 StartY=199.98 StartZ=0 EndX=287.18 EndY=199.98 EndZ=0
    g27: LineSegment StartX=287.18 StartY=199.98 StartZ=0 EndX=287.18 EndY=94.8199 EndZ=0
    g28: LineSegment StartX=287.18 StartY=94.8199 StartZ=0 EndX=9.45 EndY=94.8199 EndZ=0
    g29: LineSegment StartX=9.45 StartY=94.8199 StartZ=0 EndX=9.45 EndY=199.98 EndZ=0
    g30: LineSegment StartX=287.18 StartY=199.98 StartZ=0 EndX=296.63 EndY=199.98 EndZ=0
    g31: LineSegment StartX=9.45 StartY=199.98 StartZ=0 EndX=0 EndY=199.98 EndZ=0
    g32: LineSegment StartX=9.45 StartY=190.293 StartZ=0 EndX=287.18 EndY=190.293 EndZ=0
    g33: ArcOfCircle CenterX=10.7 CenterY=198.73 CenterZ=0 NormalX=0 NormalY=0 NormalZ=1 AngleXU=0 Radius=1.25 StartAngle=1.5708 EndAngle=3.14159
    g34: LineSegment StartX=10.7 StartY=199.98 StartZ=0 EndX=30.7 EndY=199.98 EndZ=0
    g35: ArcOfCircle CenterX=30.7 CenterY=198.73 CenterZ=0 NormalX=0 NormalY=0 NormalZ=1 AngleXU=0 Radius=1.25 StartAngle=6.6e-15 EndAngle=1.5708
    g36: LineSegment StartX=31.95 StartY=198.73 StartZ=0 EndX=31.95 EndY=191.543 EndZ=0
    g37: ArcOfCircle CenterX=30.7 CenterY=191.543 CenterZ=0 NormalX=0 NormalY=0 NormalZ=1 AngleXU=0 Radius=1.25 StartAngle=4.71239 EndAngle=6.28319
    g38: LineSegment StartX=30.7 StartY=190.293 StartZ=0 EndX=10.7 EndY=190.293 EndZ=0
    g39: ArcOfCircle CenterX=10.7 CenterY=191.543 CenterZ=0 NormalX=0 NormalY=0 NormalZ=1 AngleXU=0 Radius=1.25 StartAngle=3.14159 EndAngle=4.71239
    g40: LineSegment StartX=9.45 StartY=191.543 StartZ=0 EndX=9.45 EndY=198.73 EndZ=0
    g41: GeomPoint X=9.45 Y=199.98 Z=0
    g42: GeomPoint X=31.95 Y=190.293 Z=0
    g43: ArcOfCircle CenterX=36.7946 CenterY=198.73 CenterZ=0 NormalX=0 NormalY=0 NormalZ=1 AngleXU=0 Radius=1.25 StartAngle=1.5708 EndAngle=3.14159
    g44: LineSegment StartX=36.7946 StartY=199.98 StartZ=0 EndX=49.7946 EndY=199.98 EndZ=0
    g45: ArcOfCircle CenterX=49.7946 CenterY=198.73 CenterZ=0 NormalX=0 NormalY=0 NormalZ=1 AngleXU=0 Radius=1.25 StartAngle=4e-16 EndAngle=1.5708
    g46: LineSegment StartX=51.0446 StartY=198.73 StartZ=0 EndX=51.0446 EndY=191.543 EndZ=0
    g47: ArcOfCircle CenterX=49.7946 CenterY=191.543 CenterZ=0 NormalX=0 NormalY=0 NormalZ=1 AngleXU=0 Radius=1.25 StartAngle=4.71239 EndAngle=6.28319
    g48: LineSegment StartX=49.7946 StartY=190.293 StartZ=0 EndX=36.7946 EndY=190.293 EndZ=0
    g49: ArcOfCircle CenterX=36.7946 CenterY=191.543 CenterZ=0 NormalX=0 NormalY=0 NormalZ=1 AngleXU=0 Radius=1.25 StartAngle=3.14159 EndAngle=4.71239
    g50: LineSegment StartX=35.5446 StartY=191.543 StartZ=0 EndX=35.5446 EndY=198.73 EndZ=0
    g51: GeomPoint X=35.5446 Y=199.98 Z=0
    g52: GeomPoint X=51.0446 Y=190.293 Z=0
    g53: ArcOfCircle CenterX=55.8892 CenterY=198.73 CenterZ=0 NormalX=0 NormalY=0 NormalZ=1 AngleXU=0 Radius=1.25 StartAngle=1.5708 EndAngle=3.14159
    g54: LineSegment StartX=55.8892 StartY=199.981 StartZ=0 EndX=68.8892 EndY=199.981 EndZ=0
    g55: ArcOfCircle CenterX=68.8892 CenterY=198.73 CenterZ=0 NormalX=0 NormalY=0 NormalZ=1 AngleXU=0 Radius=1.25 StartAngle=8.7e-15 EndAngle=1.5708
    g56: LineSegment StartX=70.1392 StartY=198.73 StartZ=0 EndX=70.1392 EndY=191.543 EndZ=0
    g57: ArcOfCircle CenterX=68.8892 CenterY=191.543 CenterZ=0 NormalX=0 NormalY=0 NormalZ=1 AngleXU=0 Radius=1.25 StartAngle=4.71239 EndAngle=6.28319
    g58: LineSegment StartX=68.8892 StartY=190.293 StartZ=0 EndX=55.8892 EndY=190.293 EndZ=0
    g59: ArcOfCircle CenterX=55.8892 CenterY=191.543 CenterZ=0 NormalX=0 NormalY=0 NormalZ=1 AngleXU=0 Radius=1.25 StartAngle=3.14159 EndAngle=4.71239
    g60: LineSegment StartX=54.6392 StartY=191.543 StartZ=0 EndX=54.6392 EndY=198.73 EndZ=0
    g61: GeomPoint X=54.6392 Y=199.98 Z=0
    g62: GeomPoint X=70.1392 Y=190.293 Z=0
    g63: ArcOfCircle CenterX=74.9838 CenterY=198.73 CenterZ=0 NormalX=0 NormalY=0 NormalZ=1 AngleXU=0 Radius=1.25 StartAngle=1.5708 EndAngle=3.14159
    g64: LineSegment StartX=74.9838 StartY=199.981 StartZ=0 EndX=87.9838 EndY=199.981 EndZ=0
    g65: ArcOfCircle CenterX=87.9838 CenterY=198.73 CenterZ=0 NormalX=0 NormalY=0 NormalZ=1 AngleXU=0 Radius=1.25 StartAngle=1.08e-14 EndAngle=1.5708
    g66: LineSegment StartX=89.2338 StartY=198.73 StartZ=0 EndX=89.2338 EndY=191.543 EndZ=0
    g67: ArcOfCircle CenterX=87.9838 CenterY=191.543 CenterZ=0 NormalX=0 NormalY=0 NormalZ=1 AngleXU=0 Radius=1.25 StartAngle=4.71239 EndAngle=6.28319
    g68: LineSegment StartX=87.9838 StartY=190.293 StartZ=0 EndX=74.9838 EndY=190.293 EndZ=0
    g69: ArcOfCircle CenterX=74.9838 CenterY=191.543 CenterZ=0 NormalX=0 NormalY=0 NormalZ=1 AngleXU=0 Radius=1.25 StartAngle=3.14159 EndAngle=4.71239
    g70: LineSegment StartX=73.7338 StartY=191.543 StartZ=0 EndX=73.7338 EndY=198.73 EndZ=0
    g71: GeomPoint X=73.7338 Y=199.98 Z=0
    g72: GeomPoint X=89.2338 Y=190.293 Z=0
    g73: ArcOfCircle CenterX=94.0785 CenterY=198.73 CenterZ=0 NormalX=0 NormalY=0 NormalZ=1 AngleXU=0 Radius=1.25 StartAngle=1.5708 EndAngle=3.14159
    g74: LineSegment StartX=94.0785 StartY=199.98 StartZ=0 EndX=107.078 EndY=199.98 EndZ=0
    g75: ArcOfCircle CenterX=107.078 CenterY=198.73 CenterZ=0 NormalX=0 NormalY=0 NormalZ=1 AngleXU=0 Radius=1.25 StartAngle=2.2e-15 EndAngle=1.5708
    g76: LineSegment StartX=108.328 StartY=198.73 StartZ=0 EndX=108.328 EndY=191.543 EndZ=0
    g77: ArcOfCircle CenterX=107.078 CenterY=191.543 CenterZ=0 NormalX=0 NormalY=0 NormalZ=1 AngleXU=0 Radius=1.25 StartAngle=4.71239 EndAngle=6.28319
    g78: LineSegment StartX=107.078 StartY=190.293 StartZ=0 EndX=94.0785 EndY=190.293 EndZ=0
    g79: ArcOfCircle CenterX=94.0785 CenterY=191.543 CenterZ=0 NormalX=0 NormalY=0 NormalZ=1 AngleXU=0 Radius=1.25 StartAngle=3.14159 EndAngle=4.71239
    g80: LineSegment StartX=92.8285 StartY=191.543 StartZ=0 EndX=92.8285 EndY=198.73 EndZ=0
    g81: GeomPoint X=92.8285 Y=199.98 Z=0
    g82: GeomPoint X=108.328 Y=190.293 Z=0
    g83: ArcOfCircle CenterX=113.173 CenterY=198.73 CenterZ=0 NormalX=0 NormalY=0 NormalZ=1 AngleXU=0 Radius=1.25 StartAngle=1.5708 EndAngle=3.14159
    g84: LineSegment StartX=113.173 StartY=199.98 StartZ=0 EndX=126.173 EndY=199.98 EndZ=0
    g85: ArcOfCircle CenterX=126.173 CenterY=198.73 CenterZ=0 NormalX=0 NormalY=0 NormalZ=1 AngleXU=0 Radius=1.25 StartAngle=5.7e-15 EndAngle=1.5708
    g86: LineSegment StartX=127.423 StartY=198.73 StartZ=0 EndX=127.423 EndY=191.543 EndZ=0
    g87: ArcOfCircle CenterX=126.173 CenterY=191.543 CenterZ=0 NormalX=0 NormalY=0 NormalZ=1 AngleXU=0 Radius=1.25 StartAngle=4.71239 EndAngle=6.28319
    g88: LineSegment StartX=126.173 StartY=190.293 StartZ=0 EndX=113.173 EndY=190.293 EndZ=0
    g89: ArcOfCircle CenterX=113.173 CenterY=191.543 CenterZ=0 NormalX=0 NormalY=0 NormalZ=1 AngleXU=0 Radius=1.25 StartAngle=3.14159 EndAngle=4.71239
    g90: LineSegment StartX=111.923 StartY=191.543 StartZ=0 EndX=111.923 EndY=198.73 EndZ=0
    g91: GeomPoint X=111.923 Y=199.98 Z=0
    g92: GeomPoint X=127.423 Y=190.293 Z=0
    g93: ArcOfCircle CenterX=132.268 CenterY=198.73 CenterZ=0 NormalX=0 NormalY=0 NormalZ=1 AngleXU=0 Radius=1.25 StartAngle=1.5708 EndAngle=3.14159
    g94: LineSegment StartX=132.268 StartY=199.98 StartZ=0 EndX=145.268 EndY=199.98 EndZ=0
    g95: ArcOfCircle CenterX=145.268 CenterY=198.73 CenterZ=0 NormalX=0 NormalY=0 NormalZ=1 AngleXU=0 Radius=1.25 StartAngle=1.06e-14 EndAngle=1.5708
    g96: LineSegment StartX=146.518 StartY=198.73 StartZ=0 EndX=146.518 EndY=191.543 EndZ=0
    g97: ArcOfCircle CenterX=145.268 CenterY=191.543 CenterZ=0 NormalX=0 NormalY=0 NormalZ=1 AngleXU=0 Radius=1.25 StartAngle=4.71239 EndAngle=6.28319
    g98: LineSegment StartX=145.268 StartY=190.293 StartZ=0 EndX=132.268 EndY=190.293 EndZ=0
    g99: ArcOfCircle CenterX=132.268 CenterY=191.543 CenterZ=0 NormalX=0 NormalY=0 NormalZ=1 AngleXU=0 Radius=1.25 StartAngle=3.14159 EndAngle=4.71239
    g100: LineSegment StartX=131.018 StartY=191.543 StartZ=0 EndX=131.018 EndY=198.73 EndZ=0
    g101: GeomPoint X=131.018 Y=199.98 Z=0
    g102: GeomPoint X=146.518 Y=190.293 Z=0
    g103: ArcOfCircle CenterX=151.362 CenterY=191.543 CenterZ=0 NormalX=0 NormalY=0 NormalZ=1 AngleXU=0 Radius=1.25 StartAngle=3.14159 EndAngle=4.71239
    g104: LineSegment StartX=150.112 StartY=191.543 StartZ=0 EndX=150.112 EndY=198.73 EndZ=0
    g105: ArcOfCircle CenterX=151.362 CenterY=198.73 CenterZ=0 NormalX=0 NormalY=0 NormalZ=1 AngleXU=0 Radius=1.25 StartAngle=1.5708 EndAngle=3.14159
    g106: LineSegment StartX=151.362 StartY=199.98 StartZ=0 EndX=164.362 EndY=199.98 EndZ=0
    g107: ArcOfCircle CenterX=164.362 CenterY=198.73 CenterZ=0 NormalX=0 NormalY=0 NormalZ=1 AngleXU=0 Radius=1.25 StartAngle=-9e-16 EndAngle=1.5708
    g108: LineSegment StartX=165.612 StartY=198.73 StartZ=0 EndX=165.612 EndY=191.543 EndZ=0
    g109: ArcOfCircle CenterX=164.362 CenterY=191.543 CenterZ=0 NormalX=0 NormalY=0 NormalZ=1 AngleXU=0 Radius=1.25 StartAngle=4.71239 EndAngle=6.28319
    g110: LineSegment StartX=164.362 StartY=190.293 StartZ=0 EndX=151.362 EndY=190.293 EndZ=0
    g111: GeomPoint X=150.112 Y=190.293 Z=0
    g112: GeomPoint X=165.612 Y=199.98 Z=0
    g113: ArcOfCircle CenterX=170.457 CenterY=198.73 CenterZ=0 NormalX=0 NormalY=0 NormalZ=1 AngleXU=0 Radius=1.25 StartAngle=1.5708 EndAngle=3.14159
    g114: LineSegment StartX=170.457 StartY=199.98 StartZ=0 EndX=183.457 EndY=199.98 EndZ=0
    g115: ArcOfCircle CenterX=183.457 CenterY=198.73 CenterZ=0 NormalX=0 NormalY=0 NormalZ=1 AngleXU=0 Radius=1.25 StartAngle=2.2e-15 EndAngle=1.5708
    g116: LineSegment StartX=184.707 StartY=198.73 StartZ=0 EndX=184.707 EndY=191.543 EndZ=0
    g117: ArcOfCircle CenterX=183.457 CenterY=191.543 CenterZ=0 NormalX=0 NormalY=0 NormalZ=1 AngleXU=0 Radius=1.25 StartAngle=4.71239 EndAngle=6.28319
    g118: LineSegment StartX=183.457 StartY=190.293 StartZ=0 EndX=170.457 EndY=190.293 EndZ=0
    g119: ArcOfCircle CenterX=170.457 CenterY=191.543 CenterZ=0 NormalX=0 NormalY=0 NormalZ=1 AngleXU=0 Radius=1.25 StartAngle=3.14159 EndAngle=4.71239
    g120: LineSegment StartX=169.207 StartY=191.543 StartZ=0 EndX=169.207 EndY=198.73 EndZ=0
    g121: GeomPoint X=169.207 Y=199.98 Z=0
    g122: GeomPoint X=184.707 Y=190.293 Z=0
    g123: ArcOfCircle CenterX=189.552 CenterY=198.73 CenterZ=0 NormalX=0 NormalY=0 NormalZ=1 AngleXU=0 Radius=1.25 StartAngle=1.5708 EndAngle=3.14159
    g124: LineSegment StartX=189.552 StartY=199.98 StartZ=0 EndX=202.552 EndY=199.98 EndZ=0
    g125: ArcOfCircle CenterX=202.552 CenterY=198.73 CenterZ=0 NormalX=0 NormalY=0 NormalZ=1 AngleXU=0 Radius=1.25 StartAngle=8.7e-15 EndAngle=1.5708
    g126: LineSegment StartX=203.802 StartY=198.73 StartZ=0 EndX=203.802 EndY=191.543 EndZ=0
    g127: ArcOfCircle CenterX=202.552 CenterY=191.543 CenterZ=0 NormalX=0 NormalY=0 NormalZ=1 AngleXU=0 Radius=1.25 StartAngle=4.71239 EndAngle=6.28319
    g128: LineSegment StartX=202.552 StartY=190.293 StartZ=0 EndX=189.552 EndY=190.293 EndZ=0
    g129: ArcOfCircle CenterX=189.552 CenterY=191.543 CenterZ=0 NormalX=0 NormalY=0 NormalZ=1 AngleXU=0 Radius=1.25 StartAngle=3.14159 EndAngle=4.71239
    g130: LineSegment StartX=188.302 StartY=191.543 StartZ=0 EndX=188.302 EndY=198.73 EndZ=0
    g131: GeomPoint X=188.302 Y=199.98 Z=0
    g132: GeomPoint X=203.802 Y=190.293 Z=0
    g133: ArcOfCircle CenterX=208.646 CenterY=198.73 CenterZ=0 NormalX=0 NormalY=0 NormalZ=1 AngleXU=0 Radius=1.25 StartAngle=1.5708 EndAngle=3.14159
    g134: LineSegment StartX=208.646 StartY=199.98 StartZ=0 EndX=221.646 EndY=199.98 EndZ=0
    g135: ArcOfCircle CenterX=221.646 CenterY=198.73 CenterZ=0 NormalX=0 NormalY=0 NormalZ=1 AngleXU=0 Radius=1.25 StartAngle=-2.7e-15 EndAngle=1.5708
    g136: LineSegment StartX=222.896 StartY=198.73 StartZ=0 EndX=222.896 EndY=191.543 EndZ=0
    g137: ArcOfCircle CenterX=221.646 CenterY=191.543 CenterZ=0 NormalX=0 NormalY=0 NormalZ=1 AngleXU=0 Radius=1.25 StartAngle=4.71239 EndAngle=6.28319
    g138: LineSegment StartX=221.646 StartY=190.293 StartZ=0 EndX=208.646 EndY=190.293 EndZ=0
    g139: ArcOfCircle CenterX=208.646 CenterY=191.543 CenterZ=0 NormalX=0 NormalY=0 NormalZ=1 AngleXU=0 Radius=1.25 StartAngle=3.14159 EndAngle=4.71239
    g140: LineSegment StartX=207.396 StartY=191.543 StartZ=0 EndX=207.396 EndY=198.73 EndZ=0
    g141: GeomPoint X=207.396 Y=199.98 Z=0
    g142: GeomPoint X=222.896 Y=190.293 Z=0
    g143: ArcOfCircle CenterX=285.93 CenterY=198.73 CenterZ=0 NormalX=0 NormalY=0 NormalZ=1 AngleXU=0 Radius=1.25 StartAngle=-4.4e-15 EndAngle=1.5708
    g144: LineSegment StartX=287.18 StartY=198.73 StartZ=0 EndX=287.18 EndY=191.543 EndZ=0
    g145: ArcOfCircle CenterX=285.93 CenterY=191.543 CenterZ=0 NormalX=0 NormalY=0 NormalZ=1 AngleXU=0 Radius=1.25 StartAngle=4.71239 EndAngle=6.28319
    g146: LineSegment StartX=285.93 StartY=190.293 StartZ=0 EndX=265.93 EndY=190.293 EndZ=0
    g147: ArcOfCircle CenterX=265.93 CenterY=191.543 CenterZ=0 NormalX=0 NormalY=0 NormalZ=1 AngleXU=0 Radius=1.25 StartAngle=3.14159 EndAngle=4.71239
    g148: LineSegment StartX=264.68 StartY=191.543 StartZ=0 EndX=264.68 EndY=198.73 EndZ=0
    g149: ArcOfCircle CenterX=265.93 CenterY=198.73 CenterZ=0 NormalX=0 NormalY=0 NormalZ=1 AngleXU=0 Radius=1.25 StartAngle=1.5708 EndAngle=3.14159
    g150: LineSegment StartX=265.93 StartY=199.98 StartZ=0 EndX=285.93 EndY=199.98 EndZ=0
    g151: GeomPoint X=287.18 Y=199.98 Z=0
    g152: GeomPoint X=264.68 Y=190.293 Z=0
    g153: ArcOfCircle CenterX=227.741 CenterY=198.73 CenterZ=0 NormalX=0 NormalY=0 NormalZ=1 AngleXU=0 Radius=1.25 StartAngle=1.5708 EndAngle=3.14159
    g154: LineSegment StartX=227.741 StartY=199.98 StartZ=0 EndX=240.741 EndY=199.98 EndZ=0
    g155: ArcOfCircle CenterX=240.741 CenterY=198.73 CenterZ=0 NormalX=0 NormalY=0 NormalZ=1 AngleXU=0 Radius=1.25 StartAngle=-5.3e-15 EndAngle=1.5708
    g156: LineSegment StartX=241.991 StartY=198.73 StartZ=0 EndX=241.991 EndY=191.543 EndZ=0
    g157: ArcOfCircle CenterX=240.741 CenterY=191.543 CenterZ=0 NormalX=0 NormalY=0 NormalZ=1 AngleXU=0 Radius=1.25 StartAngle=4.71239 EndAngle=6.28319
    g158: LineSegment StartX=240.741 StartY=190.293 StartZ=0 EndX=227.741 EndY=190.293 EndZ=0
    g159: ArcOfCircle CenterX=227.741 CenterY=191.543 CenterZ=0 NormalX=0 NormalY=0 NormalZ=1 AngleXU=0 Radius=1.25 StartAngle=3.14159 EndAngle=4.71239
    g160: LineSegment StartX=226.491 StartY=191.543 StartZ=0 EndX=226.491 EndY=198.73 EndZ=0
    g161: GeomPoint X=226.491 Y=199.98 Z=0
    g162: GeomPoint X=241.991 Y=190.293 Z=0
    g163: ArcOfCircle CenterX=246.835 CenterY=198.73 CenterZ=0 NormalX=0 NormalY=0 NormalZ=1 AngleXU=0 Radius=1.25 StartAngle=1.5708 EndAngle=3.14159
    g164: LineSegment StartX=246.835 StartY=199.981 StartZ=0 EndX=259.835 EndY=199.981 EndZ=0
    g165: ArcOfCircle CenterX=259.835 CenterY=198.73 CenterZ=0 NormalX=0 NormalY=0 NormalZ=1 AngleXU=0 Radius=1.25 StartAngle=-5.3e-15 EndAngle=1.5708
    g166: LineSegment StartX=261.085 StartY=198.73 StartZ=0 EndX=261.085 EndY=191.543 EndZ=0
    g167: ArcOfCircle CenterX=259.835 CenterY=191.543 CenterZ=0 NormalX=0 NormalY=0 NormalZ=1 AngleXU=0 Radius=1.25 StartAngle=4.71239 EndAngle=6.28319
    g168: LineSegment StartX=259.835 StartY=190.293 StartZ=0 EndX=246.835 EndY=190.293 EndZ=0
    g169: ArcOfCircle CenterX=246.835 CenterY=191.543 CenterZ=0 NormalX=0 NormalY=0 NormalZ=1 AngleXU=0 Radius=1.25 StartAngle=3.14159 EndAngle=4.71239
    g170: LineSegment StartX=245.585 StartY=191.543 StartZ=0 EndX=245.585 EndY=198.73 EndZ=0
    g171: GeomPoint X=245.585 Y=199.98 Z=0
    g172: GeomPoint X=261.085 Y=190.293 Z=0
    g173: LineSegment StartX=264.68 StartY=198.73 StartZ=0 EndX=261.085 EndY=198.73 EndZ=0
    g174: LineSegment StartX=245.585 StartY=198.73 StartZ=0 EndX=241.991 EndY=198.73 EndZ=0
    g175: LineSegment StartX=226.491 StartY=198.73 StartZ=0 EndX=222.896 EndY=198.73 EndZ=0
    g176: LineSegment StartX=207.396 StartY=198.73 StartZ=0 EndX=203.802 EndY=198.73 EndZ=0
    g177: LineSegment StartX=188.302 StartY=198.73 StartZ=0 EndX=184.707 EndY=198.73 EndZ=0
    g178: LineSegment StartX=169.207 StartY=198.73 StartZ=0 EndX=165.612 EndY=198.73 EndZ=0
    g179: LineSegment StartX=150.112 StartY=198.73 StartZ=0 EndX=146.518 EndY=198.73 EndZ=0
    g180: LineSegment StartX=131.018 StartY=198.73 StartZ=0 EndX=127.423 EndY=198.73 EndZ=0
    g181: LineSegment StartX=111.923 StartY=198.73 StartZ=0 EndX=108.328 EndY=198.73 EndZ=0
    g182: LineSegment StartX=92.8285 StartY=198.73 StartZ=0 EndX=89.2338 EndY=198.73 EndZ=0
    g183: LineSegment StartX=54.6392 StartY=198.73 StartZ=0 EndX=51.0446 EndY=198.73 EndZ=0
    g184: LineSegment StartX=35.5446 StartY=198.73 StartZ=0 EndX=31.95 EndY=198.73 EndZ=0
    g185: LineSegment StartX=73.7338 StartY=198.73 StartZ=0 EndX=70.1392 EndY=198.73 EndZ=0
    g186: LineSegment StartX=287.18 StartY=186.698 StartZ=0 EndX=9.45 EndY=186.698 EndZ=0
    g187: LineSegment StartX=9.45 StartY=171.198 StartZ=0 EndX=287.18 EndY=171.198 EndZ=0
    g188: LineSegment StartX=287.18 StartY=167.604 StartZ=0 EndX=9.45 EndY=167.604 EndZ=0
    g189: LineSegment StartX=9.45 StartY=152.104 StartZ=0 EndX=287.18 EndY=152.104 EndZ=0
    g190: LineSegment StartX=287.18 StartY=148.509 StartZ=0 EndX=9.45 EndY=148.509 EndZ=0
    g191: LineSegment StartX=9.45 StartY=133.009 StartZ=0 EndX=287.18 EndY=133.009 EndZ=0
    g192: LineSegment StartX=287.18 StartY=129.415 StartZ=0 EndX=9.45 EndY=129.415 EndZ=0
    g193: LineSegment StartX=287.18 StartY=113.915 StartZ=0 EndX=9.45 EndY=113.915 EndZ=0
    g194: LineSegment StartX=287.18 StartY=110.32 StartZ=0 EndX=9.45 EndY=110.32 EndZ=0
    g195: ArcOfCircle CenterX=285.93 CenterY=172.448 CenterZ=0 NormalX=0 NormalY=0 NormalZ=1 AngleXU=0 Radius=1.25 StartAngle=4.71239 EndAngle=6.28319
    g196: LineSegment StartX=285.93 StartY=171.198 StartZ=0 EndX=258.93 EndY=171.198 EndZ=0
    g197: ArcOfCircle CenterX=258.93 CenterY=172.448 CenterZ=0 NormalX=0 NormalY=0 NormalZ=1 AngleXU=0 Radius=1.25 StartAngle=3.14159 EndAngle=4.71239
    g198: LineSegment StartX=257.68 StartY=172.448 StartZ=0 EndX=257.68 EndY=185.448 EndZ=0
    g199: ArcOfCircle CenterX=258.93 CenterY=185.448 CenterZ=0 NormalX=0 NormalY=0 NormalZ=1 AngleXU=0 Radius=1.25 StartAngle=1.5708 EndAngle=3.14159
    g200: LineSegment StartX=258.93 StartY=186.698 StartZ=0 EndX=285.93 EndY=186.698 EndZ=0
    g201: ArcOfCircle CenterX=285.93 CenterY=185.448 CenterZ=0 NormalX=0 NormalY=0 NormalZ=1 AngleXU=0 Radius=1.25 StartAngle=4e-16 EndAngle=1.5708
    g202: LineSegment StartX=287.18 StartY=185.448 StartZ=0 EndX=287.18 EndY=172.448 EndZ=0
    g203: GeomPoint X=287.18 Y=171.198 Z=0
    g204: GeomPoint X=257.68 Y=186.698 Z=0
    g205: ArcOfCircle CenterX=285.93 CenterY=153.354 CenterZ=0 NormalX=0 NormalY=0 NormalZ=1 AngleXU=0 Radius=1.25 StartAngle=4.71239 EndAngle=6.28319
    g206: LineSegment StartX=285.93 StartY=152.104 StartZ=0 EndX=267.93 EndY=152.104 EndZ=0
    g207: ArcOfCircle CenterX=267.93 CenterY=153.354 CenterZ=0 NormalX=0 NormalY=0 NormalZ=1 AngleXU=0 Radius=1.25 StartAngle=3.14159 EndAngle=4.71239
    g208: LineSegment StartX=266.68 StartY=153.354 StartZ=0 EndX=266.68 EndY=166.354 EndZ=0
    g209: ArcOfCircle CenterX=267.93 CenterY=166.354 CenterZ=0 NormalX=0 NormalY=0 NormalZ=1 AngleXU=0 Radius=1.25 StartAngle=1.5708 EndAngle=3.14159
    g210: LineSegment StartX=267.93 StartY=167.604 StartZ=0 EndX=285.93 EndY=167.604 EndZ=0
    g211: ArcOfCircle CenterX=285.93 CenterY=166.354 CenterZ=0 NormalX=0 NormalY=0 NormalZ=1 AngleXU=0 Radius=1.25 StartAngle=-4.4e-15 EndAngle=1.5708
    g212: LineSegment StartX=287.18 StartY=166.354 StartZ=0 EndX=287.18 EndY=153.354 EndZ=0
    g213: GeomPoint X=287.18 Y=152.104 Z=0
    g214: GeomPoint X=266.68 Y=167.604 Z=0
    g215: ArcOfCircle CenterX=253.555 CenterY=147.259 CenterZ=0 NormalX=0 NormalY=0 NormalZ=1 AngleXU=0 Radius=1.25 StartAngle=1.5708 EndAngle=3.14159
    g216: LineSegment StartX=253.555 StartY=148.509 StartZ=0 EndX=285.93 EndY=148.509 EndZ=0
    g217: ArcOfCircle CenterX=285.93 CenterY=147.259 CenterZ=0 NormalX=0 NormalY=0 NormalZ=1 AngleXU=0 Radius=1.25 StartAngle=9.6e-15 EndAngle=1.5708
    g218: LineSegment StartX=287.18 StartY=147.259 StartZ=0 EndX=287.18 EndY=134.259 EndZ=0
    g219: ArcOfCircle CenterX=285.93 CenterY=134.259 CenterZ=0 NormalX=0 NormalY=0 NormalZ=1 AngleXU=0 Radius=1.25 StartAngle=4.71239 EndAngle=6.28319
    g220: LineSegment StartX=285.93 StartY=133.009 StartZ=0 EndX=253.555 EndY=133.009 EndZ=0
    g221: ArcOfCircle CenterX=253.555 CenterY=134.259 CenterZ=0 NormalX=0 NormalY=0 NormalZ=1 AngleXU=0 Radius=1.25 StartAngle=3.14159 EndAngle=4.71239
    g222: LineSegment StartX=252.305 StartY=134.259 StartZ=0 EndX=252.305 EndY=147.259 EndZ=0
    g223: GeomPoint X=252.305 Y=148.509 Z=0
    g224: GeomPoint X=287.18 Y=133.009 Z=0
    g225: ArcOfCircle CenterX=244.643 CenterY=128.165 CenterZ=0 NormalX=0 NormalY=0 NormalZ=1 AngleXU=0 Radius=1.25 StartAngle=1.5708 EndAngle=3.14159
    g226: LineSegment StartX=244.643 StartY=129.415 StartZ=0 EndX=285.93 EndY=129.415 EndZ=0
    g227: ArcOfCircle CenterX=285.93 CenterY=128.165 CenterZ=0 NormalX=0 NormalY=0 NormalZ=1 AngleXU=0 Radius=1.25 StartAngle=-6.2e-15 EndAngle=1.5708
    g228: LineSegment StartX=287.18 StartY=128.165 StartZ=0 EndX=287.18 EndY=115.165 EndZ=0
    g229: ArcOfCircle CenterX=285.93 CenterY=115.165 CenterZ=0 NormalX=0 NormalY=0 NormalZ=1 AngleXU=0 Radius=1.25 StartAngle=4.71239 EndAngle=6.28319
    g230: LineSegment StartX=285.93 StartY=113.915 StartZ=0 EndX=244.643 EndY=113.915 EndZ=0
    g231: ArcOfCircle CenterX=244.643 CenterY=115.165 CenterZ=0 NormalX=0 NormalY=0 NormalZ=1 AngleXU=0 Radius=1.25 StartAngle=3.14159 EndAngle=4.71239
    g232: LineSegment StartX=243.393 StartY=115.165 StartZ=0 EndX=243.393 EndY=128.165 EndZ=0
    g233: GeomPoint X=243.393 Y=129.415 Z=0
    g234: GeomPoint X=287.18 Y=113.915 Z=0
    g235: ArcOfCircle CenterX=269.805 CenterY=109.07 CenterZ=0 NormalX=0 NormalY=0 NormalZ=1 AngleXU=0 Radius=1.25 StartAngle=1.5708 EndAngle=3.14159
    g236: LineSegment StartX=269.805 StartY=110.32 StartZ=0 EndX=285.93 EndY=110.32 EndZ=0
    g237: ArcOfCircle CenterX=285.93 CenterY=109.07 CenterZ=0 NormalX=0 NormalY=0 NormalZ=1 AngleXU=0 Radius=1.25 StartAngle=-4.4e-15 EndAngle=1.5708
    g238: LineSegment StartX=287.18 StartY=109.07 StartZ=0 EndX=287.18 EndY=96.0699 EndZ=0
    g239: ArcOfCircle CenterX=285.93 CenterY=96.0699 CenterZ=0 NormalX=0 NormalY=0 NormalZ=1 AngleXU=0 Radius=1.25 StartAngle=4.71239 EndAngle=6.28319
    g240: LineSegment StartX=285.93 StartY=94.8199 StartZ=0 EndX=269.805 EndY=94.8199 EndZ=0
    g241: ArcOfCircle CenterX=269.805 CenterY=96.0699 CenterZ=0 NormalX=0 NormalY=0 NormalZ=1 AngleXU=0 Radius=1.25 StartAngle=3.14159 EndAngle=4.71239
    g242: LineSegment StartX=268.555 StartY=96.0699 StartZ=0 EndX=268.555 EndY=109.07 EndZ=0
    g243: GeomPoint X=268.555 Y=110.32 Z=0
    g244: GeomPoint X=287.18 Y=94.8199 Z=0
    g245: LineSegment StartX=285.93 StartY=110.32 StartZ=0 EndX=285.93 EndY=113.915 EndZ=0
    g246: LineSegment StartX=285.93 StartY=129.415 StartZ=0 EndX=285.93 EndY=133.009 EndZ=0
    g247: LineSegment StartX=285.93 StartY=148.509 StartZ=0 EndX=285.93 EndY=152.104 EndZ=0
    g248: LineSegment StartX=285.93 StartY=167.604 StartZ=0 EndX=285.93 EndY=171.198 EndZ=0
    g249: LineSegment StartX=285.93 StartY=186.698 StartZ=0 EndX=285.93 EndY=190.293 EndZ=0
    g250: ArcOfCircle CenterX=263.71 CenterY=109.07 CenterZ=0 NormalX=0 NormalY=0 NormalZ=1 AngleXU=0 Radius=1.25 StartAngle=-5.3e-15 EndAngle=1.5708
    g251: LineSegment StartX=264.96 StartY=109.07 StartZ=0 EndX=264.96 EndY=96.0699 EndZ=0
    g252: ArcOfCircle CenterX=263.71 CenterY=96.0699 CenterZ=0 NormalX=0 NormalY=0 NormalZ=1 AngleXU=0 Radius=1.25 StartAngle=4.71239 EndAngle=6.28319
    g253: LineSegment StartX=263.71 StartY=94.8199 StartZ=0 EndX=247.585 EndY=94.8199 EndZ=0
    g254: ArcOfCircle CenterX=247.585 CenterY=96.0699 CenterZ=0 NormalX=0 NormalY=0 NormalZ=1 AngleXU=0 Radius=1.25 StartAngle=3.14159 EndAngle=4.71239
    g255: LineSegment StartX=246.335 StartY=96.0699 StartZ=0 EndX=246.335 EndY=109.07 EndZ=0
    g256: ArcOfCircle CenterX=247.585 CenterY=109.07 CenterZ=0 NormalX=0 NormalY=0 NormalZ=1 AngleXU=0 Radius=1.25 StartAngle=1.5708 EndAngle=3.14159
    g257: LineSegment StartX=247.585 StartY=110.32 StartZ=0 EndX=263.71 EndY=110.32 EndZ=0
    g258: GeomPoint X=264.96 Y=110.32 Z=0
    g259: GeomPoint X=246.335 Y=94.8199 Z=0
    g260: ArcOfCircle CenterX=241.491 CenterY=109.07 CenterZ=0 NormalX=0 NormalY=0 NormalZ=1 AngleXU=0 Radius=1.25 StartAngle=-1.8e-15 EndAngle=1.5708
    g261: LineSegment StartX=242.741 StartY=109.07 StartZ=0 EndX=242.741 EndY=96.0699 EndZ=0
    g262: ArcOfCircle CenterX=241.491 CenterY=96.0699 CenterZ=0 NormalX=0 NormalY=0 NormalZ=1 AngleXU=0 Radius=1.25 StartAngle=4.71239 EndAngle=6.28319
    g263: LineSegment StartX=241.491 StartY=94.8199 StartZ=0 EndX=225.366 EndY=94.8199 EndZ=0
    g264: ArcOfCircle CenterX=225.366 CenterY=96.0699 CenterZ=0 NormalX=0 NormalY=0 NormalZ=1 AngleXU=0 Radius=1.25 StartAngle=3.14159 EndAngle=4.71239
    g265: LineSegment StartX=224.116 StartY=96.0699 StartZ=0 EndX=224.116 EndY=109.07 EndZ=0
    g266: ArcOfCircle CenterX=225.366 CenterY=109.07 CenterZ=0 NormalX=0 NormalY=0 NormalZ=1 AngleXU=0 Radius=1.25 StartAngle=1.5708 EndAngle=3.14159
    g267: LineSegment StartX=225.366 StartY=110.32 StartZ=0 EndX=241.491 EndY=110.32 EndZ=0
    g268: GeomPoint X=242.741 Y=110.32 Z=0
    g269: GeomPoint X=224.116 Y=94.8199 Z=0
    g270: ArcOfCircle CenterX=219.271 CenterY=109.07 CenterZ=0 NormalX=0 NormalY=0 NormalZ=1 AngleXU=0 Radius=1.25 StartAngle=-2.7e-15 EndAngle=1.5708
    g271: LineSegment StartX=220.521 StartY=109.07 StartZ=0 EndX=220.521 EndY=96.0699 EndZ=0
    g272: ArcOfCircle CenterX=219.271 CenterY=96.0699 CenterZ=0 NormalX=0 NormalY=0 NormalZ=1 AngleXU=0 Radius=1.25 StartAngle=4.71239 EndAngle=6.28319
    g273: LineSegment StartX=219.271 StartY=94.8199 StartZ=0 EndX=206.271 EndY=94.8199 EndZ=0
    g274: ArcOfCircle CenterX=206.271 CenterY=96.0699 CenterZ=0 NormalX=0 NormalY=0 NormalZ=1 AngleXU=0 Radius=1.25 StartAngle=3.14159 EndAngle=4.71239
    g275: LineSegment StartX=205.021 StartY=96.0699 StartZ=0 EndX=205.021 EndY=109.07 EndZ=0
    g276: ArcOfCircle CenterX=206.271 CenterY=109.07 CenterZ=0 NormalX=0 NormalY=0 NormalZ=1 AngleXU=0 Radius=1.25 StartAngle=1.5708 EndAngle=3.14159
    g277: LineSegment StartX=206.271 StartY=110.32 StartZ=0 EndX=219.271 EndY=110.32 EndZ=0
    g278: GeomPoint X=220.521 Y=110.32 Z=0
    g279: GeomPoint X=205.021 Y=94.8199 Z=0
    g280: ArcOfCircle CenterX=200.177 CenterY=109.07 CenterZ=0 NormalX=0 NormalY=0 NormalZ=1 AngleXU=0 Radius=1.25 StartAngle=3.9e-15 EndAngle=1.5708
    g281: LineSegment StartX=201.427 StartY=109.07 StartZ=0 EndX=201.427 EndY=96.0699 EndZ=0
    g282: ArcOfCircle CenterX=200.177 CenterY=96.0699 CenterZ=0 NormalX=0 NormalY=0 NormalZ=1 AngleXU=0 Radius=1.25 StartAngle=4.71239 EndAngle=6.28319
    g283: LineSegment StartX=200.177 StartY=94.8199 StartZ=0 EndX=187.177 EndY=94.8199 EndZ=0
    g284: ArcOfCircle CenterX=187.177 CenterY=96.0699 CenterZ=0 NormalX=0 NormalY=0 NormalZ=1 AngleXU=0 Radius=1.25 StartAngle=3.14159 EndAngle=4.71239
    g285: LineSegment StartX=185.927 StartY=96.0699 StartZ=0 EndX=185.927 EndY=109.07 EndZ=0
    g286: ArcOfCircle CenterX=187.177 CenterY=109.07 CenterZ=0 NormalX=0 NormalY=0 NormalZ=1 AngleXU=0 Radius=1.25 StartAngle=1.5708 EndAngle=3.14159
    g287: LineSegment StartX=187.177 StartY=110.32 StartZ=0 EndX=200.177 EndY=110.32 EndZ=0
    g288: GeomPoint X=201.427 Y=110.32 Z=0
    g289: GeomPoint X=185.927 Y=94.8199 Z=0
    g290: ArcOfCircle CenterX=181.082 CenterY=109.07 CenterZ=0 NormalX=0 NormalY=0 NormalZ=1 AngleXU=0 Radius=1.25 StartAngle=5.4e-15 EndAngle=1.5708
    g291: LineSegment StartX=182.332 StartY=109.07 StartZ=0 EndX=182.332 EndY=96.0699 EndZ=0
    g292: ArcOfCircle CenterX=181.082 CenterY=96.0699 CenterZ=0 NormalX=0 NormalY=0 NormalZ=1 AngleXU=0 Radius=1.25 StartAngle=4.71239 EndAngle=6.28319
    g293: LineSegment StartX=181.082 StartY=94.8199 StartZ=0 EndX=92.0785 EndY=94.8199 EndZ=0
    g294: ArcOfCircle CenterX=92.0785 CenterY=96.0699 CenterZ=0 NormalX=0 NormalY=0 NormalZ=1 AngleXU=0 Radius=1.25 StartAngle=3.14159 EndAngle=4.71239
    g295: LineSegment StartX=90.8285 StartY=96.0699 StartZ=0 EndX=90.8285 EndY=109.07 EndZ=0
    g296: ArcOfCircle CenterX=92.0785 CenterY=109.07 CenterZ=0 NormalX=0 NormalY=0 NormalZ=1 AngleXU=0 Radius=1.25 StartAngle=1.5708 EndAngle=3.14159
    g297: LineSegment StartX=92.0785 StartY=110.32 StartZ=0 EndX=181.082 EndY=110.32 EndZ=0
    g298: GeomPoint X=182.332 Y=110.32 Z=0
    g299: GeomPoint X=90.8285 Y=94.8199 Z=0
    g300: ArcOfCircle CenterX=85.9838 CenterY=109.07 CenterZ=0 NormalX=0 NormalY=0 NormalZ=1 AngleXU=0 Radius=1.25 StartAngle=4e-16 EndAngle=1.5708
    g301: LineSegment StartX=87.2338 StartY=109.07 StartZ=0 EndX=87.2338 EndY=96.0699 EndZ=0
    g302: ArcOfCircle CenterX=85.9838 CenterY=96.0699 CenterZ=0 NormalX=0 NormalY=0 NormalZ=1 AngleXU=0 Radius=1.25 StartAngle=4.71239 EndAngle=6.28319
    g303: LineSegment StartX=85.9838 StartY=94.8199 StartZ=0 EndX=72.9838 EndY=94.8199 EndZ=0
    g304: ArcOfCircle CenterX=72.9838 CenterY=96.0699 CenterZ=0 NormalX=0 NormalY=0 NormalZ=1 AngleXU=0 Radius=1.25 StartAngle=3.14159 EndAngle=4.71239
    g305: LineSegment StartX=71.7338 StartY=96.0699 StartZ=0 EndX=71.7338 EndY=109.07 EndZ=0
    g306: ArcOfCircle CenterX=72.9838 CenterY=109.07 CenterZ=0 NormalX=0 NormalY=0 NormalZ=1 AngleXU=0 Radius=1.25 StartAngle=1.5708 EndAngle=3.14159
    g307: LineSegment StartX=72.9838 StartY=110.32 StartZ=0 EndX=85.9838 EndY=110.32 EndZ=0
    g308: GeomPoint X=87.2338 Y=110.32 Z=0
    g309: GeomPoint X=71.7338 Y=94.8199 Z=0
    g310: ArcOfCircle CenterX=66.8892 CenterY=109.07 CenterZ=0 NormalX=0 NormalY=0 NormalZ=1 AngleXU=0 Radius=1.25 StartAngle=-5.3e-15 EndAngle=1.5708
    g311: LineSegment StartX=68.1392 StartY=109.07 StartZ=0 EndX=68.1392 EndY=96.0699 EndZ=0
    g312: ArcOfCircle CenterX=66.8892 CenterY=96.0699 CenterZ=0 NormalX=0 NormalY=0 NormalZ=1 AngleXU=0 Radius=1.25 StartAngle=4.71239 EndAngle=6.28319
    g313: LineSegment StartX=66.8892 StartY=94.8199 StartZ=0 EndX=53.8892 EndY=94.8199 EndZ=0
    g314: ArcOfCircle CenterX=53.8892 CenterY=96.0699 CenterZ=0 NormalX=0 NormalY=0 NormalZ=1 AngleXU=0 Radius=1.25 StartAngle=3.14159 EndAngle=4.71239
    g315: LineSegment StartX=52.6392 StartY=96.0699 StartZ=0 EndX=52.6392 EndY=109.07 EndZ=0
    g316: ArcOfCircle CenterX=53.8892 CenterY=109.07 CenterZ=0 NormalX=0 NormalY=0 NormalZ=1 AngleXU=0 Radius=1.25 StartAngle=1.5708 EndAngle=3.14159
    g317: LineSegment StartX=53.8892 StartY=110.32 StartZ=0 EndX=66.8892 EndY=110.32 EndZ=0
    g318: GeomPoint X=68.1392 Y=110.32 Z=0
    g319: GeomPoint X=52.6392 Y=94.8199 Z=0
    g320: ArcOfCircle CenterX=47.7946 CenterY=109.07 CenterZ=0 NormalX=0 NormalY=0 NormalZ=1 AngleXU=0 Radius=1.25 StartAngle=4e-16 EndAngle=1.5708
    g321: LineSegment StartX=49.0446 StartY=109.07 StartZ=0 EndX=49.0446 EndY=96.0699 EndZ=0
    g322: ArcOfCircle CenterX=47.7946 CenterY=96.0699 CenterZ=0 NormalX=0 NormalY=0 NormalZ=1 AngleXU=0 Radius=1.25 StartAngle=4.71239 EndAngle=6.28319
    g323: LineSegment StartX=47.7946 StartY=94.8199 StartZ=0 EndX=34.7946 EndY=94.8199 EndZ=0
    g324: ArcOfCircle CenterX=34.7946 CenterY=96.0699 CenterZ=0 NormalX=0 NormalY=0 NormalZ=1 AngleXU=0 Radius=1.25 StartAngle=3.14159 EndAngle=4.71239
    g325: LineSegment StartX=33.5446 StartY=96.0699 StartZ=0 EndX=33.5446 EndY=109.07 EndZ=0
    g326: ArcOfCircle CenterX=34.7946 CenterY=109.07 CenterZ=0 NormalX=0 NormalY=0 NormalZ=1 AngleXU=0 Radius=1.25 StartAngle=1.5708 EndAngle=3.14159
    g327: LineSegment StartX=34.7946 StartY=110.32 StartZ=0 EndX=47.7946 EndY=110.32 EndZ=0
    g328: GeomPoint X=49.0446 Y=110.32 Z=0
    g329: GeomPoint X=33.5446 Y=94.8199 Z=0
    g330: ArcOfCircle CenterX=28.7 CenterY=109.07 CenterZ=0 NormalX=0 NormalY=0 NormalZ=1 AngleXU=0 Radius=1.25 StartAngle=-9e-16 EndAngle=1.5708
    g331: LineSegment StartX=29.95 StartY=109.07 StartZ=0 EndX=29.95 EndY=96.0699 EndZ=0
    g332: ArcOfCircle CenterX=28.7 CenterY=96.0699 CenterZ=0 NormalX=0 NormalY=0 NormalZ=1 AngleXU=0 Radius=1.25 StartAngle=4.71239 EndAngle=6.28319
    g333: LineSegment StartX=28.7 StartY=94.8199 StartZ=0 EndX=10.7 EndY=94.8199 EndZ=0
    g334: ArcOfCircle CenterX=10.7 CenterY=96.0699 CenterZ=0 NormalX=0 NormalY=0 NormalZ=1 AngleXU=0 Radius=1.25 StartAngle=3.14159 EndAngle=4.71239
    g335: LineSegment StartX=9.45 StartY=96.0699 StartZ=0 EndX=9.45 EndY=109.07 EndZ=0
    g336: ArcOfCircle CenterX=10.7 CenterY=109.07 CenterZ=0 NormalX=0 NormalY=0 NormalZ=1 AngleXU=0 Radius=1.25 StartAngle=1.5708 EndAngle=3.14159
    g337: LineSegment StartX=10.7 StartY=110.32 StartZ=0 EndX=28.7 EndY=110.32 EndZ=0
    g338: GeomPoint X=29.95 Y=110.32 Z=0
    g339: GeomPoint X=9.45 Y=94.8199 Z=0
    g340: ArcOfCircle CenterX=10.7 CenterY=115.165 CenterZ=0 NormalX=0 NormalY=0 NormalZ=1 AngleXU=0 Radius=1.25 StartAngle=3.14159 EndAngle=4.71239
    g341: LineSegment StartX=9.45 StartY=115.165 StartZ=0 EndX=9.45 EndY=128.165 EndZ=0
    g342: ArcOfCircle CenterX=10.7 CenterY=128.165 CenterZ=0 NormalX=0 NormalY=0 NormalZ=1 AngleXU=0 Radius=1.25 StartAngle=1.5708 EndAngle=3.14159
    g343: LineSegment StartX=10.7 StartY=129.415 StartZ=0 EndX=47.6017 EndY=129.415 EndZ=0
    g344: ArcOfCircle CenterX=47.6017 CenterY=128.165 CenterZ=0 NormalX=0 NormalY=0 NormalZ=1 AngleXU=0 Radius=1.25 StartAngle=6.9e-15 EndAngle=1.5708
    g345: LineSegment StartX=48.8517 StartY=128.165 StartZ=0 EndX=48.8517 EndY=115.165 EndZ=0
    g346: ArcOfCircle CenterX=47.6017 CenterY=115.165 CenterZ=0 NormalX=0 NormalY=0 NormalZ=1 AngleXU=0 Radius=1.25 StartAngle=4.71239 EndAngle=6.28319
    g347: LineSegment StartX=47.6017 StartY=113.915 StartZ=0 EndX=10.7 EndY=113.915 EndZ=0
    g348: GeomPoint X=9.45 Y=113.915 Z=0
    g349: GeomPoint X=48.8517 Y=129.415 Z=0
    g350: ArcOfCircle CenterX=37.4196 CenterY=134.259 CenterZ=0 NormalX=0 NormalY=0 NormalZ=1 AngleXU=0 Radius=1.25 StartAngle=4.71239 EndAngle=6.28319
    g351: LineSegment StartX=37.4196 StartY=133.009 StartZ=0 EndX=10.7 EndY=133.009 EndZ=0
    g352: ArcOfCircle CenterX=10.7 CenterY=134.259 CenterZ=0 NormalX=0 NormalY=0 NormalZ=1 AngleXU=0 Radius=1.25 StartAngle=3.14159 EndAngle=4.71239
    g353: LineSegment StartX=9.45 StartY=134.259 StartZ=0 EndX=9.45 EndY=147.259 EndZ=0
    g354: ArcOfCircle CenterX=10.7 CenterY=147.259 CenterZ=0 NormalX=0 NormalY=0 NormalZ=1 AngleXU=0 Radius=1.25 StartAngle=1.5708 EndAngle=3.14159
    g355: LineSegment StartX=10.7 StartY=148.509 StartZ=0 EndX=37.4196 EndY=148.509 EndZ=0
    g356: ArcOfCircle CenterX=37.4196 CenterY=147.259 CenterZ=0 NormalX=0 NormalY=0 NormalZ=1 AngleXU=0 Radius=1.25 StartAngle=8.1e-15 EndAngle=1.5708
    g357: LineSegment StartX=38.6696 StartY=147.259 StartZ=0 EndX=38.6696 EndY=134.259 EndZ=0
    g358: GeomPoint X=38.6696 Y=133.009 Z=0
    g359: GeomPoint X=9.45 Y=148.509 Z=0
    g360: ArcOfCircle CenterX=32.7 CenterY=153.354 CenterZ=0 NormalX=0 NormalY=0 NormalZ=1 AngleXU=0 Radius=1.25 StartAngle=4.71239 EndAngle=6.28319
    g361: LineSegment StartX=32.7 StartY=152.104 StartZ=0 EndX=10.7 EndY=152.104 EndZ=0
    g362: ArcOfCircle CenterX=10.7 CenterY=153.354 CenterZ=0 NormalX=0 NormalY=0 NormalZ=1 AngleXU=0 Radius=1.25 StartAngle=3.14159 EndAngle=4.71239
    g363: LineSegment StartX=9.45 StartY=153.354 StartZ=0 EndX=9.45 EndY=166.354 EndZ=0
    g364: ArcOfCircle CenterX=10.7 CenterY=166.354 CenterZ=0 NormalX=0 NormalY=0 NormalZ=1 AngleXU=0 Radius=1.25 StartAngle=1.5708 EndAngle=3.14159
    g365: LineSegment StartX=10.7 StartY=167.604 StartZ=0 EndX=32.7 EndY=167.604 EndZ=0
    g366: ArcOfCircle CenterX=32.7 CenterY=166.354 CenterZ=0 NormalX=0 NormalY=0 NormalZ=1 AngleXU=0 Radius=1.25 StartAngle=-2.7e-15 EndAngle=1.5708
    g367: LineSegment StartX=33.95 StartY=166.354 StartZ=0 EndX=33.95 EndY=153.354 EndZ=0
    g368: GeomPoint X=33.95 Y=152.104 Z=0
    g369: GeomPoint X=9.45 Y=167.604 Z=0
    g370: ArcOfCircle CenterX=10.7 CenterY=172.448 CenterZ=0 NormalX=0 NormalY=0 NormalZ=1 AngleXU=0 Radius=1.25 StartAngle=3.14159 EndAngle=4.71239
    g371: LineSegment StartX=9.45 StartY=172.448 StartZ=0 EndX=9.45 EndY=185.448 EndZ=0
    g372: ArcOfCircle CenterX=10.7 CenterY=185.448 CenterZ=0 NormalX=0 NormalY=0 NormalZ=1 AngleXU=0 Radius=1.25 StartAngle=1.5708 EndAngle=3.14159
    g373: LineSegment StartX=10.7 StartY=186.698 StartZ=0 EndX=23.7 EndY=186.698 EndZ=0
    g374: ArcOfCircle CenterX=23.7 CenterY=185.448 CenterZ=0 NormalX=0 NormalY=0 NormalZ=1 AngleXU=0 Radius=1.25 StartAngle=-8.9e-15 EndAngle=1.5708
    g375: LineSegment StartX=24.95 StartY=185.448 StartZ=0 EndX=24.95 EndY=172.448 EndZ=0
    g376: ArcOfCircle CenterX=23.7 CenterY=172.448 CenterZ=0 NormalX=0 NormalY=0 NormalZ=1 AngleXU=0 Radius=1.25 StartAngle=4.71239 EndAngle=6.28319
    g377: LineSegment StartX=23.7 StartY=171.198 StartZ=0 EndX=10.7 EndY=171.198 EndZ=0
    g378: GeomPoint X=9.45 Y=171.198 Z=0
    g379: GeomPoint X=24.95 Y=186.698 Z=0
    g380: LineSegment StartX=29.95 StartY=109.07 StartZ=0 EndX=33.5446 EndY=109.07 EndZ=0
    g381: LineSegment StartX=49.0446 StartY=109.07 StartZ=0 EndX=52.6392 EndY=109.07 EndZ=0
    g382: LineSegment StartX=68.1392 StartY=109.07 StartZ=0 EndX=71.7338 EndY=109.07 EndZ=0
    g383: LineSegment StartX=87.2338 StartY=109.07 StartZ=0 EndX=90.8285 EndY=109.07 EndZ=0
    g384: LineSegment StartX=246.335 StartY=109.07 StartZ=0 EndX=242.741 EndY=109.07 EndZ=0
    g385: LineSegment StartX=224.116 StartY=109.07 StartZ=0 EndX=220.521 EndY=109.07 EndZ=0
    g386: LineSegment StartX=201.427 StartY=109.07 StartZ=0 EndX=205.021 EndY=109.07 EndZ=0
    g387: LineSegment StartX=182.332 StartY=109.07 StartZ=0 EndX=185.927 EndY=109.07 EndZ=0
    g388: LineSegment StartX=264.96 StartY=109.07 StartZ=0 EndX=268.555 EndY=109.07 EndZ=0
    g389: ArcOfCircle CenterX=225.548 CenterY=128.165 CenterZ=0 NormalX=0 NormalY=0 NormalZ=1 AngleXU=0 Radius=1.25 StartAngle=1.5708 EndAngle=3.14159
    g390: LineSegment StartX=225.548 StartY=129.415 StartZ=0 EndX=238.548 EndY=129.415 EndZ=0
    g391: ArcOfCircle CenterX=238.548 CenterY=128.165 CenterZ=0 NormalX=0 NormalY=0 NormalZ=1 AngleXU=0 Radius=1.25 StartAngle=4e-16 EndAngle=1.5708
    g392: LineSegment StartX=239.798 StartY=128.165 StartZ=0 EndX=239.798 EndY=115.165 EndZ=0
    g393: ArcOfCircle CenterX=238.548 CenterY=115.165 CenterZ=0 NormalX=0 NormalY=0 NormalZ=1 AngleXU=0 Radius=1.25 StartAngle=4.71239 EndAngle=6.28319
    g394: LineSegment StartX=238.548 StartY=113.915 StartZ=0 EndX=225.548 EndY=113.915 EndZ=0
    g395: ArcOfCircle CenterX=225.548 CenterY=115.165 CenterZ=0 NormalX=0 NormalY=0 NormalZ=1 AngleXU=0 Radius=1.25 StartAngle=3.14159 EndAngle=4.71239
    g396: LineSegment StartX=224.298 StartY=115.165 StartZ=0 EndX=224.298 EndY=128.165 EndZ=0
    g397: GeomPoint X=224.298 Y=129.415 Z=0
    g398: GeomPoint X=239.798 Y=113.915 Z=0
    g399: ArcOfCircle CenterX=206.453 CenterY=128.165 CenterZ=0 NormalX=0 NormalY=0 NormalZ=1 AngleXU=0 Radius=1.25 StartAngle=1.5708 EndAngle=3.14159
    ... +489 more geometry lines
  constraints (2112):
    c: Tangent(g0,g1) = 1.5708
    c: Tangent(g1,g2) = 1.5708
    c: Tangent(g2,g3) = 1.5708
    c: Coincident(g13,g4) = 1.5708
    c: Tangent(g4,g5) = 1.5708
    c: Tangent(g5,g6) = 1.5708
    c: Tangent(g6,g7) = 1.5708
    c: Tangent(g7,g0) = 1.5708
    c: Horizontal(g3)
    c: Horizontal(g7)
    c: Vertical(g1)
    c: Vertical(g5)
    c: Equal(g0,g2)
    c: Equal(g2,g4)
    c: Equal(g4,g6)
    c: PointOnObject(g8,g1)
    c: PointOnObject(g8,g7)
    c: PointOnObject(g9,g3)
    c: PointOnObject(g9,g5)
    c: Coincident(g8,g-1)
    c: DistanceY(g8,g2) = 228.98
    c: DistanceX(g8,g5) = 296.63
    c: Radius(g4) = 7
    c: Horizontal(g10)
    c: DistanceX(g10,g4) = 18.25
    c: Coincident(g11,g10)
    c: Vertical(g11)
    c: DistanceY(g10,g11) = 12.7495
    c: Coincident(g12,g10)
    c: Vertical(g12)
    c: Coincident(g3,g12)
    c: Coincident(g13,g11)
    c: Equal(g3,g13)
    c: Equal(g1,g5)
    c: Horizontal(g13)
    c: Tangent(g14,g15) = 1.5708
    c: Tangent(g15,g16) = 1.5708
    c: Tangent(g16,g17) = 1.5708
    c: Tangent(g17,g18) = 1.5708
    c: Tangent(g18,g19) = 1.5708
    c: Tangent(g19,g20) = 1.5708
    c: Tangent(g20,g21) = 1.5708
    c: Tangent(g21,g14) = 1.5708
    c: Horizontal(g17)
    c: Horizontal(g21)
    c: Vertical(g15)
    c: Vertical(g19)
    c: Equal(g14,g16)
    c: Equal(g16,g18)
    c: Equal(g18,g20)
    c: PointOnObject(g22,g15)
    c: PointOnObject(g22,g21)
    c: PointOnObject(g23,g17)
    c: PointOnObject(g23,g19)
    c: DistanceY(g16,g14) = 77
    c: DistanceX(g18,g15) = 115
    c: Radius(g14) = 3
    c: DistanceY(g6,g16) = 9.5
    c: Coincident(g24,g14)
    c: PointOnObject(g24,g5)
    c: Horizontal(g24)
    c: Coincident(g25,g19)
    c: PointOnObject(g25,g1)
    c: Horizontal(g25)
    c: Equal(g25,g24)
    c: Coincident(g26,g27)
    c: Coincident(g27,g28)
    c: Coincident(g28,g29)
    c: Coincident(g29,g26)
    c: Horizontal(g26)
    c: Horizontal(g28)
    c: Vertical(g27)
    c: Vertical(g29)
    c: Coincident(g30,g26)
    c: PointOnObject(g30,g5)
    c: Horizontal(g30)
    c: Coincident(g31,g26)
    c: PointOnObject(g31,g1)
    c: Horizontal(g31)
    c: DistanceX(g30,g30) = 9.45
    c: Equal(g30,g31)
    c: DistanceY(g26,g10) = 16.25
    c: PointOnObject(g32,g29)
    c: PointOnObject(g32,g27)
    c: Horizontal(g32)
    c: DistanceY(g32,g26) = 9.6875
    c: Tangent(g33,g34) = 1.5708
    c: Tangent(g34,g35) = 1.5708
    c: Tangent(g35,g36) = 1.5708
    c: Tangent(g36,g37) = 1.5708
    c: Tangent(g37,g38) = 1.5708
    c: Tangent(g38,g39) = 1.5708
    c: Tangent(g39,g40) = 1.5708
    c: Tangent(g40,g33) = 1.5708
    c: Horizontal(g34)
    c: Horizontal(g38)
    c: Vertical(g36)
    c: Vertical(g40)
    c: Equal(g33,g35)
    c: Equal(g35,g37)
    c: Equal(g37,g39)
    c: PointOnObject(g41,g34)
    c: PointOnObject(g41,g40)
    c: PointOnObject(g42,g36)
    c: PointOnObject(g42,g38)
    c: Coincident(g41,g26)
    c: PointOnObject(g42,g32)
    c: Tangent(g43,g44) = 1.5708
    c: Tangent(g44,g45) = 1.5708
    c: Tangent(g45,g46) = 1.5708
    c: Tangent(g46,g47) = 1.5708
    c: Tangent(g47,g48) = 1.5708
    c: Tangent(g48,g49) = 1.5708
    c: Tangent(g49,g50) = 1.5708
    c: Tangent(g50,g43) = 1.5708
    c: Horizontal(g44)
    c: Horizontal(g48)
    c: Vertical(g46)
    c: Vertical(g50)
    c: Equal(g43,g45)
    c: Equal(g45,g47)
    c: Equal(g47,g49)
    c: PointOnObject(g51,g44)
    c: PointOnObject(g51,g50)
    c: PointOnObject(g52,g46)
    c: PointOnObject(g52,g48)
    c: PointOnObject(g51,g26)
    c: PointOnObject(g52,g32)
    c: Tangent(g53,g54) = 1.5708
    c: Tangent(g54,g55) = 1.5708
    c: Tangent(g55,g56) = 1.5708
    c: Tangent(g56,g57) = 1.5708
    c: Tangent(g57,g58) = 1.5708
    c: Tangent(g58,g59) = 1.5708
    c: Tangent(g59,g60) = 1.5708
    c: Tangent(g60,g53) = 1.5708
    c: Horizontal(g54)
    c: Horizontal(g58)
    c: Vertical(g56)
    c: Vertical(g60)
    c: Equal(g53,g55)
    c: Equal(g55,g57)
    c: Equal(g57,g59)
    c: PointOnObject(g61,g54)
    c: PointOnObject(g61,g60)
    c: PointOnObject(g62,g56)
    c: PointOnObject(g62,g58)
    c: PointOnObject(g61,g26)
    c: PointOnObject(g62,g32)
    c: Tangent(g63,g64) = 1.5708
    c: Tangent(g64,g65) = 1.5708
    c: Tangent(g65,g66) = 1.5708
    c: Tangent(g66,g67) = 1.5708
    c: Tangent(g67,g68) = 1.5708
    c: Tangent(g68,g69) = 1.5708
    c: Tangent(g69,g70) = 1.5708
    c: Tangent(g70,g63) = 1.5708
    c: Horizontal(g64)
    c: Horizontal(g68)
    c: Vertical(g66)
    c: Vertical(g70)
    c: Equal(g63,g65)
    c: Equal(g65,g67)
    c: Equal(g67,g69)
    c: PointOnObject(g71,g64)
    c: PointOnObject(g71,g70)
    c: PointOnObject(g72,g66)
    c: PointOnObject(g72,g68)
    c: PointOnObject(g71,g26)
    c: PointOnObject(g72,g32)
    c: Tangent(g73,g74) = 1.5708
    c: Tangent(g74,g75) = 1.5708
    c: Tangent(g75,g76) = 1.5708
    c: Tangent(g76,g77) = 1.5708
    c: Tangent(g77,g78) = 1.5708
    c: Tangent(g78,g79) = 1.5708
    c: Tangent(g79,g80) = 1.5708
    c: Tangent(g80,g73) = 1.5708
    c: Horizontal(g74)
    c: Horizontal(g78)
    c: Vertical(g76)
    c: Vertical(g80)
    c: Equal(g73,g75)
    c: Equal(g75,g77)
    c: Equal(g77,g79)
    c: PointOnObject(g81,g74)
    c: PointOnObject(g81,g80)
    c: PointOnObject(g82,g76)
    c: PointOnObject(g82,g78)
    c: PointOnObject(g81,g26)
    c: PointOnObject(g82,g32)
    c: Tangent(g83,g84) = 1.5708
    c: Tangent(g84,g85) = 1.5708
    c: Tangent(g85,g86) = 1.5708
    c: Tangent(g86,g87) = 1.5708
    c: Tangent(g87,g88) = 1.5708
    c: Tangent(g88,g89) = 1.5708
    c: Tangent(g89,g90) = 1.5708
    c: Tangent(g90,g83) = 1.5708
    c: Horizontal(g84)
    c: Horizontal(g88)
    c: Vertical(g86)
    c: Vertical(g90)
    c: Equal(g83,g85)
    c: Equal(g85,g87)
    c: Equal(g87,g89)
    c: PointOnObject(g91,g84)
    c: PointOnObject(g91,g90)
    c: PointOnObject(g92,g86)
    c: PointOnObject(g92,g88)
    c: PointOnObject(g91,g26)
    c: PointOnObject(g92,g32)
    c: Tangent(g93,g94) = 1.5708
    c: Tangent(g94,g95) = 1.5708
    c: Tangent(g95,g96) = 1.5708
    c: Tangent(g96,g97) = 1.5708
    c: Tangent(g97,g98) = 1.5708
    c: Tangent(g98,g99) = 1.5708
    c: Tangent(g99,g100) = 1.5708
    c: Tangent(g100,g93) = 1.5708
    c: Horizontal(g94)
    c: Horizontal(g98)
    c: Vertical(g96)
    c: Vertical(g100)
    c: Equal(g93,g95)
    c: Equal(g95,g97)
    c: Equal(g97,g99)
    c: PointOnObject(g101,g94)
    c: PointOnObject(g101,g100)
    c: PointOnObject(g102,g96)
    c: PointOnObject(g102,g98)
    c: PointOnObject(g101,g26)
    c: PointOnObject(g102,g32)
    c: Tangent(g103,g104) = 1.5708
    c: Tangent(g104,g105) = 1.5708
    c: Tangent(g105,g106) = 1.5708
    c: Tangent(g106,g107) = 1.5708
    c: Tangent(g107,g108) = 1.5708
    c: Tangent(g108,g109) = 1.5708
    c: Tangent(g109,g110) = 1.5708
    c: Tangent(g110,g103) = 1.5708
    c: Horizontal(g106)
    c: Horizontal(g110)
    c: Vertical(g104)
    c: Vertical(g108)
    c: Equal(g103,g105)
    c: Equal(g105,g107)
    c: Equal(g107,g109)
    c: PointOnObject(g111,g104)
    c: PointOnObject(g111,g110)
    c: PointOnObject(g112,g106)
    c: PointOnObject(g112,g108)
    c: PointOnObject(g111,g32)
    c: PointOnObject(g112,g26)
    c: Tangent(g113,g114) = 1.5708
    c: Tangent(g114,g115) = 1.5708
    c: Tangent(g115,g116) = 1.5708
    c: Tangent(g116,g117) = 1.5708
    c: Tangent(g117,g118) = 1.5708
    c: Tangent(g118,g119) = 1.5708
    c: Tangent(g119,g120) = 1.5708
    c: Tangent(g120,g113) = 1.5708
    c: Horizontal(g114)
    c: Horizontal(g118)
    c: Vertical(g116)
    c: Vertical(g120)
    c: Equal(g113,g115)
    c: Equal(g115,g117)
    c: Equal(g117,g119)
    c: PointOnObject(g121,g114)
    c: PointOnObject(g121,g120)
    c: PointOnObject(g122,g116)
    c: PointOnObject(g122,g118)
    c: PointOnObject(g121,g26)
    c: PointOnObject(g122,g32)
    c: Tangent(g123,g124) = 1.5708
    c: Tangent(g124,g125) = 1.5708
    c: Tangent(g125,g126) = 1.5708
    c: Tangent(g126,g127) = 1.5708
    c: Tangent(g127,g128) = 1.5708
    c: Tangent(g128,g129) = 1.5708
    c: Tangent(g129,g130) = 1.5708
    c: Tangent(g130,g123) = 1.5708
    c: Horizontal(g124)
    c: Horizontal(g128)
    c: Vertical(g126)
    c: Vertical(g130)
    c: Equal(g123,g125)
    c: Equal(g125,g127)
    c: Equal(g127,g129)
    c: PointOnObject(g131,g124)
    c: PointOnObject(g131,g130)
    c: PointOnObject(g132,g126)
    c: PointOnObject(g132,g128)
    c: PointOnObject(g131,g26)
    c: PointOnObject(g132,g32)
    c: Tangent(g133,g134) = 1.5708
    c: Tangent(g134,g135) = 1.5708
    c: Tangent(g135,g136) = 1.5708
    c: Tangent(g136,g137) = 1.5708
    c: Tangent(g137,g138) = 1.5708
    c: Tangent(g138,g139) = 1.5708
    c: Tangent(g139,g140) = 1.5708
    c: Tangent(g140,g133) = 1.5708
    c: Horizontal(g134)
    c: Horizontal(g138)
    c: Vertical(g136)
    c: Vertical(g140)
    c: Equal(g133,g135)
    c: Equal(g135,g137)
    c: Equal(g137,g139)
    c: PointOnObject(g141,g134)
    c: PointOnObject(g141,g140)
    c: PointOnObject(g142,g136)
    c: PointOnObject(g142,g138)
    c: PointOnObject(g141,g26)
    c: PointOnObject(g142,g32)
    c: Tangent(g143,g144) = 1.5708
    c: Tangent(g144,g145) = 1.5708
    c: Tangent(g145,g146) = 1.5708
    c: Tangent(g146,g147) = 1.5708
    c: Tangent(g147,g148) = 1.5708
    c: Tangent(g148,g149) = 1.5708
    c: Tangent(g149,g150) = 1.5708
    c: Tangent(g150,g143) = 1.5708
    c: Horizontal(g146)
    c: Horizontal(g150)
    c: Vertical(g144)
    c: Vertical(g148)
    c: Equal(g143,g145)
    c: Equal(g145,g147)
    c: Equal(g147,g149)
    c: PointOnObject(g151,g144)
    c: PointOnObject(g151,g150)
    c: PointOnObject(g152,g146)
    c: PointOnObject(g152,g148)
    c: Coincident(g151,g26)
    c: PointOnObject(g152,g32)
    c: Tangent(g153,g154) = 1.5708
    c: Tangent(g154,g155) = 1.5708
    c: Tangent(g155,g156) = 1.5708
    c: Tangent(g156,g157) = 1.5708
    c: Tangent(g157,g158) = 1.5708
    c: Tangent(g158,g159) = 1.5708
    c: Tangent(g159,g160) = 1.5708
    c: Tangent(g160,g153) = 1.5708
    c: Horizontal(g154)
    c: Horizontal(g158)
    c: Vertical(g156)
    c: Vertical(g160)
    c: Equal(g153,g155)
    c: Equal(g155,g157)
    c: Equal(g157,g159)
    c: PointOnObject(g161,g154)
    c: PointOnObject(g161,g160)
    c: PointOnObject(g162,g156)
    c: PointOnObject(g162,g158)
    c: PointOnObject(g161,g26)
    c: PointOnObject(g162,g32)
    c: Tangent(g163,g164) = 1.5708
    c: Tangent(g164,g165) = 1.5708
    c: Tangent(g165,g166) = 1.5708
    c: Tangent(g166,g167) = 1.5708
    c: Tangent(g167,g168) = 1.5708
    c: Tangent(g168,g169) = 1.5708
    c: Tangent(g169,g170) = 1.5708
    c: Tangent(g170,g163) = 1.5708
    c: Horizontal(g164)
    c: Horizontal(g168)
    c: Vertical(g166)
    c: Vertical(g170)
    c: Equal(g163,g165)
    c: Equal(g165,g167)
    c: Equal(g167,g169)
    c: PointOnObject(g171,g164)
    c: PointOnObject(g171,g170)
    c: PointOnObject(g172,g166)
    c: PointOnObject(g172,g168)
    c: PointOnObject(g171,g26)
    c: PointOnObject(g172,g32)
    c: Coincident(g173,g148)
    c: Coincident(g174,g163)
    c: Coincident(g174,g155)
    c: Horizontal(g174)
    c: Coincident(g175,g153)
    c: Coincident(g175,g135)
    c: Horizontal(g175)
    c: Coincident(g176,g133)
    c: Coincident(g176,g125)
    c: Horizontal(g176)
    c: Coincident(g177,g123)
    c: Coincident(g177,g115)
    c: Horizontal(g177)
    c: Coincident(g178,g113)
    c: Coincident(g178,g107)
    c: Horizontal(g178)
    c: Coincident(g179,g104)
    c: Coincident(g179,g95)
    c: Horizontal(g179)
    c: Coincident(g180,g93)
    c: Coincident(g180,g85)
    c: Horizontal(g180)
    c: Coincident(g181,g83)
    c: Coincident(g181,g75)
    c: Horizontal(g181)
    c: Coincident(g182,g73)
    c: Coincident(g182,g65)
    c: Horizontal(g182)
    c: Coincident(g183,g53)
    c: Coincident(g183,g45)
    c: Horizontal(g183)
    c: Coincident(g184,g43)
    c: Coincident(g184,g35)
    c: Horizontal(g184)
    c: Equal(g184,g173)
    c: Equal(g183,g173)
    c: Equal(g182,g173)
    c: Equal(g181,g173)
    c: Equal(g180,g173)
    c: Equal(g179,g173)
    c: Equal(g178,g173)
    c: Equal(g177,g173)
    c: Equal(g176,g173)
    c: Equal(g175,g173)
    c: Equal(g174,g173)
    c: Radius(g143) = 1.25
    c: DistanceX(g147,g144) = 22.5
    c: DistanceX(g169,g166) = 15.5
    c: Equal(g164,g154)
    c: Equal(g164,g134)
    c: Equal(g164,g124)
    c: Equal(g114,g164)
    c: Equal(g106,g164)
    c: Equal(g164,g94)
    c: Equal(g84,g164)
    c: Equal(g74,g164)
    c: Equal(g64,g164)
    c: Equal(g54,g164)
    c: Equal(g44,g164)
    c: Coincident(g165,g173)
    c: Coincident(g185,g63)
    c: Coincident(g185,g55)
    c: Horizontal(g185)
    c: Equal(g185,g173)
    c: Horizontal(g173)
    c: Equal(g34,g150)
    c: PointOnObject(g186,g27)
    c: PointOnObject(g186,g29)
    c: Horizontal(g186)
    c: PointOnObject(g187,g29)
    c: PointOnObject(g187,g27)
    c: Horizontal(g187)
    c: PointOnObject(g188,g27)
    c: PointOnObject(g188,g29)
    c: Horizontal(g188)
    c: PointOnObject(g189,g29)
    c: PointOnObject(g189,g27)
    c: Horizontal(g189)
    c: PointOnObject(g190,g27)
    c: PointOnObject(g190,g29)
    c: Horizontal(g190)
    c: PointOnObject(g191,g29)
    c: PointOnObject(g191,g27)
    c: Horizontal(g191)
    c: PointOnObject(g192,g27)
    c: PointOnObject(g192,g29)
    c: Horizontal(g192)
    c: PointOnObject(g193,g27)
    c: PointOnObject(g193,g29)
    c: Horizontal(g193)
    c: PointOnObject(g194,g27)
    c: PointOnObject(g194,g29)
    c: Horizontal(g194)
    c: Tangent(g195,g196) = 1.5708
    c: Tangent(g196,g197) = 1.5708
    c: Tangent(g197,g198) = 1.5708
    c: Tangent(g198,g199) = 1.5708
    c: Tangent(g199,g200) = 1.5708
    c: Tangent(g200,g201) = 1.5708
    c: Tangent(g201,g202) = 1.5708
    c: Tangent(g202,g195) = 1.5708
    c: Horizontal(g196)
    c: Horizontal(g200)
    c: Vertical(g198)
    c: Vertical(g202)
    c: Equal(g195,g197)
    c: Equal(g197,g199)
    c: Equal(g199,g201)
    c: PointOnObject(g203,g196)
    c: PointOnObject(g203,g202)
    c: PointOnObject(g204,g198)
    c: PointOnObject(g204,g200)
    c: Coincident(g203,g187)
    c: PointOnObject(g204,g186)
    c: Tangent(g205,g206) = 1.5708
    c: Tangent(g206,g207) = 1.5708
    c: Tangent(g207,g208) = 1.5708
    c: Tangent(g208,g209) = 1.5708
    c: Tangent(g209,g210) = 1.5708
    c: Tangent(g210,g211) = 1.5708
    c: Tangent(g211,g212) = 1.5708
    c: Tangent(g212,g205) = 1.5708
    c: Horizontal(g206)
    c: Horizontal(g210)
    c: Vertical(g208)
    c: Vertical(g212)
    c: Equal(g205,g207)
    c: Equal(g207,g209)
    c: Equal(g209,g211)
    c: PointOnObject(g213,g206)
    c: PointOnObject(g213,g212)
    c: PointOnObject(g214,g208)
    c: PointOnObject(g214,g210)
    c: Coincident(g213,g189)
    c: PointOnObject(g214,g188)
    c: Tangent(g215,g216) = 1.5708
    c: Tangent(g216,g217) = 1.5708
    c: Tangent(g217,g218) = 1.5708
    c: Tangent(g218,g219) = 1.5708
    c: Tangent(g219,g220) = 1.5708
    c: Tangent(g220,g221) = 1.5708
    c: Tangent(g221,g222) = 1.5708
    c: Tangent(g222,g215) = 1.5708
    c: Horizontal(g216)
    c: Horizontal(g220)
    c: Vertical(g218)
    c: Vertical(g222)
    c: Equal(g215,g217)
    c: Equal(g217,g219)
    c: Equal(g219,g221)
    c: PointOnObject(g223,g216)
    c: PointOnObject(g223,g222)
    c: PointOnObject(g224,g218)
    c: PointOnObject(g224,g220)
    c: PointOnObject(g223,g190)
    c: Coincident(g224,g191)
    c: Tangent(g225,g226) = 1.5708
    c: Tangent(g226,g227) = 1.5708
    c: Tangent(g227,g228) = 1.5708
    c: Tangent(g228,g229) = 1.5708
    c: Tangent(g229,g230) = 1.5708
    c: Tangent(g230,g231) = 1.5708
    c: Tangent(g231,g232) = 1.5708
    c: Tangent(g232,g225) = 1.5708
    c: Horizontal(g226)
    c: Horizontal(g230)
    c: Vertical(g228)
    c: Vertical(g232)
    c: Equal(g225,g227)
    c: Equal(g227,g229)
    c: Equal(g229,g231)
    c: PointOnObject(g233,g226)
    c: PointOnObject(g233,g232)
    c: PointOnObject(g234,g228)
    c: PointOnObject(g234,g230)
    c: PointOnObject(g233,g192)
    c: Coincident(g234,g193)
    c: Tangent(g235,g236) = 1.5708
    c: Tangent(g236,g237) = 1.5708
    c: Tangent(g237,g238) = 1.5708
    c: Tangent(g238,g239) = 1.5708
    c: Tangent(g239,g240) = 1.5708
    c: Tangent(g240,g241) = 1.5708
    c: Tangent(g241,g242) = 1.5708
    c: Tangent(g242,g235) = 1.5708
    c: Horizontal(g236)
    c: Horizontal(g240)
    c: Vertical(g238)
    c: Vertical(g242)
    c: Equal(g235,g237)
    c: Equal(g237,g239)
    c: Equal(g239,g241)
    c: PointOnObject(g243,g236)
    c: PointOnObject(g243,g242)
    c: PointOnObject(g244,g238)
    c: PointOnObject(g244,g240)
    c: PointOnObject(g243,g194)
    c: Coincident(g244,g27)
    c: Coincident(g245,g236)
    c: Coincident(g245,g229)
    c: Vertical(g245)
    c: Coincident(g246,g226)
    c: Coincident(g246,g219)
    c: Vertical(g246)
    c: Coincident(g247,g216)
    c: Coincident(g247,g205)
    c: Vertical(g247)
    c: Coincident(g248,g210)
    c: Coincident(g248,g195)
    c: Vertical(g248)
    c: Coincident(g249,g200)
    c: Coincident(g249,g145)
    c: Vertical(g249)
    c: Equal(g249,g173)
    c: Equal(g202,g164)
    c: Equal(g212,g164)
    c: Equal(g218,g164)
    c: Equal(g228,g164)
    c: Equal(g238,g164)
    c: Equal(g245,g249)
    c: Equal(g249,g248)
    c: Equal(g247,g249)
    c: Equal(g249,g246)
    c: DistanceX(g241,g238) = 18.625
    c: DistanceX(g197,g195) = 29.5
    c: DistanceX(g207,g205) = 20.5
    c: Tangent(g250,g251) = 1.5708
    c: Tangent(g251,g252) = 1.5708
    c: Tangent(g252,g253) = 1.5708
    c: Tangent(g253,g254) = 1.5708
    c: Tangent(g254,g255) = 1.5708
    c: Tangent(g255,g256) = 1.5708
    c: Tangent(g256,g257) = 1.5708
    c: Tangent(g257,g250) = 1.5708
    c: Horizontal(g253)
    c: Horizontal(g257)
    c: Vertical(g251)
    c: Vertical(g255)
    c: Equal(g250,g252)
    c: Equal(g252,g254)
    c: Equal(g254,g256)
    c: PointOnObject(g258,g251)
    c: PointOnObject(g258,g257)
    c: PointOnObject(g259,g253)
    c: PointOnObject(g259,g255)
    c: PointOnObject(g258,g194)
    c: PointOnObject(g259,g28)
    c: Tangent(g260,g261) = 1.5708
    c: Tangent(g261,g262) = 1.5708
    c: Tangent(g262,g263) = 1.5708
    c: Tangent(g263,g264) = 1.5708
    c: Tangent(g264,g265) = 1.5708
    c: Tangent(g265,g266) = 1.5708
    c: Tangent(g266,g267) = 1.5708
    c: Tangent(g267,g260) = 1.5708
    c: Horizontal(g263)
    c: Horizontal(g267)
    c: Vertical(g261)
    c: Vertical(g265)
    c: Equal(g260,g262)
    c: Equal(g262,g264)
    c: Equal(g264,g266)
    c: PointOnObject(g268,g261)
    c: PointOnObject(g268,g267)
    c: PointOnObject(g269,g263)
    c: PointOnObject(g269,g265)
    c: PointOnObject(g268,g194)
    c: PointOnObject(g269,g28)
    c: Tangent(g270,g271) = 1.5708
    c: Tangent(g271,g272) = 1.5708
    c: Tangent(g272,g273) = 1.5708
    c: Tangent(g273,g274) = 1.5708
    c: Tangent(g274,g275) = 1.5708
    c: Tangent(g275,g276) = 1.5708
    c: Tangent(g276,g277) = 1.5708
    c: Tangent(g277,g270) = 1.5708
    c: Horizontal(g273)
    c: Horizontal(g277)
    c: Vertical(g271)
    c: Vertical(g275)
    c: Equal(g270,g272)
    c: Equal(g272,g274)
    c: Equal(g274,g276)
    c: PointOnObject(g278,g271)
    c: PointOnObject(g278,g277)
    c: PointOnObject(g279,g273)
    c: PointOnObject(g279,g275)
    c: PointOnObject(g278,g194)
    c: PointOnObject(g279,g28)
    c: Tangent(g280,g281) = 1.5708
    c: Tangent(g281,g282) = 1.5708
    c: Tangent(g282,g283) = 1.5708
    c: Tangent(g283,g284) = 1.5708
    c: Tangent(g284,g285) = 1.5708
    c: Tangent(g285,g286) = 1.5708
    c: Tangent(g286,g287) = 1.5708
    c: Tangent(g287,g280) = 1.5708
    c: Horizontal(g283)
    c: Horizontal(g287)
    c: Vertical(g281)
    c: Vertical(g285)
    c: Equal(g280,g282)
    c: Equal(g282,g284)
    c: Equal(g284,g286)
    c: PointOnObject(g288,g281)
    c: PointOnObject(g288,g287)
    c: PointOnObject(g289,g283)
    c: PointOnObject(g289,g285)
    c: PointOnObject(g288,g194)
    c: PointOnObject(g289,g28)
    c: Tangent(g290,g291) = 1.5708
    c: Tangent(g291,g292) = 1.5708
    c: Tangent(g292,g293) = 1.5708
    c: Tangent(g293,g294) = 1.5708
    c: Tangent(g294,g295) = 1.5708
    c: Tangent(g295,g296) = 1.5708
    c: Tangent(g296,g297) = 1.5708
    c: Tangent(g297,g290) = 1.5708
    c: Horizontal(g293)
    c: Horizontal(g297)
    c: Vertical(g291)
    c: Vertical(g295)
    c: Equal(g290,g292)
    c: Equal(g292,g294)
    c: Equal(g294,g296)
    c: PointOnObject(g298,g291)
    c: PointOnObject(g298,g297)
    c: PointOnObject(g299,g293)
    c: PointOnObject(g299,g295)
    c: PointOnObject(g298,g194)
    c: PointOnObject(g299,g28)
    c: Tangent(g300,g301) = 1.5708
    c: Tangent(g301,g302) = 1.5708
    c: Tangent(g302,g303) = 1.5708
    c: Tangent(g303,g304) = 1.5708
    c: Tangent(g304,g305) = 1.5708
    c: Tangent(g305,g306) = 1.5708
    c: Tangent(g306,g307) = 1.5708
    c: Tangent(g307,g300) = 1.5708
    c: Horizontal(g303)
    c: Horizontal(g307)
    c: Vertical(g301)
    c: Vertical(g305)
    c: Equal(g300,g302)
    c: Equal(g302,g304)
    c: Equal(g304,g306)
    c: PointOnObject(g308,g301)
    c: PointOnObject(g308,g307)
    c: PointOnObject(g309,g303)
    c: PointOnObject(g309,g305)
    c: PointOnObject(g308,g194)
    c: PointOnObject(g309,g28)
    c: Tangent(g310,g311) = 1.5708
    c: Tangent(g311,g312) = 1.5708
    c: Tangent(g312,g313) = 1.5708
    c: Tangent(g313,g314) = 1.5708
    c: Tangent(g314,g315) = 1.5708
    c: Tangent(g315,g316) = 1.5708
    c: Tangent(g316,g317) = 1.5708
    c: Tangent(g317,g310) = 1.5708
    c: Horizontal(g313)
    c: Horizontal(g317)
    c: Vertical(g311)
    c: Vertical(g315)
    c: Equal(g310,g312)
    c: Equal(g312,g314)
    c: Equal(g314,g316)
    c: PointOnObject(g318,g311)
    c: PointOnObject(g318,g317)
    c: PointOnObject(g319,g313)
    c: PointOnObject(g319,g315)
    c: PointOnObject(g318,g194)
    c: PointOnObject(g319,g28)
    c: Tangent(g320,g321) = 1.5708
    c: Tangent(g321,g322) = 1.5708
    c: Tangent(g322,g323) = 1.5708
    c: Tangent(g323,g324) = 1.5708
    c: Tangent(g324,g325) = 1.5708
    c: Tangent(g325,g326) = 1.5708
    c: Tangent(g326,g327) = 1.5708
    c: Tangent(g327,g320) = 1.5708
    c: Horizontal(g323)
    c: Horizontal(g327)
    c: Vertical(g321)
    c: Vertical(g325)
    c: Equal(g320,g322)
    c: Equal(g322,g324)
    c: Equal(g324,g326)
    c: PointOnObject(g328,g321)
    c: PointOnObject(g328,g327)
    c: PointOnObject(g329,g323)
    c: PointOnObject(g329,g325)
    c: PointOnObject(g328,g194)
    c: PointOnObject(g329,g28)
    c: Tangent(g330,g331) = 1.5708
    c: Tangent(g331,g332) = 1.5708
    c: Tangent(g332,g333) = 1.5708
    c: Tangent(g333,g334) = 1.5708
    c: Tangent(g334,g335) = 1.5708
    c: Tangent(g335,g336) = 1.5708
    c: Tangent(g336,g337) = 1.5708
    c: Tangent(g337,g330) = 1.5708
    c: Horizontal(g333)
    c: Horizontal(g337)
    c: Vertical(g331)
    c: Vertical(g335)
    c: Equal(g330,g332)
    c: Equal(g332,g334)
    c: Equal(g334,g336)
    c: PointOnObject(g338,g331)
    c: PointOnObject(g338,g337)
    c: PointOnObject(g339,g333)
    c: PointOnObject(g339,g335)
    c: PointOnObject(g338,g194)
    c: Coincident(g339,g28)
    c: Tangent(g340,g341) = 1.5708
    c: Tangent(g341,g342) = 1.5708
    c: Tangent(g342,g343) = 1.5708
    c: Tangent(g343,g344) = 1.5708
    c: Tangent(g344,g345) = 1.5708
    c: Tangent(g345,g346) = 1.5708
    c: Tangent(g346,g347) = 1.5708
    c: Tangent(g347,g340) = 1.5708
    c: Horizontal(g343)
    c: Horizontal(g347)
    c: Vertical(g341)
    c: Vertical(g345)
    c: Equal(g340,g342)
    c: Equal(g342,g344)
    c: Equal(g344,g346)
    c: PointOnObject(g348,g341)
    c: PointOnObject(g348,g347)
    c: PointOnObject(g349,g343)
    c: PointOnObject(g349,g345)
    c: Coincident(g348,g193)
    c: PointOnObject(g349,g192)
    c: Tangent(g350,g351) = 1.5708
    c: Tangent(g351,g352) = 1.5708
    c: Tangent(g352,g353) = 1.5708
    c: Tangent(g353,g354) = 1.5708
    c: Tangent(g354,g355) = 1.5708
    c: Tangent(g355,g356) = 1.5708
    c: Tangent(g356,g357) = 1.5708
    c: Tangent(g357,g350) = 1.5708
    c: Horizontal(g351)
    c: Horizontal(g355)
    c: Vertical(g353)
    c: Vertical(g357)
    c: Equal(g350,g352)
    c: Equal(g352,g354)
    c: Equal(g354,g356)
    c: PointOnObject(g358,g351)
    c: PointOnObject(g358,g357)
    c: PointOnObject(g359,g353)
    c: PointOnObject(g359,g355)
    c: PointOnObject(g358,g191)
    c: Coincident(g359,g190)
    c: Tangent(g360,g361) = 1.5708
    c: Tangent(g361,g362) = 1.5708
    c: Tangent(g362,g363) = 1.5708
    c: Tangent(g363,g364) = 1.5708
    c: Tangent(g364,g365) = 1.5708
    c: Tangent(g365,g366) = 1.5708
    c: Tangent(g366,g367) = 1.5708
    c: Tangent(g367,g360) = 1.5708
    c: Horizontal(g361)
    c: Horizontal(g365)
    c: Vertical(g363)
    c: Vertical(g367)
    c: Equal(g360,g362)
    c: Equal(g362,g364)
    c: Equal(g364,g366)
    c: PointOnObject(g368,g361)
    c: PointOnObject(g368,g367)
    c: PointOnObject(g369,g363)
    c: PointOnObject(g369,g365)
    c: PointOnObject(g368,g189)
    c: Coincident(g369,g188)
    c: Tangent(g370,g371) = 1.5708
    c: Tangent(g371,g372) = 1.5708
    c: Tangent(g372,g373) = 1.5708
    c: Tangent(g373,g374) = 1.5708
    c: Tangent(g374,g375) = 1.5708
    c: Tangent(g375,g376) = 1.5708
    c: Tangent(g376,g377) = 1.5708
    c: Tangent(g377,g370) = 1.5708
    c: Horizontal(g373)
    c: Horizontal(g377)
    c: Vertical(g371)
    c: Vertical(g375)
    c: Equal(g370,g372)
    c: Equal(g372,g374)
    c: Equal(g374,g376)
    c: PointOnObject(g378,g371)
    c: PointOnObject(g378,g377)
    c: PointOnObject(g379,g373)
    c: PointOnObject(g379,g375)
    c: PointOnObject(g378,g29)
    c: PointOnObject(g379,g186)
    c: Coincident(g380,g330)
    c: Coincident(g380,g325)
    c: Horizontal(g380)
    c: Coincident(g381,g320)
    c: Coincident(g381,g315)
    c: Horizontal(g381)
    c: Coincident(g382,g310)
    c: Coincident(g382,g305)
    c: Horizontal(g382)
    c: Coincident(g383,g300)
    c: Coincident(g383,g295)
    c: Horizontal(g383)
    c: Coincident(g384,g255)
    c: Coincident(g384,g260)
    c: Horizontal(g384)
    c: Coincident(g385,g265)
    c: Coincident(g385,g270)
    c: Horizontal(g385)
    c: Coincident(g386,g280)
    c: Coincident(g386,g275)
    c: Horizontal(g386)
    c: Coincident(g387,g290)
    c: Coincident(g387,g285)
    c: Horizontal(g387)
    c: Coincident(g388,g250)
    c: Coincident(g388,g235)
    c: Horizontal(g388)
    c: Equal(g388, g384-g387) x4
    c: Equal(g383,g388)
    c: Equal(g388,g382)
    c: Equal(g381,g388)
    c: Equal(g380,g388)
    c: Equal(g271,g277)
    c: Equal(g281,g287)
    c: Equal(g307,g305)
    c: Equal(g317,g315)
    c: Equal(g327,g325)
    c: Equal(g236,g257)
    c: Equal(g267,g236)
    c: Equal(g388,g173)
    c: DistanceX(g334,g331) = 20.5
    c: Tangent(g389,g390) = 1.5708
    c: Tangent(g390,g391) = 1.5708
    c: Tangent(g391,g392) = 1.5708
    c: Tangent(g392,g393) = 1.5708
    c: Tangent(g393,g394) = 1.5708
    c: Tangent(g394,g395) = 1.5708
    c: Tangent(g395,g396) = 1.5708
    c: Tangent(g396,g389) = 1.5708
    c: Horizontal(g390)
    c: Horizontal(g394)
    c: Vertical(g392)
    c: Vertical(g396)
    c: Equal(g389,g391)
    c: Equal(g391,g393)
    c: Equal(g393,g395)
    c: PointOnObject(g397,g390)
    c: PointOnObject(g397,g396)
    c: PointOnObject(g398,g392)
    c: PointOnObject(g398,g394)
    c: PointOnObject(g397,g192)
    c: PointOnObject(g398,g193)
    c: Tangent(g399,g400) = 1.5708
    c: Tangent(g400,g401) = 1.5708
    c: Tangent(g401,g402) = 1.5708
    c: Tangent(g402,g403) = 1.5708
    c: Tangent(g403,g404) = 1.5708
    c: Tangent(g404,g405) = 1.5708
    c: Tangent(g405,g406) = 1.5708
    c: Tangent(g406,g399) = 1.5708
    c: Horizontal(g400)
    c: Horizontal(g404)
    c: Vertical(g402)
    c: Vertical(g406)
    c: Equal(g399,g401)
    c: Equal(g401,g403)
    c: Equal(g403,g405)
    c: PointOnObject(g407,g400)
    c: PointOnObject(g407,g406)
    c: PointOnObject(g408,g402)
    c: PointOnObject(g408,g404)
    c: PointOnObject(g407,g192)
    c: PointOnObject(g408,g193)
    c: Tangent(g409,g410) = 1.5708
    c: Tangent(g410,g411) = 1.5708
    c: Tangent(g411,g412) = 1.5708
    c: Tangent(g412,g413) = 1.5708
    c: Tangent(g413,g414) = 1.5708
    c: Tangent(g414,g415) = 1.5708
    c: Tangent(g415,g416) = 1.5708
    c: Tangent(g416,g409) = 1.5708
    c: Horizontal(g410)
    c: Horizontal(g414)
    c: Vertical(g412)
    c: Vertical(g416)
    c: Equal(g409,g411)
    c: Equal(g411,g413)
    c: Equal(g413,g415)
    c: PointOnObject(g417,g410)
    c: PointOnObject(g417,g416)
    c: PointOnObject(g418,g412)
    c: PointOnObject(g418,g414)
    c: PointOnObject(g417,g192)
    c: PointOnObject(g418,g193)
    c: Tangent(g419,g420) = 1.5708
    c: Tangent(g420,g421) = 1.5708
    c: Tangent(g421,g422) = 1.5708
    c: Tangent(g422,g423) = 1.5708
    c: Tangent(g423,g424) = 1.5708
    c: Tangent(g424,g425) = 1.5708
    c: Tangent(g425,g426) = 1.5708
    c: Tangent(g426,g419) = 1.5708
    c: Horizontal(g422)
    c: Horizontal(g426)
    c: Vertical(g420)
    c: Vertical(g424)
    c: Equal(g419,g421)
    c: Equal(g421,g423)
    c: Equal(g423,g425)
    c: PointOnObject(g427,g420)
    c: PointOnObject(g427,g426)
    c: PointOnObject(g428,g422)
    c: PointOnObject(g428,g424)
    c: PointOnObject(g427,g192)
    c: PointOnObject(g428,g193)
    c: Tangent(g429,g430) = 1.5708
    c: Tangent(g430,g431) = 1.5708
    c: Tangent(g431,g432) = 1.5708
    c: Tangent(g432,g433) = 1.5708
    c: Tangent(g433,g434) = 1.5708
    c: Tangent(g434,g435) = 1.5708
    c: Tangent(g435,g436) = 1.5708
    c: Tangent(g436,g429) = 1.5708
    c: Horizontal(g430)
    c: Horizontal(g434)
    c: Vertical(g432)
    c: Vertical(g436)
    c: Equal(g429,g431)
    c: Equal(g431,g433)
    c: Equal(g433,g435)
    c: PointOnObject(g437,g430)
    c: PointOnObject(g437,g436)
    c: PointOnObject(g438,g432)
    c: PointOnObject(g438,g434)
    c: PointOnObject(g437,g192)
    c: PointOnObject(g438,g193)
    c: Tangent(g439,g440) = 1.5708
    c: Tangent(g440,g441) = 1.5708
    c: Tangent(g441,g442) = 1.5708
    c: Tangent(g442,g443) = 1.5708
    c: Tangent(g443,g444) = 1.5708
    c: Tangent(g444,g445) = 1.5708
    c: Tangent(g445,g446) = 1.5708
    c: Tangent(g446,g439) = 1.5708
    c: Horizontal(g440)
    c: Horizontal(g444)
    c: Vertical(g442)
    c: Vertical(g446)
    c: Equal(g439,g441)
    c: Equal(g441,g443)
    c: Equal(g443,g445)
    c: PointOnObject(g447,g440)
    c: PointOnObject(g447,g446)
    c: PointOnObject(g448,g442)
    c: PointOnObject(g448,g444)
    c: PointOnObject(g447,g192)
    c: PointOnObject(g448,g193)
    c: Tangent(g449,g450) = 1.5708
    c: Tangent(g450,g451) = 1.5708
    c: Tangent(g451,g452) = 1.5708
    c: Tangent(g452,g453) = 1.5708
    c: Tangent(g453,g454) = 1.5708
    c: Tangent(g454,g455) = 1.5708
    c: Tangent(g455,g456) = 1.5708
    c: Tangent(g456,g449) = 1.5708
    c: Horizontal(g450)
    c: Horizontal(g454)
    c: Vertical(g452)
    c: Vertical(g456)
    c: Equal(g449,g451)
    c: Equal(g451,g453)
    c: Equal(g453,g455)
    c: PointOnObject(g457,g450)
    c: PointOnObject(g457,g456)
    c: PointOnObject(g458,g452)
    c: PointOnObject(g458,g454)
    c: PointOnObject(g457,g192)
    c: PointOnObject(g458,g193)
    c: Tangent(g459,g460) = 1.5708
    c: Tangent(g460,g461) = 1.5708
    c: Tangent(g461,g462) = 1.5708
    c: Tangent(g462,g463) = 1.5708
    c: Tangent(g463,g464) = 1.5708
    c: Tangent(g464,g465) = 1.5708
    c: Tangent(g465,g466) = 1.5708
    c: Tangent(g466,g459) = 1.5708
    c: Horizontal(g460)
    c: Horizontal(g464)
    c: Vertical(g462)
    c: Vertical(g466)
    c: Equal(g459,g461)
    c: Equal(g461,g463)
    c: Equal(g463,g465)
    c: PointOnObject(g467,g460)
    c: PointOnObject(g467,g466)
    c: PointOnObject(g468,g462)
    c: PointOnObject(g468,g464)
    c: PointOnObject(g467,g192)
    c: PointOnObject(g468,g193)
    c: Tangent(g469,g470) = 1.5708
    c: Tangent(g470,g471) = 1.5708
    c: Tangent(g471,g472) = 1.5708
    c: Tangent(g472,g473) = 1.5708
    c: Tangent(g473,g474) = 1.5708
    c: Tangent(g474,g475) = 1.5708
    c: Tangent(g475,g476) = 1.5708
    c: Tangent(g476,g469) = 1.5708
    c: Horizontal(g470)
    c: Horizontal(g474)
    c: Vertical(g472)
    c: Vertical(g476)
    c: Equal(g469,g471)
    c: Equal(g471,g473)
    c: Equal(g473,g475)
    c: PointOnObject(g477,g470)
    c: PointOnObject(g477,g476)
    c: PointOnObject(g478,g472)
    c: PointOnObject(g478,g474)
    c: PointOnObject(g477,g192)
    c: PointOnObject(g478,g193)
    c: Tangent(g479,g480) = 1.5708
    c: Tangent(g480,g481) = 1.5708
    c: Tangent(g481,g482) = 1.5708
    c: Tangent(g482,g483) = 1.5708
    c: Tangent(g483,g484) = 1.5708
    c: Tangent(g484,g485) = 1.5708
    c: Tangent(g485,g486) = 1.5708
    c: Tangent(g486,g479) = 1.5708
    c: Horizontal(g480)
    c: Horizontal(g484)
    c: Vertical(g482)
    c: Vertical(g486)
    c: Equal(g479,g481)
    c: Equal(g481,g483)
    c: Equal(g483,g485)
    c: PointOnObject(g487,g480)
    c: PointOnObject(g487,g486)
    c: PointOnObject(g488,g482)
    c: PointOnObject(g488,g484)
    c: PointOnObject(g487,g192)
    c: PointOnObject(g488,g193)
    c: Coincident(g489,g471)
    c: Coincident(g489,g459)
    c: Horizontal(g489)
    c: Coincident(g490,g461)
    c: Coincident(g490,g449)
    c: Horizontal(g490)
    c: Coincident(g491,g449)
    c: Coincident(g491,g461)
    c: Coincident(g492,g439)
    c: Coincident(g492,g451)
    c: Horizontal(g492)
    c: Coincident(g493,g441)
    c: Coincident(g493,g429)
    c: Horizontal(g493)
    c: Coincident(g494,g431)
    c: Coincident(g494,g424)
    c: Horizontal(g494)
    c: Coincident(g495,g419)
    c: Coincident(g495,g409)
    c: Horizontal(g495)
    c: Coincident(g496,g411)
    c: Coincident(g496,g399)
    c: Coincident(g497,g401)
    c: Coincident(g497,g389)
    c: Horizontal(g497)
    c: Coincident(g498,g391)
    c: Coincident(g498,g225)
    c: Horizontal(g496)
    c: Coincident(g499,g344)
    c: Coincident(g499,g479)
    c: Coincident(g500,g481)
    c: Coincident(g500,g469)
    c: Horizontal(g500)
    c: Horizontal(g499)
    c: Horizontal(g498)
    c: Equal(g498,g497)
    c: Equal(g496,g498)
    c: Equal(g495,g498)
    c: Equal(g494,g498)
    c: Equal(g493,g498)
    c: Equal(g492,g498)
    c: Equal(g498,g490)
    c: Equal(g489,g498)
    c: Equal(g498,g500)
    c: Equal(g499,g498)
    c: Equal(g390,g392)
    c: DistanceX(g231,g228) = 43.7875
    c: DistanceX(g221,g218) = 34.875
    c: Equal(g498,g173)
    c: Equal(g402,g400)
    c: Equal(g412,g410)
    c: Equal(g426,g424)
    c: Equal(g432,g430)
    c: Equal(g442,g440)
    c: Equal(g452,g450)
    c: Equal(g462,g460)
    c: Equal(g472,g470)
    c: Equal(g482,g480)
    c: Tangent(g501,g502) = 1.5708
    c: Tangent(g502,g503) = 1.5708
    c: Tangent(g503,g504) = 1.5708
    c: Tangent(g504,g505) = 1.5708
    c: Tangent(g505,g506) = 1.5708
    c: Tangent(g506,g507) = 1.5708
    c: Tangent(g507,g508) = 1.5708
    c: Tangent(g508,g501) = 1.5708
    c: Horizontal(g502)
    c: Horizontal(g506)
    c: Vertical(g504)
    c: Vertical(g508)
    c: Equal(g501,g503)
    c: Equal(g503,g505)
    c: Equal(g505,g507)
    c: PointOnObject(g509,g502)
    c: PointOnObject(g509,g508)
    c: PointOnObject(g510,g504)
    c: PointOnObject(g510,g506)
    c: PointOnObject(g509,g190)
    c: PointOnObject(g510,g191)
    c: Tangent(g511,g512) = 1.5708
    c: Tangent(g512,g513) = 1.5708
    c: Tangent(g513,g514) = 1.5708
    c: Tangent(g514,g515) = 1.5708
    c: Tangent(g515,g516) = 1.5708
    c: Tangent(g516,g517) = 1.5708
    c: Tangent(g517,g518) = 1.5708
    c: Tangent(g518,g511) = 1.5708
    c: Horizontal(g512)
    c: Horizontal(g516)
    c: Vertical(g514)
    c: Vertical(g518)
    c: Equal(g511,g513)
    c: Equal(g513,g515)
    c: Equal(g515,g517)
    c: PointOnObject(g519,g512)
    c: PointOnObject(g519,g518)
    c: PointOnObject(g520,g514)
    c: PointOnObject(g520,g516)
    c: PointOnObject(g519,g190)
    c: PointOnObject(g520,g191)
    c: Tangent(g521,g522) = 1.5708
    c: Tangent(g522,g523) = 1.5708
    c: Tangent(g523,g524) = 1.5708
    c: Tangent(g524,g525) = 1.5708
    c: Tangent(g525,g526) = 1.5708
    c: Tangent(g526,g527) = 1.5708
    c: Tangent(g527,g528) = 1.5708
    c: Tangent(g528,g521) = 1.5708
    c: Horizontal(g522)
    c: Horizontal(g526)
    c: Vertical(g524)
    c: Vertical(g528)
    c: Equal(g521,g523)
    c: Equal(g523,g525)
    c: Equal(g525,g527)
    c: PointOnObject(g529,g522)
    c: PointOnObject(g529,g528)
    c: PointOnObject(g530,g524)
    c: PointOnObject(g530,g526)
    c: PointOnObject(g529,g190)
    c: PointOnObject(g530,g191)
    c: Tangent(g531,g532) = 1.5708
    c: Tangent(g532,g533) = 1.5708
    c: Tangent(g533,g534) = 1.5708
    c: Tangent(g534,g535) = 1.5708
    c: Tangent(g535,g536) = 1.5708
    c: Tangent(g536,g537) = 1.5708
    c: Tangent(g537,g538) = 1.5708
    c: Tangent(g538,g531) = 1.5708
    c: Horizontal(g532)
    c: Horizontal(g536)
    c: Vertical(g534)
    c: Vertical(g538)
    c: Equal(g531,g533)
    c: Equal(g533,g535)
    c: Equal(g535,g537)
    c: PointOnObject(g539,g532)
    c: PointOnObject(g539,g538)
    c: PointOnObject(g540,g534)
    c: PointOnObject(g540,g536)
    c: PointOnObject(g539,g190)
    c: PointOnObject(g540,g191)
    c: Tangent(g541,g542) = 1.5708
    c: Tangent(g542,g543) = 1.5708
    c: Tangent(g543,g544) = 1.5708
    c: Tangent(g544,g545) = 1.5708
    c: Tangent(g545,g546) = 1.5708
    c: Tangent(g546,g547) = 1.5708
    c: Tangent(g547,g548) = 1.5708
    c: Tangent(g548,g541) = 1.5708
    c: Horizontal(g542)
    c: Horizontal(g546)
    c: Vertical(g544)
    c: Vertical(g548)
    c: Equal(g541,g543)
    c: Equal(g543,g545)
    c: Equal(g545,g547)
    c: PointOnObject(g549,g542)
    c: PointOnObject(g549,g548)
    c: PointOnObject(g550,g544)
    c: PointOnObject(g550,g546)
    c: PointOnObject(g549,g190)
    c: PointOnObject(g550,g191)
    c: Tangent(g551,g552) = 1.5708
    c: Tangent(g552,g553) = 1.5708
    c: Tangent(g553,g554) = 1.5708
    c: Tangent(g554,g555) = 1.5708
    c: Tangent(g555,g556) = 1.5708
    c: Tangent(g556,g557) = 1.5708
    c: Tangent(g557,g558) = 1.5708
    c: Tangent(g558,g551) = 1.5708
    c: Horizontal(g552)
    c: Horizontal(g556)
    c: Vertical(g554)
    c: Vertical(g558)
    c: Equal(g551,g553)
    c: Equal(g553,g555)
    c: Equal(g555,g557)
    c: PointOnObject(g559,g552)
    c: PointOnObject(g559,g558)
    c: PointOnObject(g560,g554)
    c: PointOnObject(g560,g556)
    c: PointOnObject(g559,g190)
    c: PointOnObject(g560,g191)
    c: Tangent(g561,g562) = 1.5708
    c: Tangent(g562,g563) = 1.5708
    c: Tangent(g563,g564) = 1.5708
    c: Tangent(g564,g565) = 1.5708
    c: Tangent(g565,g566) = 1.5708
    c: Tangent(g566,g567) = 1.5708
    c: Tangent(g567,g568) = 1.5708
    c: Tangent(g568,g561) = 1.5708
    c: Horizontal(g562)
    c: Horizontal(g566)
    c: Vertical(g564)
    c: Vertical(g568)
    c: Equal(g561,g563)
    c: Equal(g563,g565)
    c: Equal(g565,g567)
    c: PointOnObject(g569,g562)
    c: PointOnObject(g569,g568)
    c: PointOnObject(g570,g564)
    c: PointOnObject(g570,g566)
    c: PointOnObject(g569,g190)
    c: PointOnObject(g570,g191)
    c: Tangent(g571,g572) = 1.5708
    c: Tangent(g572,g573) = 1.5708
    c: Tangent(g573,g574) = 1.5708
    c: Tangent(g574,g575) = 1.5708
    c: Tangent(g575,g576) = 1.5708
    c: Tangent(g576,g577) = 1.5708
    c: Tangent(g577,g578) = 1.5708
    c: Tangent(g578,g571) = 1.5708
    c: Horizontal(g572)
    c: Horizontal(g576)
    c: Vertical(g574)
    c: Vertical(g578)
    c: Equal(g571,g573)
    c: Equal(g573,g575)
    c: Equal(g575,g577)
    c: PointOnObject(g579,g572)
    c: PointOnObject(g579,g578)
    c: PointOnObject(g580,g574)
    c: PointOnObject(g580,g576)
    c: PointOnObject(g579,g190)
    c: PointOnObject(g580,g191)
    c: Tangent(g581,g582) = 1.5708
    c: Tangent(g582,g583) = 1.5708
    c: Tangent(g583,g584) = 1.5708
    c: Tangent(g584,g585) = 1.5708
    c: Tangent(g585,g586) = 1.5708
    c: Tangent(g586,g587) = 1.5708
    c: Tangent(g587,g588) = 1.5708
    c: Tangent(g588,g581) = 1.5708
    c: Horizontal(g582)
    c: Horizontal(g586)
    c: Vertical(g584)
    c: Vertical(g588)
    c: Equal(g581,g583)
    c: Equal(g583,g585)
    c: Equal(g585,g587)
    c: PointOnObject(g589,g582)
    c: PointOnObject(g589,g588)
    c: PointOnObject(g590,g584)
    c: PointOnObject(g590,g586)
    c: PointOnObject(g589,g190)
    c: PointOnObject(g590,g191)
    c: Tangent(g591,g592) = 1.5708
    c: Tangent(g592,g593) = 1.5708
    c: Tangent(g593,g594) = 1.5708
    c: Tangent(g594,g595) = 1.5708
    c: Tangent(g595,g596) = 1.5708
    c: Tangent(g596,g597) = 1.5708
    c: Tangent(g597,g598) = 1.5708
    c: Tangent(g598,g591) = 1.5708
    c: Horizontal(g592)
    c: Horizontal(g596)
    c: Vertical(g594)
    c: Vertical(g598)
    c: Equal(g591,g593)
    c: Equal(g593,g595)
    c: Equal(g595,g597)
    c: PointOnObject(g599,g592)
    c: PointOnObject(g599,g598)
    c: PointOnObject(g600,g594)
    c: PointOnObject(g600,g596)
    c: PointOnObject(g599,g190)
    c: PointOnObject(g600,g191)
    c: Tangent(g601,g602) = 1.5708
    c: Tangent(g602,g603) = 1.5708
    c: Tangent(g603,g604) = 1.5708
    c: Tangent(g604,g605) = 1.5708
    c: Tangent(g605,g606) = 1.5708
    c: Tangent(g606,g607) = 1.5708
    c: Tangent(g607,g608) = 1.5708
    c: Tangent(g608,g601) = 1.5708
    c: Horizontal(g602)
    c: Horizontal(g606)
    c: Vertical(g604)
    c: Vertical(g608)
    c: Equal(g601,g603)
    c: Equal(g603,g605)
    c: Equal(g605,g607)
    c: PointOnObject(g609,g602)
    c: PointOnObject(g609,g608)
    c: PointOnObject(g610,g604)
    c: PointOnObject(g610,g606)
    c: PointOnObject(g609,g190)
    c: PointOnObject(g610,g191)
    c: Coincident(g611,g601)
    c: Coincident(g611,g593)
    c: Horizontal(g611)
    c: Coincident(g612,g563)
    c: Coincident(g612,g571)
    c: Horizontal(g612)
    c: Coincident(g613,g573)
    c: Coincident(g613,g581)
    c: Horizontal(g613)
    c: Coincident(g614,g583)
    c: Coincident(g614,g591)
    c: Horizontal(g614)
    c: Coincident(g615,g215)
    c: Coincident(g615,g603)
    c: Coincident(g616,g561)
    c: Coincident(g616,g553)
    c: Horizontal(g616)
    c: Coincident(g617,g541)
    c: Coincident(g617,g533)
    c: Horizontal(g617)
    c: Coincident(g618,g543)
    c: Coincident(g618,g551)
    c: Horizontal(g618)
    c: Coincident(g619,g523)
    c: Coincident(g619,g531)
    c: Horizontal(g619)
    c: Coincident(g620,g513)
    c: Coincident(g620,g521)
    c: Horizontal(g620)
    c: Coincident(g621,g503)
    c: Coincident(g621,g511)
    c: Horizontal(g621)
    c: Coincident(g622,g356)
    c: Coincident(g622,g501)
    c: Horizontal(g622)
    c: Horizontal(g615)
    c: Equal(g616,g615)
    c: Equal(g615,g611)
    c: Equal(g614,g615)
    c: Equal(g613,g615)
    c: Equal(g612,g615)
    c: Equal(g615,g618)
    c: Equal(g617,g615)
    c: Equal(g615,g619)
    c: Equal(g620,g615)
    c: Equal(g615,g621)
    c: Equal(g622,g615)
    c: Equal(g602,g604)
    c: Equal(g615,g173)
    c: Equal(g594,g592)
    c: Equal(g584,g582)
    c: Equal(g574,g572)
    c: Equal(g564,g562)
    c: Equal(g554,g552)
    c: Equal(g544,g542)
    c: Equal(g534,g532)
    c: Equal(g524,g522)
    c: Equal(g514,g512)
    c: Equal(g504,g502)
    c: Tangent(g623,g624) = 1.5708
    c: Tangent(g624,g625) = 1.5708
    c: Tangent(g625,g626) = 1.5708
    c: Tangent(g626,g627) = 1.5708
    c: Tangent(g627,g628) = 1.5708
    c: Tangent(g628,g629) = 1.5708
    c: Tangent(g629,g630) = 1.5708
    c: Tangent(g630,g623) = 1.5708
    c: Horizontal(g624)
    c: Horizontal(g628)
    c: Vertical(g626)
    c: Vertical(g630)
    c: Equal(g623,g625)
    c: Equal(g625,g627)
    c: Equal(g627,g629)
    c: PointOnObject(g631,g624)
    c: PointOnObject(g631,g630)
    c: PointOnObject(g632,g626)
    c: PointOnObject(g632,g628)
    c: PointOnObject(g631,g186)
    c: PointOnObject(g632,g187)
    c: Tangent(g633,g634) = 1.5708
    c: Tangent(g634,g635) = 1.5708
    c: Tangent(g635,g636) = 1.5708
    c: Tangent(g636,g637) = 1.5708
    c: Tangent(g637,g638) = 1.5708
    c: Tangent(g638,g639) = 1.5708
    c: Tangent(g639,g640) = 1.5708
    c: Tangent(g640,g633) = 1.5708
    c: Horizontal(g634)
    c: Horizontal(g638)
    c: Vertical(g636)
    c: Vertical(g640)
    c: Equal(g633,g635)
    c: Equal(g635,g637)
    c: Equal(g637,g639)
    c: PointOnObject(g641,g634)
    c: PointOnObject(g641,g640)
    c: PointOnObject(g642,g636)
    c: PointOnObject(g642,g638)
    c: PointOnObject(g641,g186)
    c: PointOnObject(g642,g187)
    c: Tangent(g643,g644) = 1.5708
    c: Tangent(g644,g645) = 1.5708
    c: Tangent(g645,g646) = 1.5708
    c: Tangent(g646,g647) = 1.5708
    c: Tangent(g647,g648) = 1.5708
    c: Tangent(g648,g649) = 1.5708
    c: Tangent(g649,g650) = 1.5708
    c: Tangent(g650,g643) = 1.5708
    c: Horizontal(g644)
    c: Horizontal(g648)
    c: Vertical(g646)
    c: Vertical(g650)
    c: Equal(g643,g645)
    c: Equal(g645,g647)
    c: Equal(g647,g649)
    c: PointOnObject(g651,g644)
    c: PointOnObject(g651,g650)
    c: PointOnObject(g652,g646)
    c: PointOnObject(g652,g648)
    c: PointOnObject(g651,g186)
    c: PointOnObject(g652,g187)
    c: Tangent(g653,g654) = 1.5708
    c: Tangent(g654,g655) = 1.5708
    c: Tangent(g655,g656) = 1.5708
    c: Tangent(g656,g657) = 1.5708
    c: Tangent(g657,g658) = 1.5708
    c: Tangent(g658,g659) = 1.5708
    c: Tangent(g659,g660) = 1.5708
    c: Tangent(g660,g653) = 1.5708
    c: Horizontal(g654)
    c: Horizontal(g658)
    c: Vertical(g656)
    c: Vertical(g660)
    c: Equal(g653,g655)
    c: Equal(g655,g657)
    c: Equal(g657,g659)
    c: PointOnObject(g661,g654)
    c: PointOnObject(g661,g660)
    c: PointOnObject(g662,g656)
    c: PointOnObject(g662,g658)
    c: PointOnObject(g661,g186)
    c: PointOnObject(g662,g187)
    c: Tangent(g663,g664) = 1.5708
    c: Tangent(g664,g665) = 1.5708
    c: Tangent(g665,g666) = 1.5708
    c: Tangent(g666,g667) = 1.5708
    c: Tangent(g667,g668) = 1.5708
    c: Tangent(g668,g669) = 1.5708
    c: Tangent(g669,g670) = 1.5708
    c: Tangent(g670,g663) = 1.5708
    c: Horizontal(g664)
    c: Horizontal(g668)
    c: Vertical(g666)
    c: Vertical(g670)
    c: Equal(g663,g665)
    c: Equal(g665,g667)
    c: Equal(g667,g669)
    c: PointOnObject(g671,g664)
    c: PointOnObject(g671,g670)
    c: PointOnObject(g672,g666)
    c: PointOnObject(g672,g668)
    c: PointOnObject(g671,g186)
    c: PointOnObject(g672,g187)
    c: Tangent(g673,g674) = 1.5708
    c: Tangent(g674,g675) = 1.5708
    c: Tangent(g675,g676) = 1.5708
    c: Tangent(g676,g677) = 1.5708
    c: Tangent(g677,g678) = 1.5708
    c: Tangent(g678,g679) = 1.5708
    c: Tangent(g679,g680) = 1.5708
    c: Tangent(g680,g673) = 1.5708
    c: Horizontal(g674)
    c: Horizontal(g678)
    c: Vertical(g676)
    c: Vertical(g680)
    c: Equal(g673,g675)
    c: Equal(g675,g677)
    c: Equal(g677,g679)
    c: PointOnObject(g681,g674)
    c: PointOnObject(g681,g680)
    c: PointOnObject(g682,g676)
    c: PointOnObject(g682,g678)
    c: PointOnObject(g681,g186)
    c: PointOnObject(g682,g187)
    c: Tangent(g683,g684) = 1.5708
    c: Tangent(g684,g685) = 1.5708
    c: Tangent(g685,g686) = 1.5708
    c: Tangent(g686,g687) = 1.5708
    c: Tangent(g687,g688) = 1.5708
    c: Tangent(g688,g689) = 1.5708
    c: Tangent(g689,g690) = 1.5708
    c: Tangent(g690,g683) = 1.5708
    c: Horizontal(g684)
    c: Horizontal(g688)
    c: Vertical(g686)
    c: Vertical(g690)
    c: Equal(g683,g685)
    c: Equal(g685,g687)
    c: Equal(g687,g689)
    c: PointOnObject(g691,g684)
    c: PointOnObject(g691,g690)
    c: PointOnObject(g692,g686)
    c: PointOnObject(g692,g688)
    c: PointOnObject(g691,g186)
    c: PointOnObject(g692,g187)
    c: Tangent(g693,g694) = 1.5708
    c: Tangent(g694,g695) = 1.5708
    c: Tangent(g695,g696) = 1.5708
    c: Tangent(g696,g697) = 1.5708
    c: Tangent(g697,g698) = 1.5708
    c: Tangent(g698,g699) = 1.5708
    c: Tangent(g699,g700) = 1.5708
    c: Tangent(g700,g693) = 1.5708
    c: Horizontal(g694)
    c: Horizontal(g698)
    c: Vertical(g696)
    c: Vertical(g700)
    c: Equal(g693,g695)
    c: Equal(g695,g697)
    c: Equal(g697,g699)
    c: PointOnObject(g701,g694)
    c: PointOnObject(g701,g700)
    c: PointOnObject(g702,g696)
    c: PointOnObject(g702,g698)
    c: PointOnObject(g701,g186)
    c: PointOnObject(g702,g187)
    c: Tangent(g703,g704) = 1.5708
    c: Tangent(g704,g705) = 1.5708
    c: Tangent(g705,g706) = 1.5708
    c: Tangent(g706,g707) = 1.5708
    c: Tangent(g707,g708) = 1.5708
    c: Tangent(g708,g709) = 1.5708
    c: Tangent(g709,g710) = 1.5708
    c: Tangent(g710,g703) = 1.5708
    c: Horizontal(g704)
    c: Horizontal(g708)
    c: Vertical(g706)
    c: Vertical(g710)
    c: Equal(g703,g705)
    c: Equal(g705,g707)
    c: Equal(g707,g709)
    c: PointOnObject(g711,g704)
    c: PointOnObject(g711,g710)
    c: PointOnObject(g712,g706)
    c: PointOnObject(g712,g708)
    c: PointOnObject(g711,g186)
    c: PointOnObject(g712,g187)
    c: Tangent(g713,g714) = 1.5708
    c: Tangent(g714,g715) = 1.5708
    c: Tangent(g715,g716) = 1.5708
    c: Tangent(g716,g717) = 1.5708
    c: Tangent(g717,g718) = 1.5708
    c: Tangent(g718,g719) = 1.5708
    c: Tangent(g719,g720) = 1.5708
    c: Tangent(g720,g713) = 1.5708
    c: Horizontal(g714)
    c: Horizontal(g718)
    c: Vertical(g716)
    c: Vertical(g720)
    c: Equal(g713,g715)
    c: Equal(g715,g717)
    c: Equal(g717,g719)
    c: PointOnObject(g721,g714)
    c: PointOnObject(g721,g720)
    c: PointOnObject(g722,g716)
    c: PointOnObject(g722,g718)
    c: PointOnObject(g721,g186)
    c: PointOnObject(g722,g187)
    c: Tangent(g723,g724) = 1.5708
    c: Tangent(g724,g725) = 1.5708
    c: Tangent(g725,g726) = 1.5708
    c: Tangent(g726,g727) = 1.5708
    c: Tangent(g727,g728) = 1.5708
    c: Tangent(g728,g729) = 1.5708
    c: Tangent(g729,g730) = 1.5708
    c: Tangent(g730,g723) = 1.5708
    c: Horizontal(g724)
    c: Horizontal(g728)
    c: Vertical(g726)
    c: Vertical(g730)
    c: Equal(g723,g725)
    c: Equal(g725,g727)
    c: Equal(g727,g729)
    c: PointOnObject(g731,g724)
    c: PointOnObject(g731,g730)
    c: PointOnObject(g732,g726)
    c: PointOnObject(g732,g728)
    c: PointOnObject(g731,g186)
    c: PointOnObject(g732,g187)
    c: Tangent(g733,g734) = 1.5708
    c: Tangent(g734,g735) = 1.5708
    c: Tangent(g735,g736) = 1.5708
    c: Tangent(g736,g737) = 1.5708
    c: Tangent(g737,g738) = 1.5708
    c: Tangent(g738,g739) = 1.5708
    c: Tangent(g739,g740) = 1.5708
    c: Tangent(g740,g733) = 1.5708
    c: Horizontal(g734)
    c: Horizontal(g738)
    c: Vertical(g736)
    c: Vertical(g740)
    c: Equal(g733,g735)
    c: Equal(g735,g737)
    c: Equal(g737,g739)
    c: PointOnObject(g741,g734)
    c: PointOnObject(g741,g740)
    c: PointOnObject(g742,g736)
    c: PointOnObject(g742,g738)
    c: PointOnObject(g741,g186)
    c: PointOnObject(g742,g187)
    c: Tangent(g743,g744) = 1.5708
    c: Tangent(g744,g745) = 1.5708
    c: Tangent(g745,g746) = 1.5708
    c: Tangent(g746,g747) = 1.5708
    c: Tangent(g747,g748) = 1.5708
    c: Tangent(g748,g749) = 1.5708
    c: Tangent(g749,g750) = 1.5708
    c: Tangent(g750,g743) = 1.5708
    c: Horizontal(g744)
    c: Horizontal(g748)
    c: Vertical(g746)
    c: Vertical(g750)
    c: Equal(g743,g745)
    c: Equal(g745,g747)
    c: Equal(g747,g749)
    c: PointOnObject(g751,g744)
    c: PointOnObject(g751,g750)
    c: PointOnObject(g752,g746)
    c: PointOnObject(g752,g748)
    c: PointOnObject(g751,g188)
    c: PointOnObject(g752,g189)
    c: Tangent(g753,g754) = 1.5708
    c: Tangent(g754,g755) = 1.5708
    c: Tangent(g755,g756) = 1.5708
    c: Tangent(g756,g757) = 1.5708
    c: Tangent(g757,g758) = 1.5708
    c: Tangent(g758,g759) = 1.5708
    c: Tangent(g759,g760) = 1.5708
    c: Tangent(g760,g753) = 1.5708
    c: Horizontal(g754)
    c: Horizontal(g758)
    c: Vertical(g756)
    c: Vertical(g760)
    c: Equal(g753,g755)
    c: Equal(g755,g757)
    c: Equal(g757,g759)
    c: PointOnObject(g761,g754)
    c: PointOnObject(g761,g760)
    c: PointOnObject(g762,g756)
    c: PointOnObject(g762,g758)
    c: PointOnObject(g761,g188)
    c: PointOnObject(g762,g189)
    c: Tangent(g763,g764) = 1.5708
    c: Tangent(g764,g765) = 1.5708
    c: Tangent(g765,g766) = 1.5708
    c: Tangent(g766,g767) = 1.5708
    c: Tangent(g767,g768) = 1.5708
    c: Tangent(g768,g769) = 1.5708
    c: Tangent(g769,g770) = 1.5708
    c: Tangent(g770,g763) = 1.5708
    c: Horizontal(g764)
    c: Horizontal(g768)
    c: Vertical(g766)
    c: Vertical(g770)
    c: Equal(g763,g765)
    c: Equal(g765,g767)
    c: Equal(g767,g769)
    c: PointOnObject(g771,g764)
    c: PointOnObject(g771,g770)
    c: PointOnObject(g772,g766)
    c: PointOnObject(g772,g768)
    c: PointOnObject(g771,g188)
    c: PointOnObject(g772,g189)
    c: Tangent(g773,g774) = 1.5708
    c: Tangent(g774,g775) = 1.5708
    c: Tangent(g775,g776) = 1.5708
    c: Tangent(g776,g777) = 1.5708
    c: Tangent(g777,g778) = 1.5708
    c: Tangent(g778,g779) = 1.5708
    c: Tangent(g779,g780) = 1.5708
    c: Tangent(g780,g773) = 1.5708
    c: Horizontal(g774)
    c: Horizontal(g778)
    c: Vertical(g776)
    c: Vertical(g780)
    c: Equal(g773,g775)
    c: Equal(g775,g777)
    c: Equal(g777,g779)
    c: PointOnObject(g781,g774)
    c: PointOnObject(g781,g780)
    c: PointOnObject(g782,g776)
    c: PointOnObject(g782,g778)
    c: PointOnObject(g781,g188)
    c: PointOnObject(g782,g189)
    c: Tangent(g783,g784) = 1.5708
    c: Tangent(g784,g785) = 1.5708
    c: Tangent(g785,g786) = 1.5708
    c: Tangent(g786,g787) = 1.5708
    c: Tangent(g787,g788) = 1.5708
    c: Tangent(g788,g789) = 1.5708
    c: Tangent(g789,g790) = 1.5708
    c: Tangent(g790,g783) = 1.5708
    c: Horizontal(g784)
    c: Horizontal(g788)
    c: Vertical(g786)
    c: Vertical(g790)
    c: Equal(g783,g785)
    c: Equal(g785,g787)
    c: Equal(g787,g789)
    c: PointOnObject(g791,g784)
    c: PointOnObject(g791,g790)
    c: PointOnObject(g792,g786)
    c: PointOnObject(g792,g788)
    c: PointOnObject(g791,g188)
    c: PointOnObject(g792,g189)
    c: Tangent(g793,g794) = 1.5708
    c: Tangent(g794,g795) = 1.5708
    c: Tangent(g795,g796) = 1.5708
    c: Tangent(g796,g797) = 1.5708
    c: Tangent(g797,g798) = 1.5708
    c: Tangent(g798,g799) = 1.5708
    c: Tangent(g799,g800) = 1.5708
    c: Tangent(g800,g793) = 1.5708
    c: Horizontal(g794)
    c: Horizontal(g798)
    c: Vertical(g796)
    c: Vertical(g800)
    c: Equal(g793,g795)
    c: Equal(g795,g797)
    c: Equal(g797,g799)
    c: PointOnObject(g801,g794)
    c: PointOnObject(g801,g800)
    c: PointOnObject(g802,g796)
    c: PointOnObject(g802,g798)
    c: PointOnObject(g801,g188)
    c: PointOnObject(g802,g189)
    c: Tangent(g803,g804) = 1.5708
    c: Tangent(g804,g805) = 1.5708
    c: Tangent(g805,g806) = 1.5708
    c: Tangent(g806,g807) = 1.5708
    c: Tangent(g807,g808) = 1.5708
    c: Tangent(g808,g809) = 1.5708
    c: Tangent(g809,g810) = 1.5708
    c: Tangent(g810,g803) = 1.5708
    c: Horizontal(g804)
    c: Horizontal(g808)
    c: Vertical(g806)
    c: Vertical(g810)
    c: Equal(g803,g805)
    c: Equal(g805,g807)
    c: Equal(g807,g809)
    c: PointOnObject(g811,g804)
    c: PointOnObject(g811,g810)
    c: PointOnObject(g812,g806)
    c: PointOnObject(g812,g808)
    c: PointOnObject(g811,g188)
    c: PointOnObject(g812,g189)
    c: Tangent(g813,g814) = 1.5708
    c: Tangent(g814,g815) = 1.5708
    c: Tangent(g815,g816) = 1.5708
    c: Tangent(g816,g817) = 1.5708
    c: Tangent(g817,g818) = 1.5708
    c: Tangent(g818,g819) = 1.5708
    c: Tangent(g819,g820) = 1.5708
    c: Tangent(g820,g813) = 1.5708
    c: Horizontal(g814)
    c: Horizontal(g818)
    c: Vertical(g816)
    c: Vertical(g820)
    c: Equal(g813,g815)
    c: Equal(g815,g817)
    c: Equal(g817,g819)
    c: PointOnObject(g821,g814)
    c: PointOnObject(g821,g820)
    c: PointOnObject(g822,g816)
    c: PointOnObject(g822,g818)
    c: PointOnObject(g821,g188)
    c: PointOnObject(g822,g189)
    c: Tangent(g823,g824) = 1.5708
    c: Tangent(g824,g825) = 1.5708
    c: Tangent(g825,g826) = 1.5708
    c: Tangent(g826,g827) = 1.5708
    c: Tangent(g827,g828) = 1.5708
    c: Tangent(g828,g829) = 1.5708
    c: Tangent(g829,g830) = 1.5708
    c: Tangent(g830,g823) = 1.5708
    c: Horizontal(g824)
    c: Horizontal(g828)
    c: Vertical(g826)
    c: Vertical(g830)
    c: Equal(g823,g825)
    c: Equal(g825,g827)
    c: Equal(g827,g829)
    c: PointOnObject(g831,g824)
    c: PointOnObject(g831,g830)
    c: PointOnObject(g832,g826)
    c: PointOnObject(g832,g828)
    c: PointOnObject(g831,g188)
    c: PointOnObject(g832,g189)
    c: Tangent(g833,g834) = 1.5708
    c: Tangent(g834,g835) = 1.5708
    c: Tangent(g835,g836) = 1.5708
    c: Tangent(g836,g837) = 1.5708
    c: Tangent(g837,g838) = 1.5708
    c: Tangent(g838,g839) = 1.5708
    c: Tangent(g839,g840) = 1.5708
    c: Tangent(g840,g833) = 1.5708
    c: Horizontal(g834)
    c: Horizontal(g838)
    c: Vertical(g836)
    c: Vertical(g840)
    c: Equal(g833,g835)
    c: Equal(g835,g837)
    c: Equal(g837,g839)
    c: PointOnObject(g841,g834)
    c: PointOnObject(g841,g840)
    c: PointOnObject(g842,g836)
    c: PointOnObject(g842,g838)
    c: PointOnObject(g841,g188)
    c: PointOnObject(g842,g189)
    c: Tangent(g843,g844) = 1.5708
    c: Tangent(g844,g845) = 1.5708
    c: Tangent(g845,g846) = 1.5708
    c: Tangent(g846,g847) = 1.5708
    c: Tangent(g847,g848) = 1.5708
    c: Tangent(g848,g849) = 1.5708
    c: Tangent(g849,g850) = 1.5708
    c: Tangent(g850,g843) = 1.5708
    c: Horizontal(g844)
    c: Horizontal(g848)
    c: Vertical(g846)
    c: Vertical(g850)
    c: Equal(g843,g845)
    c: Equal(g845,g847)
    c: Equal(g847,g849)
    c: PointOnObject(g851,g844)
    c: PointOnObject(g851,g850)
    c: PointOnObject(g852,g846)
    c: PointOnObject(g852,g848)
    c: PointOnObject(g851,g188)
    c: PointOnObject(g852,g189)
    c: Tangent(g853,g854) = 1.5708
    c: Tangent(g854,g855) = 1.5708
    c: Tangent(g855,g856) = 1.5708
    c: Tangent(g856,g857) = 1.5708
    c: Tangent(g857,g858) = 1.5708
    c: Tangent(g858,g859) = 1.5708
    c: Tangent(g859,g860) = 1.5708
    c: Tangent(g860,g853) = 1.5708
    c: Horizontal(g854)
    c: Horizontal(g858)
    c: Vertical(g856)
    c: Vertical(g860)
    c: Equal(g853,g855)
    c: Equal(g855,g857)
    c: Equal(g857,g859)
    c: PointOnObject(g861,g854)
    c: PointOnObject(g861,g860)
    c: PointOnObject(g862,g856)
    c: PointOnObject(g862,g858)
    c: PointOnObject(g861,g188)
    c: PointOnObject(g862,g189)
    c: Coincident(g863,g625)
    c: Coincident(g863,g198)
    c: Coincident(g864,g623)
    c: Coincident(g864,g635)
    c: Horizontal(g864)
    c: Coincident(g865,g645)
    c: Coincident(g865,g633)
    c: Horizontal(g865)
    c: Coincident(g866,g685)
    c: Coincident(g866,g673)
    c: Horizontal(g866)
    c: Coincident(g867,g675)
    c: Coincident(g867,g663)
    c: Horizontal(g867)
    c: Coincident(g868,g665)
    c: Coincident(g868,g653)
    c: Horizontal(g868)
    c: Coincident(g869,g655)
    c: Coincident(g869,g643)
    c: Horizontal(g869)
    c: Coincident(g870,g208)
    c: Coincident(g870,g855)
    c: Coincident(g871,g853)
    c: Coincident(g871,g845)
    c: Horizontal(g871)
    c: Coincident(g872,g843)
    c: Coincident(g872,g835)
    c: Coincident(g873,g833)
    c: Coincident(g873,g825)
    c: Coincident(g874,g823)
    c: Coincident(g874,g815)
    c: Coincident(g875,g813)
    c: Coincident(g875,g805)
    c: Horizontal(g875)
    c: Coincident(g876,g803)
    c: Coincident(g876,g795)
    c: Horizontal(g876)
    c: Horizontal(g874)
    c: Horizontal(g873)
    c: Horizontal(g872)
    c: Coincident(g877,g374)
    c: Coincident(g877,g733)
    c: Coincident(g878,g735)
    c: Coincident(g878,g723)
    c: Horizontal(g878)
    c: Coincident(g879,g725)
    c: Coincident(g879,g713)
    c: Coincident(g880,g715)
    c: Coincident(g880,g703)
    c: Coincident(g881,g705)
    c: Coincident(g881,g693)
    c: Coincident(g882,g695)
    c: Coincident(g882,g683)
    c: Coincident(g883,g793)
    c: Coincident(g883,g785)
    c: Horizontal(g883)
    c: Coincident(g884,g783)
    c: Coincident(g884,g775)
    c: Coincident(g885,g773)
    c: Coincident(g885,g765)
    c: Horizontal(g885)
    c: Coincident(g886,g763)
    c: Coincident(g886,g755)
    c: Coincident(g887,g753)
    c: Coincident(g887,g745)
    c: Horizontal(g887)
    c: Coincident(g888,g743)
    c: Coincident(g888,g366)
    c: Horizontal(g888)
    c: Horizontal(g882)
    c: Horizontal(g881)
    c: Horizontal(g880)
    c: Horizontal(g879)
    c: Horizontal(g877)
    c: Horizontal(g886)
    c: Horizontal(g884)
    c: Horizontal(g863)
    c: Horizontal(g870)
    c: Equal(g863,g864)
    c: Equal(g865,g863)
    c: Equal(g869,g863)
    c: Equal(g868,g863)
    c: Equal(g863,g882)
    c: Equal(g881,g863)
    c: Equal(g863,g880)
    c: Equal(g879,g863)
    c: Equal(g870,g871)
    c: Equal(g870,g872)
    c: Equal(g870,g873)
    c: Equal(g874,g870)
    c: Equal(g870,g875)
    c: Equal(g876,g870)
    c: Equal(g867,g866)
    c: Equal(g866,g863)
    c: PointOnObject(g376,g187)
    c: Equal(g883,g870)
    c: Equal(g884,g870)
    c: Equal(g885,g870)
    c: Equal(g886,g870)
    c: Equal(g870,g887)
    c: Equal(g870,g888)
    c: Equal(g877,g863)
    c: Equal(g878,g863)
    c: Equal(g854,g860)
    c: Equal(g624,g630)
    c: Equal(g654,g660)
    c: Equal(g674,g680)
    c: Equal(g824,g826)
    c: Equal(g844,g846)
    c: Equal(g806,g804)
    c: Equal(g796,g794)
    c: Equal(g786,g784)
    c: Equal(g776,g774)
    c: Equal(g766,g764)
    c: Equal(g834,g836)
    c: Equal(g814,g816)
    c: Equal(g754,g756)
    c: Equal(g744,g746)
    c: Equal(g373,g375)
    c: Equal(g734,g736)
    c: Equal(g724,g726)
    c: Equal(g714,g716)
    c: DistanceX(g362,g360) = 24.5
    c: Equal(g686,g684)
    c: Equal(g706,g704)
    c: Equal(g694,g696)
    c: Equal(g664,g666)
    c: Equal(g644,g646)
    c: Equal(g634,g636)
    c: DistanceX(g1,g10) = 18.25
FEATURE [PartDesign::Body] Body
  Group = -> [Sketch009,Sketch,Sketch010,Sketch011,Sketch012]
  Origin = -> Origin
